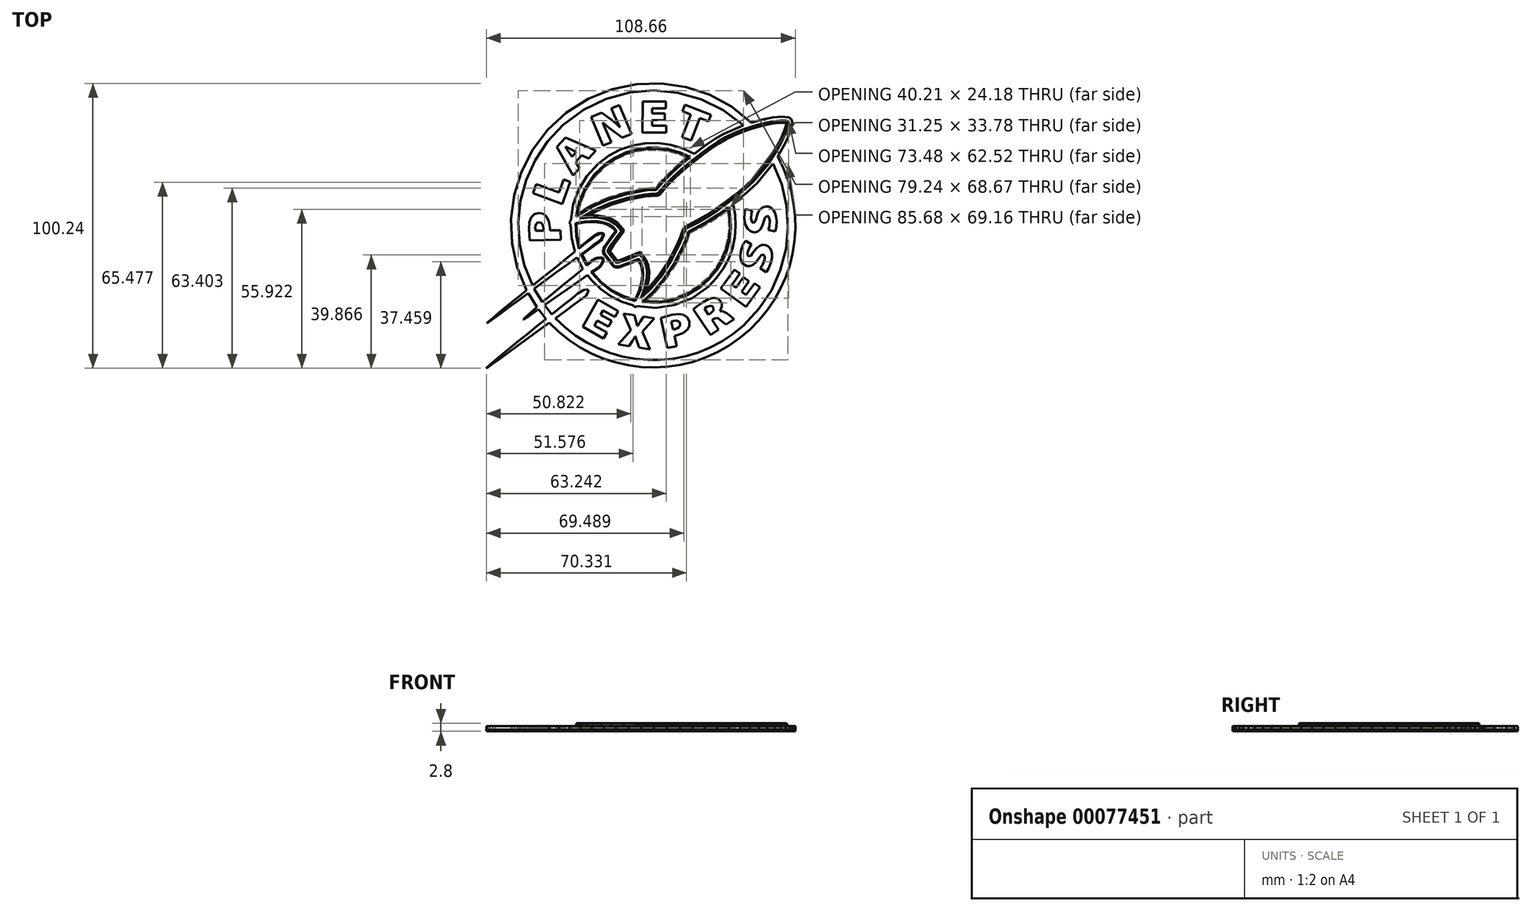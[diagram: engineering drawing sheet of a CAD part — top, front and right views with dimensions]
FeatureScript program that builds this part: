
annotation { "Feature Type Name" : "Feature", "Feature Type Description" : "" }
export const myFeature = defineFeature(function(context is Context, id is Id, definition is map)
    precondition{}
    {
        {
            var Q0;
            Q0=qCreatedBy(makeId("Top.planeOp"),FACE);
            var sketch = newSketch(context, id + "F0", { "sketchPlane" : qUnion([Q0])});
            skLineSegment(sketch, "E0", {"start": v(-40.2, -22.7) * mm, "end": v(-42.64, -24.66) * mm});
            skLineSegment(sketch, "E1", {"start": v(-42.64, -24.66) * mm, "end": v(-44.96, -26.54) * mm});
            skLineSegment(sketch, "E2", {"start": v(-44.96, -26.54) * mm, "end": v(-47.13, -28.3) * mm});
            skLineSegment(sketch, "E3", {"start": v(-47.13, -28.3) * mm, "end": v(-49.09, -29.9) * mm});
            skLineSegment(sketch, "E4", {"start": v(-49.09, -29.9) * mm, "end": v(-50.8, -31.32) * mm});
            skLineSegment(sketch, "E5", {"start": v(-50.8, -31.32) * mm, "end": v(-52.24, -32.52) * mm});
            skLineSegment(sketch, "E6", {"start": v(-52.24, -32.52) * mm, "end": v(-53.35, -33.48) * mm});
            skLineSegment(sketch, "E7", {"start": v(-53.35, -33.48) * mm, "end": v(-54.1, -34.16) * mm});
            skLineSegment(sketch, "E8", {"start": v(-54.1, -34.16) * mm, "end": v(-54.15, -34.28) * mm});
            skLineSegment(sketch, "E9", {"start": v(-54.15, -34.28) * mm, "end": v(-54.02, -34.26) * mm});
            skLineSegment(sketch, "E10", {"start": v(-54.02, -34.26) * mm, "end": v(-53.72, -34.04) * mm});
            skLineSegment(sketch, "E11", {"start": v(-53.72, -34.04) * mm, "end": v(-52.87, -33.41) * mm});
            skLineSegment(sketch, "E12", {"start": v(-52.87, -33.41) * mm, "end": v(-51.53, -32.43) * mm});
            skLineSegment(sketch, "E13", {"start": v(-51.53, -32.43) * mm, "end": v(-49.76, -31.13) * mm});
            skLineSegment(sketch, "E14", {"start": v(-49.76, -31.13) * mm, "end": v(-47.62, -29.56) * mm});
            skLineSegment(sketch, "E15", {"start": v(-47.62, -29.56) * mm, "end": v(-45.19, -27.77) * mm});
            skLineSegment(sketch, "E16", {"start": v(-45.19, -27.77) * mm, "end": v(-42.51, -25.8) * mm});
            skLineSegment(sketch, "E17", {"start": v(-42.51, -25.8) * mm, "end": v(-39.66, -23.72) * mm});
            skLineSegment(sketch, "E18", {"start": v(-39.66, -23.72) * mm, "end": v(-36.62, -28.6) * mm});
            skLineSegment(sketch, "E19", {"start": v(-36.62, -28.6) * mm, "end": v(-38.26, -30.03) * mm});
            skLineSegment(sketch, "E20", {"start": v(-38.26, -30.03) * mm, "end": v(-39.64, -31.25) * mm});
            skLineSegment(sketch, "E21", {"start": v(-39.64, -31.25) * mm, "end": v(-40.68, -32.23) * mm});
            skLineSegment(sketch, "E22", {"start": v(-40.68, -32.23) * mm, "end": v(-41.34, -32.9) * mm});
            skLineSegment(sketch, "E23", {"start": v(-41.34, -32.9) * mm, "end": v(-41.35, -33.02) * mm});
            skLineSegment(sketch, "E24", {"start": v(-41.35, -33.02) * mm, "end": v(-41.24, -33.04) * mm});
            skLineSegment(sketch, "E25", {"start": v(-41.24, -33.04) * mm, "end": v(-40.86, -32.77) * mm});
            skLineSegment(sketch, "E26", {"start": v(-40.86, -32.77) * mm, "end": v(-39.8, -32.02) * mm});
            skLineSegment(sketch, "E27", {"start": v(-39.8, -32.02) * mm, "end": v(-38.15, -30.88) * mm});
            skLineSegment(sketch, "E28", {"start": v(-38.15, -30.88) * mm, "end": v(-36.04, -29.4) * mm});
            skLineSegment(sketch, "E29", {"start": v(-36.04, -29.4) * mm, "end": v(-35.33, -30.36) * mm});
            skLineSegment(sketch, "E30", {"start": v(-35.33, -30.36) * mm, "end": v(-33.33, -32.8) * mm});
            skLineSegment(sketch, "E31", {"start": v(-33.33, -32.8) * mm, "end": v(-36.63, -35.43) * mm});
            skLineSegment(sketch, "E32", {"start": v(-36.63, -35.43) * mm, "end": v(-39.98, -38.12) * mm});
            skLineSegment(sketch, "E33", {"start": v(-39.98, -38.12) * mm, "end": v(-43.25, -40.77) * mm});
            skLineSegment(sketch, "E34", {"start": v(-43.25, -40.77) * mm, "end": v(-46.33, -43.27) * mm});
            skLineSegment(sketch, "E35", {"start": v(-46.33, -43.27) * mm, "end": v(-49.1, -45.54) * mm});
            skLineSegment(sketch, "E36", {"start": v(-49.1, -45.54) * mm, "end": v(-51.42, -47.48) * mm});
            skLineSegment(sketch, "E37", {"start": v(-51.42, -47.48) * mm, "end": v(-53.2, -49) * mm});
            skLineSegment(sketch, "E38", {"start": v(-53.2, -49) * mm, "end": v(-54.29, -50) * mm});
            skLineSegment(sketch, "E39", {"start": v(-54.29, -50) * mm, "end": v(-54.33, -50.12) * mm});
            skLineSegment(sketch, "E40", {"start": v(-54.33, -50.12) * mm, "end": v(-54.21, -50.1) * mm});
            skLineSegment(sketch, "E41", {"start": v(-54.21, -50.1) * mm, "end": v(-53.67, -49.7) * mm});
            skLineSegment(sketch, "E42", {"start": v(-53.67, -49.7) * mm, "end": v(-52.15, -48.6) * mm});
            skLineSegment(sketch, "E43", {"start": v(-52.15, -48.6) * mm, "end": v(-49.83, -46.91) * mm});
            skLineSegment(sketch, "E44", {"start": v(-49.83, -46.91) * mm, "end": v(-46.88, -44.77) * mm});
            skLineSegment(sketch, "E45", {"start": v(-46.88, -44.77) * mm, "end": v(-43.48, -42.29) * mm});
            skLineSegment(sketch, "E46", {"start": v(-43.48, -42.29) * mm, "end": v(-39.78, -39.6) * mm});
            skLineSegment(sketch, "E47", {"start": v(-39.78, -39.6) * mm, "end": v(-35.96, -36.81) * mm});
            skLineSegment(sketch, "E48", {"start": v(-35.96, -36.81) * mm, "end": v(-32.18, -34.06) * mm});
            skLineSegment(sketch, "E49", {"start": v(-32.18, -34.06) * mm, "end": v(-28.79, -37.36) * mm});
            skLineSegment(sketch, "E50", {"start": v(-28.79, -37.36) * mm, "end": v(-25.15, -40.28) * mm});
            skLineSegment(sketch, "E51", {"start": v(-25.15, -40.28) * mm, "end": v(-21.3, -42.83) * mm});
            skLineSegment(sketch, "E52", {"start": v(-21.3, -42.83) * mm, "end": v(-17.27, -44.98) * mm});
            skLineSegment(sketch, "E53", {"start": v(-17.27, -44.98) * mm, "end": v(-13.08, -46.75) * mm});
            skLineSegment(sketch, "E54", {"start": v(-13.08, -46.75) * mm, "end": v(-8.76, -48.13) * mm});
            skLineSegment(sketch, "E55", {"start": v(-8.76, -48.13) * mm, "end": v(-4.35, -49.1) * mm});
            skLineSegment(sketch, "E56", {"start": v(-4.35, -49.1) * mm, "end": v(0.13, -49.69) * mm});
            skLineSegment(sketch, "E57", {"start": v(0.13, -49.69) * mm, "end": v(4.64, -49.87) * mm});
            skLineSegment(sketch, "E58", {"start": v(4.64, -49.87) * mm, "end": v(9.17, -49.63) * mm});
            skLineSegment(sketch, "E59", {"start": v(9.17, -49.63) * mm, "end": v(13.67, -49) * mm});
            skLineSegment(sketch, "E60", {"start": v(13.67, -49) * mm, "end": v(18.12, -47.93) * mm});
            skLineSegment(sketch, "E61", {"start": v(18.12, -47.93) * mm, "end": v(22.5, -46.46) * mm});
            skLineSegment(sketch, "E62", {"start": v(22.5, -46.46) * mm, "end": v(26.76, -44.56) * mm});
            skLineSegment(sketch, "E63", {"start": v(26.76, -44.56) * mm, "end": v(30.88, -42.23) * mm});
            skLineSegment(sketch, "E64", {"start": v(30.88, -42.23) * mm, "end": v(34.84, -39.47) * mm});
            skLineSegment(sketch, "E65", {"start": v(34.84, -39.47) * mm, "end": v(38.39, -36.47) * mm});
            skLineSegment(sketch, "E66", {"start": v(38.39, -36.47) * mm, "end": v(41.6, -33.2) * mm});
            skLineSegment(sketch, "E67", {"start": v(41.6, -33.2) * mm, "end": v(44.45, -29.72) * mm});
            skLineSegment(sketch, "E68", {"start": v(44.45, -29.72) * mm, "end": v(46.95, -26.03) * mm});
            skLineSegment(sketch, "E69", {"start": v(46.95, -26.03) * mm, "end": v(49.1, -22.16) * mm});
            skLineSegment(sketch, "E70", {"start": v(49.1, -22.16) * mm, "end": v(50.88, -18.15) * mm});
            skLineSegment(sketch, "E71", {"start": v(50.88, -18.15) * mm, "end": v(52.3, -14.01) * mm});
            skLineSegment(sketch, "E72", {"start": v(52.3, -14.01) * mm, "end": v(53.34, -9.78) * mm});
            skLineSegment(sketch, "E73", {"start": v(53.34, -9.78) * mm, "end": v(54.02, -5.47) * mm});
            skLineSegment(sketch, "E74", {"start": v(54.02, -5.47) * mm, "end": v(54.33, -1.13) * mm});
            skLineSegment(sketch, "E75", {"start": v(54.33, -1.13) * mm, "end": v(54.25, 3.24) * mm});
            skLineSegment(sketch, "E76", {"start": v(54.25, 3.24) * mm, "end": v(53.8, 7.6) * mm});
            skLineSegment(sketch, "E77", {"start": v(53.8, 7.6) * mm, "end": v(52.96, 11.92) * mm});
            skLineSegment(sketch, "E78", {"start": v(52.96, 11.92) * mm, "end": v(51.73, 16.18) * mm});
            skLineSegment(sketch, "E79", {"start": v(51.73, 16.18) * mm, "end": v(50.1, 20.35) * mm});
            skLineSegment(sketch, "E80", {"start": v(50.1, 20.35) * mm, "end": v(48.09, 24.4) * mm});
            skLineSegment(sketch, "E81", {"start": v(48.09, 24.4) * mm, "end": v(49.13, 26.16) * mm});
            skLineSegment(sketch, "E82", {"start": v(49.13, 26.16) * mm, "end": v(50.31, 28.29) * mm});
            skLineSegment(sketch, "E83", {"start": v(50.31, 28.29) * mm, "end": v(51.4, 30.45) * mm});
            skLineSegment(sketch, "E84", {"start": v(51.4, 30.45) * mm, "end": v(51.98, 31.75) * mm});
            skLineSegment(sketch, "E85", {"start": v(51.98, 31.75) * mm, "end": v(52.63, 33.4) * mm});
            skLineSegment(sketch, "E86", {"start": v(52.63, 33.4) * mm, "end": v(53.1, 35.13) * mm});
            skLineSegment(sketch, "E87", {"start": v(53.1, 35.13) * mm, "end": v(53.22, 36.66) * mm});
            skLineSegment(sketch, "E88", {"start": v(53.22, 36.66) * mm, "end": v(52.86, 37.6) * mm});
            skLineSegment(sketch, "E89", {"start": v(52.86, 37.6) * mm, "end": v(51.96, 38.2) * mm});
            skLineSegment(sketch, "E90", {"start": v(51.96, 38.2) * mm, "end": v(49.54, 38.43) * mm});
            skLineSegment(sketch, "E91", {"start": v(49.54, 38.43) * mm, "end": v(46.46, 38.1) * mm});
            skLineSegment(sketch, "E92", {"start": v(46.46, 38.1) * mm, "end": v(43.37, 37.49) * mm});
            skLineSegment(sketch, "E93", {"start": v(43.37, 37.49) * mm, "end": v(40.9, 36.86) * mm});
            skLineSegment(sketch, "E94", {"start": v(40.9, 36.86) * mm, "end": v(38.93, 36.3) * mm});
            skLineSegment(sketch, "E95", {"start": v(38.93, 36.3) * mm, "end": v(31.9, 41.92) * mm});
            skLineSegment(sketch, "E96", {"start": v(31.9, 41.92) * mm, "end": v(24.13, 46.11) * mm});
            skLineSegment(sketch, "E97", {"start": v(24.13, 46.11) * mm, "end": v(15.84, 48.86) * mm});
            skLineSegment(sketch, "E98", {"start": v(15.84, 48.86) * mm, "end": v(7.22, 50.12) * mm});
            skLineSegment(sketch, "E99", {"start": v(7.22, 50.12) * mm, "end": v(-1.5, 49.87) * mm});
            skLineSegment(sketch, "E100", {"start": v(-1.5, 49.87) * mm, "end": v(-10.12, 48.09) * mm});
            skLineSegment(sketch, "E101", {"start": v(-10.12, 48.09) * mm, "end": v(-18.43, 44.74) * mm});
            skLineSegment(sketch, "E102", {"start": v(-18.43, 44.74) * mm, "end": v(-26.22, 39.8) * mm});
            skLineSegment(sketch, "E103", {"start": v(-26.22, 39.8) * mm, "end": v(-32.85, 33.69) * mm});
            skLineSegment(sketch, "E104", {"start": v(-32.85, 33.69) * mm, "end": v(-38.13, 26.69) * mm});
            skLineSegment(sketch, "E105", {"start": v(-38.13, 26.69) * mm, "end": v(-42.05, 19) * mm});
            skLineSegment(sketch, "E106", {"start": v(-42.05, 19) * mm, "end": v(-44.57, 10.84) * mm});
            skLineSegment(sketch, "E107", {"start": v(-44.57, 10.84) * mm, "end": v(-45.67, 2.39) * mm});
            skLineSegment(sketch, "E108", {"start": v(-45.67, 2.39) * mm, "end": v(-45.33, -6.15) * mm});
            skLineSegment(sketch, "E109", {"start": v(-45.33, -6.15) * mm, "end": v(-43.51, -14.58) * mm});
            skLineSegment(sketch, "E110", {"start": v(-43.51, -14.58) * mm, "end": v(-40.2, -22.7) * mm});
            skLineSegment(sketch, "E111", {"start": v(-31.31, -31.18) * mm, "end": v(-29.3, -29.56) * mm});
            skLineSegment(sketch, "E112", {"start": v(-29.3, -29.56) * mm, "end": v(-27.42, -28.07) * mm});
            skLineSegment(sketch, "E113", {"start": v(-27.42, -28.07) * mm, "end": v(-25.73, -26.72) * mm});
            skLineSegment(sketch, "E114", {"start": v(-25.73, -26.72) * mm, "end": v(-24.26, -25.56) * mm});
            skLineSegment(sketch, "E115", {"start": v(-24.26, -25.56) * mm, "end": v(-23.06, -24.6) * mm});
            skLineSegment(sketch, "E116", {"start": v(-23.06, -24.6) * mm, "end": v(-22.15, -23.88) * mm});
            skLineSegment(sketch, "E117", {"start": v(-22.15, -23.88) * mm, "end": v(-21.57, -23.42) * mm});
            skLineSegment(sketch, "E118", {"start": v(-21.57, -23.42) * mm, "end": v(-21.37, -23.26) * mm});
            skLineSegment(sketch, "E119", {"start": v(-21.37, -23.26) * mm, "end": v(-20.01, -22.57) * mm});
            skLineSegment(sketch, "E120", {"start": v(-20.01, -22.57) * mm, "end": v(-19.06, -22.42) * mm});
            skLineSegment(sketch, "E121", {"start": v(-19.06, -22.42) * mm, "end": v(-18.54, -22.56) * mm});
            skLineSegment(sketch, "E122", {"start": v(-18.54, -22.56) * mm, "end": v(-18.54, -23.1) * mm});
            skLineSegment(sketch, "E123", {"start": v(-18.54, -23.1) * mm, "end": v(-18.92, -23.99) * mm});
            skLineSegment(sketch, "E124", {"start": v(-18.92, -23.99) * mm, "end": v(-19.32, -24.55) * mm});
            skLineSegment(sketch, "E125", {"start": v(-19.32, -24.55) * mm, "end": v(-19.92, -25.1) * mm});
            skLineSegment(sketch, "E126", {"start": v(-19.92, -25.1) * mm, "end": v(-20.9, -25.83) * mm});
            skLineSegment(sketch, "E127", {"start": v(-20.9, -25.83) * mm, "end": v(-23.1, -27.43) * mm});
            skLineSegment(sketch, "E128", {"start": v(-23.1, -27.43) * mm, "end": v(-26.24, -29.73) * mm});
            skLineSegment(sketch, "E129", {"start": v(-26.24, -29.73) * mm, "end": v(-30.08, -32.53) * mm});
            skLineSegment(sketch, "E130", {"start": v(-30.08, -32.53) * mm, "end": v(-26.64, -35.8) * mm});
            skLineSegment(sketch, "E131", {"start": v(-26.64, -35.8) * mm, "end": v(-22.96, -38.67) * mm});
            skLineSegment(sketch, "E132", {"start": v(-22.96, -38.67) * mm, "end": v(-19.08, -41.13) * mm});
            skLineSegment(sketch, "E133", {"start": v(-19.08, -41.13) * mm, "end": v(-15, -43.18) * mm});
            skLineSegment(sketch, "E134", {"start": v(-15, -43.18) * mm, "end": v(-10.8, -44.82) * mm});
            skLineSegment(sketch, "E135", {"start": v(-10.8, -44.82) * mm, "end": v(-6.47, -46.05) * mm});
            skLineSegment(sketch, "E136", {"start": v(-6.47, -46.05) * mm, "end": v(-2.06, -46.85) * mm});
            skLineSegment(sketch, "E137", {"start": v(-2.06, -46.85) * mm, "end": v(2.4, -47.24) * mm});
            skLineSegment(sketch, "E138", {"start": v(2.4, -47.24) * mm, "end": v(6.87, -47.21) * mm});
            skLineSegment(sketch, "E139", {"start": v(6.87, -47.21) * mm, "end": v(11.33, -46.76) * mm});
            skLineSegment(sketch, "E140", {"start": v(11.33, -46.76) * mm, "end": v(15.75, -45.9) * mm});
            skLineSegment(sketch, "E141", {"start": v(15.75, -45.9) * mm, "end": v(20.08, -44.6) * mm});
            skLineSegment(sketch, "E142", {"start": v(20.08, -44.6) * mm, "end": v(24.31, -42.87) * mm});
            skLineSegment(sketch, "E143", {"start": v(24.31, -42.87) * mm, "end": v(28.4, -40.72) * mm});
            skLineSegment(sketch, "E144", {"start": v(28.4, -40.72) * mm, "end": v(32.31, -38.14) * mm});
            skLineSegment(sketch, "E145", {"start": v(32.31, -38.14) * mm, "end": v(36.02, -35.13) * mm});
            skLineSegment(sketch, "E146", {"start": v(36.02, -35.13) * mm, "end": v(41.58, -29.22) * mm});
            skLineSegment(sketch, "E147", {"start": v(41.58, -29.22) * mm, "end": v(45.94, -22.63) * mm});
            skLineSegment(sketch, "E148", {"start": v(45.94, -22.63) * mm, "end": v(49.1, -15.54) * mm});
            skLineSegment(sketch, "E149", {"start": v(49.1, -15.54) * mm, "end": v(51.03, -8.1) * mm});
            skLineSegment(sketch, "E150", {"start": v(51.03, -8.1) * mm, "end": v(51.75, -0.47) * mm});
            skLineSegment(sketch, "E151", {"start": v(51.75, -0.47) * mm, "end": v(51.24, 7.18) * mm});
            skLineSegment(sketch, "E152", {"start": v(51.24, 7.18) * mm, "end": v(49.49, 14.7) * mm});
            skLineSegment(sketch, "E153", {"start": v(49.49, 14.7) * mm, "end": v(46.5, 21.92) * mm});
            skLineSegment(sketch, "E154", {"start": v(46.5, 21.92) * mm, "end": v(40.88, 15.03) * mm});
            skLineSegment(sketch, "E155", {"start": v(40.88, 15.03) * mm, "end": v(36.77, 11.24) * mm});
            skLineSegment(sketch, "E156", {"start": v(36.77, 11.24) * mm, "end": v(32.34, 7.74) * mm});
            skLineSegment(sketch, "E157", {"start": v(32.34, 7.74) * mm, "end": v(33.1, 3.86) * mm});
            skLineSegment(sketch, "E158", {"start": v(33.1, 3.86) * mm, "end": v(33.34, -0.07) * mm});
            skLineSegment(sketch, "E159", {"start": v(33.34, -0.07) * mm, "end": v(33.04, -4) * mm});
            skLineSegment(sketch, "E160", {"start": v(33.04, -4) * mm, "end": v(32.22, -7.84) * mm});
            skLineSegment(sketch, "E161", {"start": v(32.22, -7.84) * mm, "end": v(30.87, -11.57) * mm});
            skLineSegment(sketch, "E162", {"start": v(30.87, -11.57) * mm, "end": v(29, -15.12) * mm});
            skLineSegment(sketch, "E163", {"start": v(29, -15.12) * mm, "end": v(26.61, -18.42) * mm});
            skLineSegment(sketch, "E164", {"start": v(26.61, -18.42) * mm, "end": v(23.71, -21.43) * mm});
            skLineSegment(sketch, "E165", {"start": v(23.71, -21.43) * mm, "end": v(18.02, -25.43) * mm});
            skLineSegment(sketch, "E166", {"start": v(18.02, -25.43) * mm, "end": v(11.75, -27.9) * mm});
            skLineSegment(sketch, "E167", {"start": v(11.75, -27.9) * mm, "end": v(5.2, -28.85) * mm});
            skLineSegment(sketch, "E168", {"start": v(5.2, -28.85) * mm, "end": v(-1.4, -28.3) * mm});
            skLineSegment(sketch, "E169", {"start": v(-1.4, -28.3) * mm, "end": v(-1.63, -28.48) * mm});
            skLineSegment(sketch, "E170", {"start": v(-1.63, -28.48) * mm, "end": v(-2.36, -28.53) * mm});
            skLineSegment(sketch, "E171", {"start": v(-2.36, -28.53) * mm, "end": v(-2.7, -28) * mm});
            skLineSegment(sketch, "E172", {"start": v(-2.7, -28) * mm, "end": v(-6.7, -26.7) * mm});
            skLineSegment(sketch, "E173", {"start": v(-6.7, -26.7) * mm, "end": v(-10.52, -24.8) * mm});
            skLineSegment(sketch, "E174", {"start": v(-10.52, -24.8) * mm, "end": v(-14.07, -22.3) * mm});
            skLineSegment(sketch, "E175", {"start": v(-14.07, -22.3) * mm, "end": v(-17.29, -19.23) * mm});
            skLineSegment(sketch, "E176", {"start": v(-17.29, -19.23) * mm, "end": v(-18.84, -17.36) * mm});
            skLineSegment(sketch, "E177", {"start": v(-18.84, -17.36) * mm, "end": v(-22.18, -19.7) * mm});
            skLineSegment(sketch, "E178", {"start": v(-22.18, -19.7) * mm, "end": v(-26.03, -22.4) * mm});
            skLineSegment(sketch, "E179", {"start": v(-26.03, -22.4) * mm, "end": v(-30.06, -25.23) * mm});
            skLineSegment(sketch, "E180", {"start": v(-30.06, -25.23) * mm, "end": v(-33.93, -27.93) * mm});
            skLineSegment(sketch, "E181", {"start": v(-33.93, -27.93) * mm, "end": v(-31.31, -31.18) * mm});
            skLineSegment(sketch, "E182", {"start": v(-38.14, -21.05) * mm, "end": v(-34.19, -17.89) * mm});
            skLineSegment(sketch, "E183", {"start": v(-34.19, -17.89) * mm, "end": v(-30.28, -14.77) * mm});
            skLineSegment(sketch, "E184", {"start": v(-30.28, -14.77) * mm, "end": v(-26.56, -11.81) * mm});
            skLineSegment(sketch, "E185", {"start": v(-26.56, -11.81) * mm, "end": v(-23.2, -9.14) * mm});
            skLineSegment(sketch, "E186", {"start": v(-23.2, -9.14) * mm, "end": v(-24.37, -4.32) * mm});
            skLineSegment(sketch, "E187", {"start": v(-24.37, -4.32) * mm, "end": v(-24.72, 0.59) * mm});
            skLineSegment(sketch, "E188", {"start": v(-24.72, 0.59) * mm, "end": v(-25.02, 0.8) * mm});
            skLineSegment(sketch, "E189", {"start": v(-25.02, 0.8) * mm, "end": v(-25.16, 1.3) * mm});
            skLineSegment(sketch, "E190", {"start": v(-25.16, 1.3) * mm, "end": v(-24.9, 1.74) * mm});
            skLineSegment(sketch, "E191", {"start": v(-24.9, 1.74) * mm, "end": v(-24.67, 1.93) * mm});
            skLineSegment(sketch, "E192", {"start": v(-24.67, 1.93) * mm, "end": v(-23.81, 7.38) * mm});
            skLineSegment(sketch, "E193", {"start": v(-23.81, 7.38) * mm, "end": v(-21.93, 12.61) * mm});
            skLineSegment(sketch, "E194", {"start": v(-21.93, 12.61) * mm, "end": v(-19.02, 17.46) * mm});
            skLineSegment(sketch, "E195", {"start": v(-19.02, 17.46) * mm, "end": v(-15.1, 21.76) * mm});
            skLineSegment(sketch, "E196", {"start": v(-15.1, 21.76) * mm, "end": v(-11.32, 24.64) * mm});
            skLineSegment(sketch, "E197", {"start": v(-11.32, 24.64) * mm, "end": v(-7.24, 26.8) * mm});
            skLineSegment(sketch, "E198", {"start": v(-7.24, 26.8) * mm, "end": v(-2.95, 28.28) * mm});
            skLineSegment(sketch, "E199", {"start": v(-2.95, 28.28) * mm, "end": v(1.47, 29.06) * mm});
            skLineSegment(sketch, "E200", {"start": v(1.47, 29.06) * mm, "end": v(5.94, 29.15) * mm});
            skLineSegment(sketch, "E201", {"start": v(5.94, 29.15) * mm, "end": v(10.38, 28.56) * mm});
            skLineSegment(sketch, "E202", {"start": v(10.38, 28.56) * mm, "end": v(14.69, 27.29) * mm});
            skLineSegment(sketch, "E203", {"start": v(14.69, 27.29) * mm, "end": v(18.79, 25.34) * mm});
            skLineSegment(sketch, "E204", {"start": v(18.79, 25.34) * mm, "end": v(21.08, 27.09) * mm});
            skLineSegment(sketch, "E205", {"start": v(21.08, 27.09) * mm, "end": v(23.47, 28.83) * mm});
            skLineSegment(sketch, "E206", {"start": v(23.47, 28.83) * mm, "end": v(26.23, 30.68) * mm});
            skLineSegment(sketch, "E207", {"start": v(26.23, 30.68) * mm, "end": v(29.12, 32.33) * mm});
            skLineSegment(sketch, "E208", {"start": v(29.12, 32.33) * mm, "end": v(36.11, 35.39) * mm});
            skLineSegment(sketch, "E209", {"start": v(36.11, 35.39) * mm, "end": v(29.02, 40.69) * mm});
            skLineSegment(sketch, "E210", {"start": v(29.02, 40.69) * mm, "end": v(21.25, 44.5) * mm});
            skLineSegment(sketch, "E211", {"start": v(21.25, 44.5) * mm, "end": v(13, 46.81) * mm});
            skLineSegment(sketch, "E212", {"start": v(13, 46.81) * mm, "end": v(4.53, 47.62) * mm});
            skLineSegment(sketch, "E213", {"start": v(4.53, 47.62) * mm, "end": v(-3.98, 46.9) * mm});
            skLineSegment(sketch, "E214", {"start": v(-3.98, 46.9) * mm, "end": v(-12.28, 44.64) * mm});
            skLineSegment(sketch, "E215", {"start": v(-12.28, 44.64) * mm, "end": v(-20.16, 40.83) * mm});
            skLineSegment(sketch, "E216", {"start": v(-20.16, 40.83) * mm, "end": v(-27.4, 35.46) * mm});
            skLineSegment(sketch, "E217", {"start": v(-27.4, 35.46) * mm, "end": v(-32.9, 29.61) * mm});
            skLineSegment(sketch, "E218", {"start": v(-32.9, 29.61) * mm, "end": v(-37.25, 23.1) * mm});
            skLineSegment(sketch, "E219", {"start": v(-37.25, 23.1) * mm, "end": v(-40.4, 16.08) * mm});
            skLineSegment(sketch, "E220", {"start": v(-40.4, 16.08) * mm, "end": v(-42.36, 8.72) * mm});
            skLineSegment(sketch, "E221", {"start": v(-42.36, 8.72) * mm, "end": v(-43.13, 1.17) * mm});
            skLineSegment(sketch, "E222", {"start": v(-43.13, 1.17) * mm, "end": v(-42.69, -6.4) * mm});
            skLineSegment(sketch, "E223", {"start": v(-42.69, -6.4) * mm, "end": v(-41.03, -13.87) * mm});
            skLineSegment(sketch, "E224", {"start": v(-41.03, -13.87) * mm, "end": v(-38.14, -21.05) * mm});
            skLineSegment(sketch, "E225", {"start": v(-22.46, -11.08) * mm, "end": v(-25.9, -13.6) * mm});
            skLineSegment(sketch, "E226", {"start": v(-25.9, -13.6) * mm, "end": v(-29.66, -16.37) * mm});
            skLineSegment(sketch, "E227", {"start": v(-29.66, -16.37) * mm, "end": v(-33.6, -19.26) * mm});
            skLineSegment(sketch, "E228", {"start": v(-33.6, -19.26) * mm, "end": v(-37.56, -22.18) * mm});
            skLineSegment(sketch, "E229", {"start": v(-37.56, -22.18) * mm, "end": v(-34.65, -26.93) * mm});
            skLineSegment(sketch, "E230", {"start": v(-34.65, -26.93) * mm, "end": v(-30.98, -23.85) * mm});
            skLineSegment(sketch, "E231", {"start": v(-30.98, -23.85) * mm, "end": v(-27.15, -20.68) * mm});
            skLineSegment(sketch, "E232", {"start": v(-27.15, -20.68) * mm, "end": v(-23.5, -17.69) * mm});
            skLineSegment(sketch, "E233", {"start": v(-23.5, -17.69) * mm, "end": v(-20.37, -15.13) * mm});
            skLineSegment(sketch, "E234", {"start": v(-20.37, -15.13) * mm, "end": v(-22.46, -11.08) * mm});
            skLineSegment(sketch, "E235", {"start": v(23.75, 36.76) * mm, "end": v(24.64, 39.06) * mm});
            skLineSegment(sketch, "E236", {"start": v(24.64, 39.06) * mm, "end": v(15.5, 42.6) * mm});
            skLineSegment(sketch, "E237", {"start": v(15.5, 42.6) * mm, "end": v(14.6, 40.3) * mm});
            skLineSegment(sketch, "E238", {"start": v(14.6, 40.3) * mm, "end": v(17.59, 39.14) * mm});
            skLineSegment(sketch, "E239", {"start": v(17.59, 39.14) * mm, "end": v(14.52, 31.2) * mm});
            skLineSegment(sketch, "E240", {"start": v(14.52, 31.2) * mm, "end": v(17.65, 30) * mm});
            skLineSegment(sketch, "E241", {"start": v(17.65, 30) * mm, "end": v(20.72, 37.93) * mm});
            skLineSegment(sketch, "E242", {"start": v(20.72, 37.93) * mm, "end": v(23.75, 36.76) * mm});
            skLineSegment(sketch, "E243", {"start": v(8.42, 37.2) * mm, "end": v(8.43, 39.58) * mm});
            skLineSegment(sketch, "E244", {"start": v(8.43, 39.58) * mm, "end": v(3.94, 39.6) * mm});
            skLineSegment(sketch, "E245", {"start": v(3.94, 39.6) * mm, "end": v(3.95, 41.37) * mm});
            skLineSegment(sketch, "E246", {"start": v(3.95, 41.37) * mm, "end": v(8.72, 41.34) * mm});
            skLineSegment(sketch, "E247", {"start": v(8.72, 41.34) * mm, "end": v(8.74, 43.75) * mm});
            skLineSegment(sketch, "E248", {"start": v(8.74, 43.75) * mm, "end": v(0.6, 43.8) * mm});
            skLineSegment(sketch, "E249", {"start": v(0.6, 43.8) * mm, "end": v(0.53, 32.82) * mm});
            skLineSegment(sketch, "E250", {"start": v(0.53, 32.82) * mm, "end": v(8.93, 32.76) * mm});
            skLineSegment(sketch, "E251", {"start": v(8.93, 32.76) * mm, "end": v(8.94, 35.17) * mm});
            skLineSegment(sketch, "E252", {"start": v(8.94, 35.17) * mm, "end": v(3.9, 35.2) * mm});
            skLineSegment(sketch, "E253", {"start": v(3.9, 35.2) * mm, "end": v(3.92, 37.23) * mm});
            skLineSegment(sketch, "E254", {"start": v(3.92, 37.23) * mm, "end": v(8.42, 37.2) * mm});
            skLineSegment(sketch, "E255", {"start": v(-10.44, 29.37) * mm, "end": v(-11.48, 31.87) * mm});
            skLineSegment(sketch, "E256", {"start": v(-11.48, 31.87) * mm, "end": v(-12.5, 34.22) * mm});
            skLineSegment(sketch, "E257", {"start": v(-12.5, 34.22) * mm, "end": v(-13.5, 36.34) * mm});
            skLineSegment(sketch, "E258", {"start": v(-13.5, 36.34) * mm, "end": v(-13.42, 36.37) * mm});
            skLineSegment(sketch, "E259", {"start": v(-13.42, 36.37) * mm, "end": v(-11.7, 34.88) * mm});
            skLineSegment(sketch, "E260", {"start": v(-11.7, 34.88) * mm, "end": v(-9.96, 33.53) * mm});
            skLineSegment(sketch, "E261", {"start": v(-9.96, 33.53) * mm, "end": v(-6.58, 30.99) * mm});
            skLineSegment(sketch, "E262", {"start": v(-6.58, 30.99) * mm, "end": v(-3.32, 32.35) * mm});
            skLineSegment(sketch, "E263", {"start": v(-3.32, 32.35) * mm, "end": v(-7.56, 42.48) * mm});
            skLineSegment(sketch, "E264", {"start": v(-7.56, 42.48) * mm, "end": v(-10.39, 41.3) * mm});
            skLineSegment(sketch, "E265", {"start": v(-10.39, 41.3) * mm, "end": v(-9.38, 38.9) * mm});
            skLineSegment(sketch, "E266", {"start": v(-9.38, 38.9) * mm, "end": v(-8.41, 36.73) * mm});
            skLineSegment(sketch, "E267", {"start": v(-8.41, 36.73) * mm, "end": v(-7.36, 34.74) * mm});
            skLineSegment(sketch, "E268", {"start": v(-7.36, 34.74) * mm, "end": v(-7.41, 34.72) * mm});
            skLineSegment(sketch, "E269", {"start": v(-7.41, 34.72) * mm, "end": v(-9.05, 36.2) * mm});
            skLineSegment(sketch, "E270", {"start": v(-9.05, 36.2) * mm, "end": v(-10.72, 37.5) * mm});
            skLineSegment(sketch, "E271", {"start": v(-10.72, 37.5) * mm, "end": v(-13.85, 39.85) * mm});
            skLineSegment(sketch, "E272", {"start": v(-13.85, 39.85) * mm, "end": v(-17.5, 38.32) * mm});
            skLineSegment(sketch, "E273", {"start": v(-17.5, 38.32) * mm, "end": v(-13.26, 28.2) * mm});
            skLineSegment(sketch, "E274", {"start": v(-13.26, 28.2) * mm, "end": v(-10.44, 29.37) * mm});
            skLineSegment(sketch, "E275", {"start": v(-20.78, 24.85) * mm, "end": v(-18.36, 23.73) * mm});
            skLineSegment(sketch, "E276", {"start": v(-18.36, 23.73) * mm, "end": v(-15.93, 26.4) * mm});
            skLineSegment(sketch, "E277", {"start": v(-15.93, 26.4) * mm, "end": v(-26.56, 31.04) * mm});
            skLineSegment(sketch, "E278", {"start": v(-26.56, 31.04) * mm, "end": v(-29.56, 27.74) * mm});
            skLineSegment(sketch, "E279", {"start": v(-29.56, 27.74) * mm, "end": v(-23.9, 17.66) * mm});
            skLineSegment(sketch, "E280", {"start": v(-23.9, 17.66) * mm, "end": v(-21.55, 20.23) * mm});
            skLineSegment(sketch, "E281", {"start": v(-21.55, 20.23) * mm, "end": v(-22.96, 22.46) * mm});
            skLineSegment(sketch, "E282", {"start": v(-22.96, 22.46) * mm, "end": v(-20.78, 24.85) * mm});
            skLineSegment(sketch, "E283", {"start": v(-24.26, 24.25) * mm, "end": v(-25.35, 25.97) * mm});
            skLineSegment(sketch, "E284", {"start": v(-25.35, 25.97) * mm, "end": v(-25.96, 26.9) * mm});
            skLineSegment(sketch, "E285", {"start": v(-25.96, 26.9) * mm, "end": v(-26.58, 27.85) * mm});
            skLineSegment(sketch, "E286", {"start": v(-26.58, 27.85) * mm, "end": v(-26.56, 27.87) * mm});
            skLineSegment(sketch, "E287", {"start": v(-26.56, 27.87) * mm, "end": v(-25.54, 27.36) * mm});
            skLineSegment(sketch, "E288", {"start": v(-25.54, 27.36) * mm, "end": v(-24.54, 26.87) * mm});
            skLineSegment(sketch, "E289", {"start": v(-24.54, 26.87) * mm, "end": v(-22.7, 25.96) * mm});
            skLineSegment(sketch, "E290", {"start": v(-22.7, 25.96) * mm, "end": v(-24.26, 24.25) * mm});
            skLineSegment(sketch, "E291", {"start": v(-37.98, 11.46) * mm, "end": v(-27.65, 7.73) * mm});
            skLineSegment(sketch, "E292", {"start": v(-27.65, 7.73) * mm, "end": v(-24.88, 15.42) * mm});
            skLineSegment(sketch, "E293", {"start": v(-24.88, 15.42) * mm, "end": v(-27.2, 16.25) * mm});
            skLineSegment(sketch, "E294", {"start": v(-27.2, 16.25) * mm, "end": v(-28.82, 11.73) * mm});
            skLineSegment(sketch, "E295", {"start": v(-28.82, 11.73) * mm, "end": v(-36.84, 14.62) * mm});
            skLineSegment(sketch, "E296", {"start": v(-36.84, 14.62) * mm, "end": v(-37.98, 11.46) * mm});
            skLineSegment(sketch, "E297", {"start": v(-28.23, -4.9) * mm, "end": v(-28.29, -1.58) * mm});
            skLineSegment(sketch, "E298", {"start": v(-28.29, -1.58) * mm, "end": v(-32.02, -1.65) * mm});
            skLineSegment(sketch, "E299", {"start": v(-32.02, -1.65) * mm, "end": v(-32.01, -1.29) * mm});
            skLineSegment(sketch, "E300", {"start": v(-32.01, -1.29) * mm, "end": v(-32, -0.83) * mm});
            skLineSegment(sketch, "E301", {"start": v(-32, -0.83) * mm, "end": v(-32.32, 1.5) * mm});
            skLineSegment(sketch, "E302", {"start": v(-32.32, 1.5) * mm, "end": v(-33.22, 3.31) * mm});
            skLineSegment(sketch, "E303", {"start": v(-33.22, 3.31) * mm, "end": v(-34.41, 4.2) * mm});
            skLineSegment(sketch, "E304", {"start": v(-34.41, 4.2) * mm, "end": v(-35.95, 4.48) * mm});
            skLineSegment(sketch, "E305", {"start": v(-35.95, 4.48) * mm, "end": v(-37.47, 4.06) * mm});
            skLineSegment(sketch, "E306", {"start": v(-37.47, 4.06) * mm, "end": v(-38.56, 3) * mm});
            skLineSegment(sketch, "E307", {"start": v(-38.56, 3) * mm, "end": v(-39.19, 1.36) * mm});
            skLineSegment(sketch, "E308", {"start": v(-39.19, 1.36) * mm, "end": v(-39.36, -0.99) * mm});
            skLineSegment(sketch, "E309", {"start": v(-39.36, -0.99) * mm, "end": v(-39.25, -3.41) * mm});
            skLineSegment(sketch, "E310", {"start": v(-39.25, -3.41) * mm, "end": v(-39.04, -5.1) * mm});
            skLineSegment(sketch, "E311", {"start": v(-39.04, -5.1) * mm, "end": v(-28.23, -4.9) * mm});
            skLineSegment(sketch, "E312", {"start": v(-37.07, -1.74) * mm, "end": v(-37.12, -1.37) * mm});
            skLineSegment(sketch, "E313", {"start": v(-37.12, -1.37) * mm, "end": v(-37.15, -0.76) * mm});
            skLineSegment(sketch, "E314", {"start": v(-37.15, -0.76) * mm, "end": v(-37.07, 0.08) * mm});
            skLineSegment(sketch, "E315", {"start": v(-37.07, 0.08) * mm, "end": v(-36.8, 0.68) * mm});
            skLineSegment(sketch, "E316", {"start": v(-36.8, 0.68) * mm, "end": v(-36.38, 1.04) * mm});
            skLineSegment(sketch, "E317", {"start": v(-36.38, 1.04) * mm, "end": v(-35.82, 1.16) * mm});
            skLineSegment(sketch, "E318", {"start": v(-35.82, 1.16) * mm, "end": v(-35.18, 1.03) * mm});
            skLineSegment(sketch, "E319", {"start": v(-35.18, 1.03) * mm, "end": v(-34.69, 0.61) * mm});
            skLineSegment(sketch, "E320", {"start": v(-34.69, 0.61) * mm, "end": v(-34.37, -0.05) * mm});
            skLineSegment(sketch, "E321", {"start": v(-34.37, -0.05) * mm, "end": v(-34.25, -0.93) * mm});
            skLineSegment(sketch, "E322", {"start": v(-34.25, -0.93) * mm, "end": v(-34.25, -1.37) * mm});
            skLineSegment(sketch, "E323", {"start": v(-34.25, -1.37) * mm, "end": v(-34.27, -1.69) * mm});
            skLineSegment(sketch, "E324", {"start": v(-34.27, -1.69) * mm, "end": v(-37.07, -1.74) * mm});
            skLineSegment(sketch, "E325", {"start": v(47.25, -2) * mm, "end": v(47.63, -0.45) * mm});
            skLineSegment(sketch, "E326", {"start": v(47.63, -0.45) * mm, "end": v(47.73, 1.7) * mm});
            skLineSegment(sketch, "E327", {"start": v(47.73, 1.7) * mm, "end": v(47.51, 3.35) * mm});
            skLineSegment(sketch, "E328", {"start": v(47.51, 3.35) * mm, "end": v(47.08, 4.68) * mm});
            skLineSegment(sketch, "E329", {"start": v(47.08, 4.68) * mm, "end": v(46.47, 5.68) * mm});
            skLineSegment(sketch, "E330", {"start": v(46.47, 5.68) * mm, "end": v(45.72, 6.36) * mm});
            skLineSegment(sketch, "E331", {"start": v(45.72, 6.36) * mm, "end": v(44.87, 6.75) * mm});
            skLineSegment(sketch, "E332", {"start": v(44.87, 6.75) * mm, "end": v(43.95, 6.84) * mm});
            skLineSegment(sketch, "E333", {"start": v(43.95, 6.84) * mm, "end": v(42.9, 6.6) * mm});
            skLineSegment(sketch, "E334", {"start": v(42.9, 6.6) * mm, "end": v(42.04, 5.95) * mm});
            skLineSegment(sketch, "E335", {"start": v(42.04, 5.95) * mm, "end": v(41.35, 4.9) * mm});
            skLineSegment(sketch, "E336", {"start": v(41.35, 4.9) * mm, "end": v(40.82, 3.42) * mm});
            skLineSegment(sketch, "E337", {"start": v(40.82, 3.42) * mm, "end": v(40.53, 2.38) * mm});
            skLineSegment(sketch, "E338", {"start": v(40.53, 2.38) * mm, "end": v(40.28, 1.67) * mm});
            skLineSegment(sketch, "E339", {"start": v(40.28, 1.67) * mm, "end": v(40, 1.25) * mm});
            skLineSegment(sketch, "E340", {"start": v(40, 1.25) * mm, "end": v(39.65, 1.1) * mm});
            skLineSegment(sketch, "E341", {"start": v(39.65, 1.1) * mm, "end": v(39.04, 1.48) * mm});
            skLineSegment(sketch, "E342", {"start": v(39.04, 1.48) * mm, "end": v(38.75, 2.64) * mm});
            skLineSegment(sketch, "E343", {"start": v(38.75, 2.64) * mm, "end": v(38.85, 4.27) * mm});
            skLineSegment(sketch, "E344", {"start": v(38.85, 4.27) * mm, "end": v(39.13, 5.37) * mm});
            skLineSegment(sketch, "E345", {"start": v(39.13, 5.37) * mm, "end": v(36.73, 5.95) * mm});
            skLineSegment(sketch, "E346", {"start": v(36.73, 5.95) * mm, "end": v(36.42, 4.5) * mm});
            skLineSegment(sketch, "E347", {"start": v(36.42, 4.5) * mm, "end": v(36.36, 2.55) * mm});
            skLineSegment(sketch, "E348", {"start": v(36.36, 2.55) * mm, "end": v(36.73, 0.45) * mm});
            skLineSegment(sketch, "E349", {"start": v(36.73, 0.45) * mm, "end": v(37.54, -1.1) * mm});
            skLineSegment(sketch, "E350", {"start": v(37.54, -1.1) * mm, "end": v(38.68, -2.03) * mm});
            skLineSegment(sketch, "E351", {"start": v(38.68, -2.03) * mm, "end": v(40.06, -2.3) * mm});
            skLineSegment(sketch, "E352", {"start": v(40.06, -2.3) * mm, "end": v(41.15, -1.98) * mm});
            skLineSegment(sketch, "E353", {"start": v(41.15, -1.98) * mm, "end": v(42.02, -1.22) * mm});
            skLineSegment(sketch, "E354", {"start": v(42.02, -1.22) * mm, "end": v(42.68, -0.07) * mm});
            skLineSegment(sketch, "E355", {"start": v(42.68, -0.07) * mm, "end": v(43.18, 1.4) * mm});
            skLineSegment(sketch, "E356", {"start": v(43.18, 1.4) * mm, "end": v(43.68, 2.94) * mm});
            skLineSegment(sketch, "E357", {"start": v(43.68, 2.94) * mm, "end": v(44.33, 3.44) * mm});
            skLineSegment(sketch, "E358", {"start": v(44.33, 3.44) * mm, "end": v(45, 3.05) * mm});
            skLineSegment(sketch, "E359", {"start": v(45, 3.05) * mm, "end": v(45.31, 1.77) * mm});
            skLineSegment(sketch, "E360", {"start": v(45.31, 1.77) * mm, "end": v(45.2, -0.05) * mm});
            skLineSegment(sketch, "E361", {"start": v(45.2, -0.05) * mm, "end": v(44.8, -1.5) * mm});
            skLineSegment(sketch, "E362", {"start": v(44.8, -1.5) * mm, "end": v(47.25, -2) * mm});
            skLineSegment(sketch, "E363", {"start": v(44.05, -16.27) * mm, "end": v(44.92, -14.93) * mm});
            skLineSegment(sketch, "E364", {"start": v(44.92, -14.93) * mm, "end": v(45.73, -12.94) * mm});
            skLineSegment(sketch, "E365", {"start": v(45.73, -12.94) * mm, "end": v(46.08, -11.3) * mm});
            skLineSegment(sketch, "E366", {"start": v(46.08, -11.3) * mm, "end": v(46.12, -9.91) * mm});
            skLineSegment(sketch, "E367", {"start": v(46.12, -9.91) * mm, "end": v(45.88, -8.77) * mm});
            skLineSegment(sketch, "E368", {"start": v(45.88, -8.77) * mm, "end": v(45.4, -7.87) * mm});
            skLineSegment(sketch, "E369", {"start": v(45.4, -7.87) * mm, "end": v(44.72, -7.23) * mm});
            skLineSegment(sketch, "E370", {"start": v(44.72, -7.23) * mm, "end": v(43.89, -6.83) * mm});
            skLineSegment(sketch, "E371", {"start": v(43.89, -6.83) * mm, "end": v(42.81, -6.71) * mm});
            skLineSegment(sketch, "E372", {"start": v(42.81, -6.71) * mm, "end": v(41.79, -7.03) * mm});
            skLineSegment(sketch, "E373", {"start": v(41.79, -7.03) * mm, "end": v(40.79, -7.79) * mm});
            skLineSegment(sketch, "E374", {"start": v(40.79, -7.79) * mm, "end": v(39.8, -9) * mm});
            skLineSegment(sketch, "E375", {"start": v(39.8, -9) * mm, "end": v(39.17, -9.89) * mm});
            skLineSegment(sketch, "E376", {"start": v(39.17, -9.89) * mm, "end": v(38.7, -10.48) * mm});
            skLineSegment(sketch, "E377", {"start": v(38.7, -10.48) * mm, "end": v(37.92, -10.8) * mm});
            skLineSegment(sketch, "E378", {"start": v(37.92, -10.8) * mm, "end": v(37.47, -10.24) * mm});
            skLineSegment(sketch, "E379", {"start": v(37.47, -10.24) * mm, "end": v(37.58, -9.05) * mm});
            skLineSegment(sketch, "E380", {"start": v(37.58, -9.05) * mm, "end": v(38.22, -7.55) * mm});
            skLineSegment(sketch, "E381", {"start": v(38.22, -7.55) * mm, "end": v(38.85, -6.6) * mm});
            skLineSegment(sketch, "E382", {"start": v(38.85, -6.6) * mm, "end": v(36.8, -5.25) * mm});
            skLineSegment(sketch, "E383", {"start": v(36.8, -5.25) * mm, "end": v(36, -6.52) * mm});
            skLineSegment(sketch, "E384", {"start": v(36, -6.52) * mm, "end": v(35.3, -8.34) * mm});
            skLineSegment(sketch, "E385", {"start": v(35.3, -8.34) * mm, "end": v(34.95, -10.45) * mm});
            skLineSegment(sketch, "E386", {"start": v(34.95, -10.45) * mm, "end": v(35.2, -12.17) * mm});
            skLineSegment(sketch, "E387", {"start": v(35.2, -12.17) * mm, "end": v(35.96, -13.43) * mm});
            skLineSegment(sketch, "E388", {"start": v(35.96, -13.43) * mm, "end": v(37.17, -14.14) * mm});
            skLineSegment(sketch, "E389", {"start": v(37.17, -14.14) * mm, "end": v(38.3, -14.21) * mm});
            skLineSegment(sketch, "E390", {"start": v(38.3, -14.21) * mm, "end": v(39.38, -13.78) * mm});
            skLineSegment(sketch, "E391", {"start": v(39.38, -13.78) * mm, "end": v(40.38, -12.92) * mm});
            skLineSegment(sketch, "E392", {"start": v(40.38, -12.92) * mm, "end": v(41.34, -11.7) * mm});
            skLineSegment(sketch, "E393", {"start": v(41.34, -11.7) * mm, "end": v(41.88, -10.91) * mm});
            skLineSegment(sketch, "E394", {"start": v(41.88, -10.91) * mm, "end": v(42.33, -10.4) * mm});
            skLineSegment(sketch, "E395", {"start": v(42.33, -10.4) * mm, "end": v(43.1, -10.16) * mm});
            skLineSegment(sketch, "E396", {"start": v(43.1, -10.16) * mm, "end": v(43.61, -10.75) * mm});
            skLineSegment(sketch, "E397", {"start": v(43.61, -10.75) * mm, "end": v(43.63, -11.32) * mm});
            skLineSegment(sketch, "E398", {"start": v(43.63, -11.32) * mm, "end": v(43.48, -12.06) * mm});
            skLineSegment(sketch, "E399", {"start": v(43.48, -12.06) * mm, "end": v(42.76, -13.74) * mm});
            skLineSegment(sketch, "E400", {"start": v(42.76, -13.74) * mm, "end": v(41.9, -14.98) * mm});
            skLineSegment(sketch, "E401", {"start": v(41.9, -14.98) * mm, "end": v(44.05, -16.27) * mm});
            skLineSegment(sketch, "E402", {"start": v(38.03, -19.51) * mm, "end": v(36.1, -18.12) * mm});
            skLineSegment(sketch, "E403", {"start": v(36.1, -18.12) * mm, "end": v(33.46, -21.75) * mm});
            skLineSegment(sketch, "E404", {"start": v(33.46, -21.75) * mm, "end": v(32.04, -20.72) * mm});
            skLineSegment(sketch, "E405", {"start": v(32.04, -20.72) * mm, "end": v(34.85, -16.86) * mm});
            skLineSegment(sketch, "E406", {"start": v(34.85, -16.86) * mm, "end": v(32.9, -15.44) * mm});
            skLineSegment(sketch, "E407", {"start": v(32.9, -15.44) * mm, "end": v(28.11, -22.02) * mm});
            skLineSegment(sketch, "E408", {"start": v(28.11, -22.02) * mm, "end": v(37, -28.47) * mm});
            skLineSegment(sketch, "E409", {"start": v(37, -28.47) * mm, "end": v(41.93, -21.68) * mm});
            skLineSegment(sketch, "E410", {"start": v(41.93, -21.68) * mm, "end": v(39.98, -20.27) * mm});
            skLineSegment(sketch, "E411", {"start": v(39.98, -20.27) * mm, "end": v(37.02, -24.34) * mm});
            skLineSegment(sketch, "E412", {"start": v(37.02, -24.34) * mm, "end": v(35.39, -23.15) * mm});
            skLineSegment(sketch, "E413", {"start": v(35.39, -23.15) * mm, "end": v(38.03, -19.51) * mm});
            skLineSegment(sketch, "E414", {"start": v(24.5, -38.39) * mm, "end": v(27.26, -36.54) * mm});
            skLineSegment(sketch, "E415", {"start": v(27.26, -36.54) * mm, "end": v(24.97, -33.11) * mm});
            skLineSegment(sketch, "E416", {"start": v(24.97, -33.11) * mm, "end": v(25.42, -32.81) * mm});
            skLineSegment(sketch, "E417", {"start": v(25.42, -32.81) * mm, "end": v(26.57, -32.4) * mm});
            skLineSegment(sketch, "E418", {"start": v(26.57, -32.4) * mm, "end": v(27.15, -32.6) * mm});
            skLineSegment(sketch, "E419", {"start": v(27.15, -32.6) * mm, "end": v(27.83, -33.1) * mm});
            skLineSegment(sketch, "E420", {"start": v(27.83, -33.1) * mm, "end": v(29.17, -34.21) * mm});
            skLineSegment(sketch, "E421", {"start": v(29.17, -34.21) * mm, "end": v(29.97, -34.73) * mm});
            skLineSegment(sketch, "E422", {"start": v(29.97, -34.73) * mm, "end": v(32.81, -32.84) * mm});
            skLineSegment(sketch, "E423", {"start": v(32.81, -32.84) * mm, "end": v(32.15, -32.37) * mm});
            skLineSegment(sketch, "E424", {"start": v(32.15, -32.37) * mm, "end": v(31.2, -31.6) * mm});
            skLineSegment(sketch, "E425", {"start": v(31.2, -31.6) * mm, "end": v(30.21, -30.79) * mm});
            skLineSegment(sketch, "E426", {"start": v(30.21, -30.79) * mm, "end": v(29.03, -30.11) * mm});
            skLineSegment(sketch, "E427", {"start": v(29.03, -30.11) * mm, "end": v(27.8, -30.04) * mm});
            skLineSegment(sketch, "E428", {"start": v(27.8, -30.04) * mm, "end": v(27.76, -30) * mm});
            skLineSegment(sketch, "E429", {"start": v(27.76, -30) * mm, "end": v(28.43, -28.42) * mm});
            skLineSegment(sketch, "E430", {"start": v(28.43, -28.42) * mm, "end": v(28.43, -27.5) * mm});
            skLineSegment(sketch, "E431", {"start": v(28.43, -27.5) * mm, "end": v(28.07, -26.6) * mm});
            skLineSegment(sketch, "E432", {"start": v(28.07, -26.6) * mm, "end": v(27.04, -25.62) * mm});
            skLineSegment(sketch, "E433", {"start": v(27.04, -25.62) * mm, "end": v(25.73, -25.3) * mm});
            skLineSegment(sketch, "E434", {"start": v(25.73, -25.3) * mm, "end": v(23.9, -25.72) * mm});
            skLineSegment(sketch, "E435", {"start": v(23.9, -25.72) * mm, "end": v(21.72, -26.94) * mm});
            skLineSegment(sketch, "E436", {"start": v(21.72, -26.94) * mm, "end": v(19.85, -28.27) * mm});
            skLineSegment(sketch, "E437", {"start": v(19.85, -28.27) * mm, "end": v(18.5, -29.39) * mm});
            skLineSegment(sketch, "E438", {"start": v(18.5, -29.39) * mm, "end": v(24.5, -38.39) * mm});
            skLineSegment(sketch, "E439", {"start": v(22.37, -29.2) * mm, "end": v(22.67, -28.95) * mm});
            skLineSegment(sketch, "E440", {"start": v(22.67, -28.95) * mm, "end": v(23.28, -28.52) * mm});
            skLineSegment(sketch, "E441", {"start": v(23.28, -28.52) * mm, "end": v(24.53, -28.1) * mm});
            skLineSegment(sketch, "E442", {"start": v(24.53, -28.1) * mm, "end": v(25.03, -28.24) * mm});
            skLineSegment(sketch, "E443", {"start": v(25.03, -28.24) * mm, "end": v(25.43, -28.63) * mm});
            skLineSegment(sketch, "E444", {"start": v(25.43, -28.63) * mm, "end": v(25.54, -29.74) * mm});
            skLineSegment(sketch, "E445", {"start": v(25.54, -29.74) * mm, "end": v(24.53, -30.86) * mm});
            skLineSegment(sketch, "E446", {"start": v(24.53, -30.86) * mm, "end": v(23.8, -31.35) * mm});
            skLineSegment(sketch, "E447", {"start": v(23.8, -31.35) * mm, "end": v(22.37, -29.2) * mm});
            skLineSegment(sketch, "E448", {"start": v(9.33, -43.05) * mm, "end": v(12.57, -42.33) * mm});
            skLineSegment(sketch, "E449", {"start": v(12.57, -42.33) * mm, "end": v(11.77, -38.69) * mm});
            skLineSegment(sketch, "E450", {"start": v(11.77, -38.69) * mm, "end": v(12.12, -38.63) * mm});
            skLineSegment(sketch, "E451", {"start": v(12.12, -38.63) * mm, "end": v(12.57, -38.54) * mm});
            skLineSegment(sketch, "E452", {"start": v(12.57, -38.54) * mm, "end": v(14.8, -37.77) * mm});
            skLineSegment(sketch, "E453", {"start": v(14.8, -37.77) * mm, "end": v(16.4, -36.53) * mm});
            skLineSegment(sketch, "E454", {"start": v(16.4, -36.53) * mm, "end": v(17.03, -35.19) * mm});
            skLineSegment(sketch, "E455", {"start": v(17.03, -35.19) * mm, "end": v(17, -33.63) * mm});
            skLineSegment(sketch, "E456", {"start": v(17, -33.63) * mm, "end": v(16.29, -32.21) * mm});
            skLineSegment(sketch, "E457", {"start": v(16.29, -32.21) * mm, "end": v(15.04, -31.36) * mm});
            skLineSegment(sketch, "E458", {"start": v(15.04, -31.36) * mm, "end": v(13.3, -31.07) * mm});
            skLineSegment(sketch, "E459", {"start": v(13.3, -31.07) * mm, "end": v(10.97, -31.36) * mm});
            skLineSegment(sketch, "E460", {"start": v(10.97, -31.36) * mm, "end": v(8.61, -31.95) * mm});
            skLineSegment(sketch, "E461", {"start": v(8.61, -31.95) * mm, "end": v(7, -32.48) * mm});
            skLineSegment(sketch, "E462", {"start": v(7, -32.48) * mm, "end": v(9.33, -43.05) * mm});
            skLineSegment(sketch, "E463", {"start": v(10.68, -33.75) * mm, "end": v(11.03, -33.63) * mm});
            skLineSegment(sketch, "E464", {"start": v(11.03, -33.63) * mm, "end": v(11.63, -33.48) * mm});
            skLineSegment(sketch, "E465", {"start": v(11.63, -33.48) * mm, "end": v(12.47, -33.4) * mm});
            skLineSegment(sketch, "E466", {"start": v(12.47, -33.4) * mm, "end": v(13.1, -33.54) * mm});
            skLineSegment(sketch, "E467", {"start": v(13.1, -33.54) * mm, "end": v(13.54, -33.89) * mm});
            skLineSegment(sketch, "E468", {"start": v(13.54, -33.89) * mm, "end": v(13.77, -34.4) * mm});
            skLineSegment(sketch, "E469", {"start": v(13.77, -34.4) * mm, "end": v(13.77, -35.06) * mm});
            skLineSegment(sketch, "E470", {"start": v(13.77, -35.06) * mm, "end": v(13.46, -35.63) * mm});
            skLineSegment(sketch, "E471", {"start": v(13.46, -35.63) * mm, "end": v(12.87, -36.07) * mm});
            skLineSegment(sketch, "E472", {"start": v(12.87, -36.07) * mm, "end": v(12.03, -36.36) * mm});
            skLineSegment(sketch, "E473", {"start": v(12.03, -36.36) * mm, "end": v(11.6, -36.45) * mm});
            skLineSegment(sketch, "E474", {"start": v(11.6, -36.45) * mm, "end": v(11.28, -36.5) * mm});
            skLineSegment(sketch, "E475", {"start": v(11.28, -36.5) * mm, "end": v(10.68, -33.75) * mm});
            skLineSegment(sketch, "E476", {"start": v(3.17, -43.46) * mm, "end": v(0.46, -37.34) * mm});
            skLineSegment(sketch, "E477", {"start": v(0.46, -37.34) * mm, "end": v(4.65, -32.57) * mm});
            skLineSegment(sketch, "E478", {"start": v(4.65, -32.57) * mm, "end": v(0.87, -31.98) * mm});
            skLineSegment(sketch, "E479", {"start": v(0.87, -31.98) * mm, "end": v(-0.15, -33.6) * mm});
            skLineSegment(sketch, "E480", {"start": v(-0.15, -33.6) * mm, "end": v(-0.65, -34.4) * mm});
            skLineSegment(sketch, "E481", {"start": v(-0.65, -34.4) * mm, "end": v(-1.17, -35.27) * mm});
            skLineSegment(sketch, "E482", {"start": v(-1.17, -35.27) * mm, "end": v(-1.2, -35.27) * mm});
            skLineSegment(sketch, "E483", {"start": v(-1.2, -35.27) * mm, "end": v(-1.46, -34.3) * mm});
            skLineSegment(sketch, "E484", {"start": v(-1.46, -34.3) * mm, "end": v(-1.75, -33.33) * mm});
            skLineSegment(sketch, "E485", {"start": v(-1.75, -33.33) * mm, "end": v(-2.32, -31.48) * mm});
            skLineSegment(sketch, "E486", {"start": v(-2.32, -31.48) * mm, "end": v(-6.12, -30.88) * mm});
            skLineSegment(sketch, "E487", {"start": v(-6.12, -30.88) * mm, "end": v(-3.6, -36.77) * mm});
            skLineSegment(sketch, "E488", {"start": v(-3.6, -36.77) * mm, "end": v(-7.95, -41.71) * mm});
            skLineSegment(sketch, "E489", {"start": v(-7.95, -41.71) * mm, "end": v(-4.19, -42.3) * mm});
            skLineSegment(sketch, "E490", {"start": v(-4.19, -42.3) * mm, "end": v(-3.08, -40.65) * mm});
            skLineSegment(sketch, "E491", {"start": v(-3.08, -40.65) * mm, "end": v(-2.5, -39.76) * mm});
            skLineSegment(sketch, "E492", {"start": v(-2.5, -39.76) * mm, "end": v(-1.98, -38.9) * mm});
            skLineSegment(sketch, "E493", {"start": v(-1.98, -38.9) * mm, "end": v(-1.94, -38.91) * mm});
            skLineSegment(sketch, "E494", {"start": v(-1.94, -38.91) * mm, "end": v(-1.63, -39.9) * mm});
            skLineSegment(sketch, "E495", {"start": v(-1.63, -39.9) * mm, "end": v(-1.29, -40.94) * mm});
            skLineSegment(sketch, "E496", {"start": v(-1.29, -40.94) * mm, "end": v(-0.66, -42.86) * mm});
            skLineSegment(sketch, "E497", {"start": v(-0.66, -42.86) * mm, "end": v(3.17, -43.46) * mm});
            skLineSegment(sketch, "E498", {"start": v(-11.44, -35.55) * mm, "end": v(-10.27, -33.48) * mm});
            skLineSegment(sketch, "E499", {"start": v(-10.27, -33.48) * mm, "end": v(-14.19, -31.27) * mm});
            skLineSegment(sketch, "E500", {"start": v(-14.19, -31.27) * mm, "end": v(-13.32, -29.74) * mm});
            skLineSegment(sketch, "E501", {"start": v(-13.32, -29.74) * mm, "end": v(-9.16, -32.09) * mm});
            skLineSegment(sketch, "E502", {"start": v(-9.16, -32.09) * mm, "end": v(-7.98, -29.99) * mm});
            skLineSegment(sketch, "E503", {"start": v(-7.98, -29.99) * mm, "end": v(-15.06, -25.98) * mm});
            skLineSegment(sketch, "E504", {"start": v(-15.06, -25.98) * mm, "end": v(-20.46, -35.54) * mm});
            skLineSegment(sketch, "E505", {"start": v(-20.46, -35.54) * mm, "end": v(-13.16, -39.68) * mm});
            skLineSegment(sketch, "E506", {"start": v(-13.16, -39.68) * mm, "end": v(-11.97, -37.58) * mm});
            skLineSegment(sketch, "E507", {"start": v(-11.97, -37.58) * mm, "end": v(-16.35, -35.1) * mm});
            skLineSegment(sketch, "E508", {"start": v(-16.35, -35.1) * mm, "end": v(-15.36, -33.34) * mm});
            skLineSegment(sketch, "E509", {"start": v(-15.36, -33.34) * mm, "end": v(-11.44, -35.55) * mm});
            skLineSegment(sketch, "E510", {"start": v(51.82, 36.77) * mm, "end": v(51.57, 36.92) * mm});
            skLineSegment(sketch, "E511", {"start": v(51.57, 36.92) * mm, "end": v(50.93, 37.06) * mm});
            skLineSegment(sketch, "E512", {"start": v(50.93, 37.06) * mm, "end": v(48.82, 37.06) * mm});
            skLineSegment(sketch, "E513", {"start": v(48.82, 37.06) * mm, "end": v(46.26, 36.72) * mm});
            skLineSegment(sketch, "E514", {"start": v(46.26, 36.72) * mm, "end": v(43.61, 36.18) * mm});
            skLineSegment(sketch, "E515", {"start": v(43.61, 36.18) * mm, "end": v(41.24, 35.58) * mm});
            skLineSegment(sketch, "E516", {"start": v(41.24, 35.58) * mm, "end": v(38.46, 34.76) * mm});
            skLineSegment(sketch, "E517", {"start": v(38.46, 34.76) * mm, "end": v(35.72, 33.83) * mm});
            skLineSegment(sketch, "E518", {"start": v(35.72, 33.83) * mm, "end": v(32.68, 32.6) * mm});
            skLineSegment(sketch, "E519", {"start": v(32.68, 32.6) * mm, "end": v(29.74, 31.16) * mm});
            skLineSegment(sketch, "E520", {"start": v(29.74, 31.16) * mm, "end": v(26.94, 29.54) * mm});
            skLineSegment(sketch, "E521", {"start": v(26.94, 29.54) * mm, "end": v(24.25, 27.75) * mm});
            skLineSegment(sketch, "E522", {"start": v(24.25, 27.75) * mm, "end": v(21.35, 25.62) * mm});
            skLineSegment(sketch, "E523", {"start": v(21.35, 25.62) * mm, "end": v(18.51, 23.43) * mm});
            skLineSegment(sketch, "E524", {"start": v(18.51, 23.43) * mm, "end": v(18.5, 23.42) * mm});
            skLineSegment(sketch, "E525", {"start": v(18.5, 23.42) * mm, "end": v(15.11, 20.66) * mm});
            skLineSegment(sketch, "E526", {"start": v(15.11, 20.66) * mm, "end": v(12, 17.84) * mm});
            skLineSegment(sketch, "E527", {"start": v(12, 17.84) * mm, "end": v(9.04, 14.86) * mm});
            skLineSegment(sketch, "E528", {"start": v(9.04, 14.86) * mm, "end": v(6.12, 11.6) * mm});
            skLineSegment(sketch, "E529", {"start": v(6.12, 11.6) * mm, "end": v(5.63, 11.37) * mm});
            skLineSegment(sketch, "E530", {"start": v(5.63, 11.37) * mm, "end": v(3.48, 11.26) * mm});
            skLineSegment(sketch, "E531", {"start": v(3.48, 11.26) * mm, "end": v(1.35, 11.03) * mm});
            skLineSegment(sketch, "E532", {"start": v(1.35, 11.03) * mm, "end": v(-4.68, 9.9) * mm});
            skLineSegment(sketch, "E533", {"start": v(-4.68, 9.9) * mm, "end": v(-10.6, 8.1) * mm});
            skLineSegment(sketch, "E534", {"start": v(-10.6, 8.1) * mm, "end": v(-16.3, 5.66) * mm});
            skLineSegment(sketch, "E535", {"start": v(-16.3, 5.66) * mm, "end": v(-21.58, 2.54) * mm});
            skLineSegment(sketch, "E536", {"start": v(-21.58, 2.54) * mm, "end": v(-20.1, 2.75) * mm});
            skLineSegment(sketch, "E537", {"start": v(-20.1, 2.75) * mm, "end": v(-17.64, 2.95) * mm});
            skLineSegment(sketch, "E538", {"start": v(-17.64, 2.95) * mm, "end": v(-15.18, 2.86) * mm});
            skLineSegment(sketch, "E539", {"start": v(-15.18, 2.86) * mm, "end": v(-12.95, 2.5) * mm});
            skLineSegment(sketch, "E540", {"start": v(-12.95, 2.5) * mm, "end": v(-10.83, 1.75) * mm});
            skLineSegment(sketch, "E541", {"start": v(-10.83, 1.75) * mm, "end": v(-8.7, 0.44) * mm});
            skLineSegment(sketch, "E542", {"start": v(-8.7, 0.44) * mm, "end": v(-7.08, -1.45) * mm});
            skLineSegment(sketch, "E543", {"start": v(-7.08, -1.45) * mm, "end": v(-6.82, -1.84) * mm});
            skLineSegment(sketch, "E544", {"start": v(-6.82, -1.84) * mm, "end": v(-8.95, -4.66) * mm});
            skLineSegment(sketch, "E545", {"start": v(-8.95, -4.66) * mm, "end": v(-10.24, -6.41) * mm});
            skLineSegment(sketch, "E546", {"start": v(-10.24, -6.41) * mm, "end": v(-11.47, -8.2) * mm});
            skLineSegment(sketch, "E547", {"start": v(-11.47, -8.2) * mm, "end": v(-11.67, -8.68) * mm});
            skLineSegment(sketch, "E548", {"start": v(-11.67, -8.68) * mm, "end": v(-11.61, -9.18) * mm});
            skLineSegment(sketch, "E549", {"start": v(-11.61, -9.18) * mm, "end": v(-8.8, -12.85) * mm});
            skLineSegment(sketch, "E550", {"start": v(-8.8, -12.85) * mm, "end": v(-8.34, -13.02) * mm});
            skLineSegment(sketch, "E551", {"start": v(-8.34, -13.02) * mm, "end": v(-7.82, -12.95) * mm});
            skLineSegment(sketch, "E552", {"start": v(-7.82, -12.95) * mm, "end": v(-5.98, -12.3) * mm});
            skLineSegment(sketch, "E553", {"start": v(-5.98, -12.3) * mm, "end": v(-4.16, -11.58) * mm});
            skLineSegment(sketch, "E554", {"start": v(-4.16, -11.58) * mm, "end": v(-0.47, -10.08) * mm});
            skLineSegment(sketch, "E555", {"start": v(-0.47, -10.08) * mm, "end": v(-0.16, -10.42) * mm});
            skLineSegment(sketch, "E556", {"start": v(-0.16, -10.42) * mm, "end": v(1.02, -12.07) * mm});
            skLineSegment(sketch, "E557", {"start": v(1.02, -12.07) * mm, "end": v(1.77, -13.95) * mm});
            skLineSegment(sketch, "E558", {"start": v(1.77, -13.95) * mm, "end": v(2.14, -16.14) * mm});
            skLineSegment(sketch, "E559", {"start": v(2.14, -16.14) * mm, "end": v(2.07, -18.37) * mm});
            skLineSegment(sketch, "E560", {"start": v(2.07, -18.37) * mm, "end": v(1.3, -22.01) * mm});
            skLineSegment(sketch, "E561", {"start": v(1.3, -22.01) * mm, "end": v(0, -25.46) * mm});
            skLineSegment(sketch, "E562", {"start": v(0, -25.46) * mm, "end": v(3.65, -21.96) * mm});
            skLineSegment(sketch, "E563", {"start": v(3.65, -21.96) * mm, "end": v(6.88, -18.07) * mm});
            skLineSegment(sketch, "E564", {"start": v(6.88, -18.07) * mm, "end": v(10.46, -12.7) * mm});
            skLineSegment(sketch, "E565", {"start": v(10.46, -12.7) * mm, "end": v(13.4, -6.99) * mm});
            skLineSegment(sketch, "E566", {"start": v(13.4, -6.99) * mm, "end": v(14.54, -4.24) * mm});
            skLineSegment(sketch, "E567", {"start": v(14.54, -4.24) * mm, "end": v(15.48, -1.42) * mm});
            skLineSegment(sketch, "E568", {"start": v(15.48, -1.42) * mm, "end": v(15.83, -1) * mm});
            skLineSegment(sketch, "E569", {"start": v(15.83, -1) * mm, "end": v(19.72, 0.99) * mm});
            skLineSegment(sketch, "E570", {"start": v(19.72, 0.99) * mm, "end": v(23.36, 3.09) * mm});
            skLineSegment(sketch, "E571", {"start": v(23.36, 3.09) * mm, "end": v(26.88, 5.38) * mm});
            skLineSegment(sketch, "E572", {"start": v(26.88, 5.38) * mm, "end": v(30.42, 7.95) * mm});
            skLineSegment(sketch, "E573", {"start": v(30.42, 7.95) * mm, "end": v(32.77, 9.76) * mm});
            skLineSegment(sketch, "E574", {"start": v(32.77, 9.76) * mm, "end": v(35.1, 11.6) * mm});
            skLineSegment(sketch, "E575", {"start": v(35.1, 11.6) * mm, "end": v(37.58, 13.71) * mm});
            skLineSegment(sketch, "E576", {"start": v(37.58, 13.71) * mm, "end": v(39.94, 15.97) * mm});
            skLineSegment(sketch, "E577", {"start": v(39.94, 15.97) * mm, "end": v(44.3, 21.13) * mm});
            skLineSegment(sketch, "E578", {"start": v(44.3, 21.13) * mm, "end": v(47.98, 26.83) * mm});
            skLineSegment(sketch, "E579", {"start": v(47.98, 26.83) * mm, "end": v(49.13, 28.9) * mm});
            skLineSegment(sketch, "E580", {"start": v(49.13, 28.9) * mm, "end": v(50.2, 31.03) * mm});
            skLineSegment(sketch, "E581", {"start": v(50.2, 31.03) * mm, "end": v(50.67, 32.07) * mm});
            skLineSegment(sketch, "E582", {"start": v(50.67, 32.07) * mm, "end": v(51.27, 33.57) * mm});
            skLineSegment(sketch, "E583", {"start": v(51.27, 33.57) * mm, "end": v(51.76, 35.17) * mm});
            skLineSegment(sketch, "E584", {"start": v(51.76, 35.17) * mm, "end": v(51.9, 36.52) * mm});
            skLineSegment(sketch, "E585", {"start": v(51.9, 36.52) * mm, "end": v(51.82, 36.77) * mm});
            skLineSegment(sketch, "E586", {"start": v(30.89, 6.64) * mm, "end": v(27.44, 4.15) * mm});
            skLineSegment(sketch, "E587", {"start": v(27.44, 4.15) * mm, "end": v(24.01, 1.93) * mm});
            skLineSegment(sketch, "E588", {"start": v(24.01, 1.93) * mm, "end": v(20.47, -0.12) * mm});
            skLineSegment(sketch, "E589", {"start": v(20.47, -0.12) * mm, "end": v(16.67, -2.08) * mm});
            skLineSegment(sketch, "E590", {"start": v(16.67, -2.08) * mm, "end": v(15.74, -4.84) * mm});
            skLineSegment(sketch, "E591", {"start": v(15.74, -4.84) * mm, "end": v(14.62, -7.53) * mm});
            skLineSegment(sketch, "E592", {"start": v(14.62, -7.53) * mm, "end": v(11.61, -13.37) * mm});
            skLineSegment(sketch, "E593", {"start": v(11.61, -13.37) * mm, "end": v(7.95, -18.86) * mm});
            skLineSegment(sketch, "E594", {"start": v(7.95, -18.86) * mm, "end": v(4.36, -23.16) * mm});
            skLineSegment(sketch, "E595", {"start": v(4.36, -23.16) * mm, "end": v(0.38, -26.9) * mm});
            skLineSegment(sketch, "E596", {"start": v(0.38, -26.9) * mm, "end": v(5.72, -27.14) * mm});
            skLineSegment(sketch, "E597", {"start": v(5.72, -27.14) * mm, "end": v(11.04, -26.34) * mm});
            skLineSegment(sketch, "E598", {"start": v(11.04, -26.34) * mm, "end": v(16.2, -24.47) * mm});
            skLineSegment(sketch, "E599", {"start": v(16.2, -24.47) * mm, "end": v(21, -21.5) * mm});
            skLineSegment(sketch, "E600", {"start": v(21, -21.5) * mm, "end": v(24.06, -18.75) * mm});
            skLineSegment(sketch, "E601", {"start": v(24.06, -18.75) * mm, "end": v(26.62, -15.66) * mm});
            skLineSegment(sketch, "E602", {"start": v(26.62, -15.66) * mm, "end": v(28.66, -12.3) * mm});
            skLineSegment(sketch, "E603", {"start": v(28.66, -12.3) * mm, "end": v(30.18, -8.7) * mm});
            skLineSegment(sketch, "E604", {"start": v(30.18, -8.7) * mm, "end": v(31.17, -4.95) * mm});
            skLineSegment(sketch, "E605", {"start": v(31.17, -4.95) * mm, "end": v(31.63, -1.1) * mm});
            skLineSegment(sketch, "E606", {"start": v(31.63, -1.1) * mm, "end": v(31.53, 2.78) * mm});
            skLineSegment(sketch, "E607", {"start": v(31.53, 2.78) * mm, "end": v(30.89, 6.64) * mm});
            skLineSegment(sketch, "E608", {"start": v(-1.97, -26.45) * mm, "end": v(-1.14, -24.75) * mm});
            skLineSegment(sketch, "E609", {"start": v(-1.14, -24.75) * mm, "end": v(-0.4, -22.9) * mm});
            skLineSegment(sketch, "E610", {"start": v(-0.4, -22.9) * mm, "end": v(0.22, -20.95) * mm});
            skLineSegment(sketch, "E611", {"start": v(0.22, -20.95) * mm, "end": v(0.64, -18.97) * mm});
            skLineSegment(sketch, "E612", {"start": v(0.64, -18.97) * mm, "end": v(0.8, -17) * mm});
            skLineSegment(sketch, "E613", {"start": v(0.8, -17) * mm, "end": v(0.66, -15.09) * mm});
            skLineSegment(sketch, "E614", {"start": v(0.66, -15.09) * mm, "end": v(0.12, -13.3) * mm});
            skLineSegment(sketch, "E615", {"start": v(0.12, -13.3) * mm, "end": v(-0.85, -11.67) * mm});
            skLineSegment(sketch, "E616", {"start": v(-0.85, -11.67) * mm, "end": v(-3.65, -12.81) * mm});
            skLineSegment(sketch, "E617", {"start": v(-3.65, -12.81) * mm, "end": v(-5.51, -13.55) * mm});
            skLineSegment(sketch, "E618", {"start": v(-5.51, -13.55) * mm, "end": v(-7.4, -14.22) * mm});
            skLineSegment(sketch, "E619", {"start": v(-7.4, -14.22) * mm, "end": v(-8.05, -14.35) * mm});
            skLineSegment(sketch, "E620", {"start": v(-8.05, -14.35) * mm, "end": v(-8.7, -14.32) * mm});
            skLineSegment(sketch, "E621", {"start": v(-8.7, -14.32) * mm, "end": v(-9.32, -14.1) * mm});
            skLineSegment(sketch, "E622", {"start": v(-9.32, -14.1) * mm, "end": v(-9.83, -13.69) * mm});
            skLineSegment(sketch, "E623", {"start": v(-9.83, -13.69) * mm, "end": v(-12.7, -9.95) * mm});
            skLineSegment(sketch, "E624", {"start": v(-12.7, -9.95) * mm, "end": v(-12.98, -9.35) * mm});
            skLineSegment(sketch, "E625", {"start": v(-12.98, -9.35) * mm, "end": v(-13.02, -8.7) * mm});
            skLineSegment(sketch, "E626", {"start": v(-13.02, -8.7) * mm, "end": v(-12.88, -8.06) * mm});
            skLineSegment(sketch, "E627", {"start": v(-12.88, -8.06) * mm, "end": v(-12.58, -7.48) * mm});
            skLineSegment(sketch, "E628", {"start": v(-12.58, -7.48) * mm, "end": v(-11.33, -5.64) * mm});
            skLineSegment(sketch, "E629", {"start": v(-11.33, -5.64) * mm, "end": v(-10, -3.86) * mm});
            skLineSegment(sketch, "E630", {"start": v(-10, -3.86) * mm, "end": v(-8.45, -1.8) * mm});
            skLineSegment(sketch, "E631", {"start": v(-8.45, -1.8) * mm, "end": v(-9.75, -0.44) * mm});
            skLineSegment(sketch, "E632", {"start": v(-9.75, -0.44) * mm, "end": v(-11.37, 0.54) * mm});
            skLineSegment(sketch, "E633", {"start": v(-11.37, 0.54) * mm, "end": v(-13.28, 1.2) * mm});
            skLineSegment(sketch, "E634", {"start": v(-13.28, 1.2) * mm, "end": v(-15.29, 1.53) * mm});
            skLineSegment(sketch, "E635", {"start": v(-15.29, 1.53) * mm, "end": v(-17.62, 1.61) * mm});
            skLineSegment(sketch, "E636", {"start": v(-17.62, 1.61) * mm, "end": v(-19.94, 1.43) * mm});
            skLineSegment(sketch, "E637", {"start": v(-19.94, 1.43) * mm, "end": v(-23.03, 0.9) * mm});
            skLineSegment(sketch, "E638", {"start": v(-23.03, 0.9) * mm, "end": v(-22.78, -3.6) * mm});
            skLineSegment(sketch, "E639", {"start": v(-22.78, -3.6) * mm, "end": v(-21.79, -8.03) * mm});
            skLineSegment(sketch, "E640", {"start": v(-21.79, -8.03) * mm, "end": v(-19.52, -6.23) * mm});
            skLineSegment(sketch, "E641", {"start": v(-19.52, -6.23) * mm, "end": v(-17.77, -4.85) * mm});
            skLineSegment(sketch, "E642", {"start": v(-17.77, -4.85) * mm, "end": v(-16.65, -3.97) * mm});
            skLineSegment(sketch, "E643", {"start": v(-16.65, -3.97) * mm, "end": v(-16.25, -3.65) * mm});
            skLineSegment(sketch, "E644", {"start": v(-16.25, -3.65) * mm, "end": v(-14.88, -2.94) * mm});
            skLineSegment(sketch, "E645", {"start": v(-14.88, -2.94) * mm, "end": v(-13.93, -2.78) * mm});
            skLineSegment(sketch, "E646", {"start": v(-13.93, -2.78) * mm, "end": v(-13.4, -2.91) * mm});
            skLineSegment(sketch, "E647", {"start": v(-13.4, -2.91) * mm, "end": v(-13.42, -3.45) * mm});
            skLineSegment(sketch, "E648", {"start": v(-13.42, -3.45) * mm, "end": v(-13.81, -4.33) * mm});
            skLineSegment(sketch, "E649", {"start": v(-13.81, -4.33) * mm, "end": v(-14.22, -4.9) * mm});
            skLineSegment(sketch, "E650", {"start": v(-14.22, -4.9) * mm, "end": v(-14.83, -5.46) * mm});
            skLineSegment(sketch, "E651", {"start": v(-14.83, -5.46) * mm, "end": v(-15.42, -5.9) * mm});
            skLineSegment(sketch, "E652", {"start": v(-15.42, -5.9) * mm, "end": v(-16.72, -6.86) * mm});
            skLineSegment(sketch, "E653", {"start": v(-16.72, -6.86) * mm, "end": v(-18.63, -8.27) * mm});
            skLineSegment(sketch, "E654", {"start": v(-18.63, -8.27) * mm, "end": v(-21.06, -10.05) * mm});
            skLineSegment(sketch, "E655", {"start": v(-21.06, -10.05) * mm, "end": v(-19.05, -14.05) * mm});
            skLineSegment(sketch, "E656", {"start": v(-19.05, -14.05) * mm, "end": v(-18.15, -13.32) * mm});
            skLineSegment(sketch, "E657", {"start": v(-18.15, -13.32) * mm, "end": v(-17.47, -12.77) * mm});
            skLineSegment(sketch, "E658", {"start": v(-17.47, -12.77) * mm, "end": v(-17.04, -12.42) * mm});
            skLineSegment(sketch, "E659", {"start": v(-17.04, -12.42) * mm, "end": v(-16.88, -12.3) * mm});
            skLineSegment(sketch, "E660", {"start": v(-16.88, -12.3) * mm, "end": v(-16.12, -11.81) * mm});
            skLineSegment(sketch, "E661", {"start": v(-16.12, -11.81) * mm, "end": v(-15.27, -11.5) * mm});
            skLineSegment(sketch, "E662", {"start": v(-15.27, -11.5) * mm, "end": v(-14.13, -11.38) * mm});
            skLineSegment(sketch, "E663", {"start": v(-14.13, -11.38) * mm, "end": v(-13.49, -11.57) * mm});
            skLineSegment(sketch, "E664", {"start": v(-13.49, -11.57) * mm, "end": v(-13.46, -12.25) * mm});
            skLineSegment(sketch, "E665", {"start": v(-13.46, -12.25) * mm, "end": v(-13.88, -13.32) * mm});
            skLineSegment(sketch, "E666", {"start": v(-13.88, -13.32) * mm, "end": v(-14.33, -14) * mm});
            skLineSegment(sketch, "E667", {"start": v(-14.33, -14) * mm, "end": v(-15.03, -14.65) * mm});
            skLineSegment(sketch, "E668", {"start": v(-15.03, -14.65) * mm, "end": v(-15.31, -14.86) * mm});
            skLineSegment(sketch, "E669", {"start": v(-15.31, -14.86) * mm, "end": v(-15.83, -15.23) * mm});
            skLineSegment(sketch, "E670", {"start": v(-15.83, -15.23) * mm, "end": v(-16.55, -15.74) * mm});
            skLineSegment(sketch, "E671", {"start": v(-16.55, -15.74) * mm, "end": v(-17.46, -16.39) * mm});
            skLineSegment(sketch, "E672", {"start": v(-17.46, -16.39) * mm, "end": v(-17.36, -16.52) * mm});
            skLineSegment(sketch, "E673", {"start": v(-17.36, -16.52) * mm, "end": v(-14.1, -20.06) * mm});
            skLineSegment(sketch, "E674", {"start": v(-14.1, -20.06) * mm, "end": v(-10.38, -22.9) * mm});
            skLineSegment(sketch, "E675", {"start": v(-10.38, -22.9) * mm, "end": v(-6.3, -25.04) * mm});
            skLineSegment(sketch, "E676", {"start": v(-6.3, -25.04) * mm, "end": v(-1.97, -26.45) * mm});
            skLineSegment(sketch, "E677", {"start": v(-22.86, 3.27) * mm, "end": v(-17.32, 6.62) * mm});
            skLineSegment(sketch, "E678", {"start": v(-17.32, 6.62) * mm, "end": v(-11.38, 9.24) * mm});
            skLineSegment(sketch, "E679", {"start": v(-11.38, 9.24) * mm, "end": v(-5.17, 11.15) * mm});
            skLineSegment(sketch, "E680", {"start": v(-5.17, 11.15) * mm, "end": v(1.17, 12.35) * mm});
            skLineSegment(sketch, "E681", {"start": v(1.17, 12.35) * mm, "end": v(3.23, 12.57) * mm});
            skLineSegment(sketch, "E682", {"start": v(3.23, 12.57) * mm, "end": v(5.3, 12.7) * mm});
            skLineSegment(sketch, "E683", {"start": v(5.3, 12.7) * mm, "end": v(8.16, 15.86) * mm});
            skLineSegment(sketch, "E684", {"start": v(8.16, 15.86) * mm, "end": v(11.04, 18.77) * mm});
            skLineSegment(sketch, "E685", {"start": v(11.04, 18.77) * mm, "end": v(14.07, 21.52) * mm});
            skLineSegment(sketch, "E686", {"start": v(14.07, 21.52) * mm, "end": v(17.35, 24.2) * mm});
            skLineSegment(sketch, "E687", {"start": v(17.35, 24.2) * mm, "end": v(13.8, 25.82) * mm});
            skLineSegment(sketch, "E688", {"start": v(13.8, 25.82) * mm, "end": v(10.06, 26.9) * mm});
            skLineSegment(sketch, "E689", {"start": v(10.06, 26.9) * mm, "end": v(6.23, 27.45) * mm});
            skLineSegment(sketch, "E690", {"start": v(6.23, 27.45) * mm, "end": v(2.35, 27.45) * mm});
            skLineSegment(sketch, "E691", {"start": v(2.35, 27.45) * mm, "end": v(-1.52, 26.9) * mm});
            skLineSegment(sketch, "E692", {"start": v(-1.52, 26.9) * mm, "end": v(-5.3, 25.78) * mm});
            skLineSegment(sketch, "E693", {"start": v(-5.3, 25.78) * mm, "end": v(-8.94, 24.1) * mm});
            skLineSegment(sketch, "E694", {"start": v(-8.94, 24.1) * mm, "end": v(-12.38, 21.83) * mm});
            skLineSegment(sketch, "E695", {"start": v(-12.38, 21.83) * mm, "end": v(-16.48, 17.95) * mm});
            skLineSegment(sketch, "E696", {"start": v(-16.48, 17.95) * mm, "end": v(-19.6, 13.45) * mm});
            skLineSegment(sketch, "E697", {"start": v(-19.6, 13.45) * mm, "end": v(-21.74, 8.5) * mm});
            skLineSegment(sketch, "E698", {"start": v(-21.74, 8.5) * mm, "end": v(-22.86, 3.27) * mm});
            skLineSegment(sketch, "E699", {"start": v(-35.7, -25.13) * mm, "end": v(-36.1, -24.48) * mm});
            skLineSegment(sketch, "E700", {"start": v(-36.1, -24.48) * mm, "end": v(-36.5, -23.85) * mm});
            skLineSegment(sketch, "E701", {"start": v(-36.5, -23.85) * mm, "end": v(-36.82, -23.3) * mm});
            skLineSegment(sketch, "E702", {"start": v(-36.82, -23.3) * mm, "end": v(-37.04, -22.9) * mm});
            skLineSegment(sketch, "E703", {"start": v(-37.04, -22.9) * mm, "end": v(-37.4, -22.2) * mm});
            skLineSegment(sketch, "E704", {"start": v(-37.4, -22.2) * mm, "end": v(-22.54, -11.28) * mm});
            skLineSegment(sketch, "E705", {"start": v(-22.54, -11.28) * mm, "end": v(-21.57, -13.18) * mm});
            skLineSegment(sketch, "E706", {"start": v(-21.57, -13.18) * mm, "end": v(-21.2, -13.92) * mm});
            skLineSegment(sketch, "E707", {"start": v(-21.2, -13.92) * mm, "end": v(-20.88, -14.53) * mm});
            skLineSegment(sketch, "E708", {"start": v(-20.88, -14.53) * mm, "end": v(-20.67, -14.95) * mm});
            skLineSegment(sketch, "E709", {"start": v(-20.67, -14.95) * mm, "end": v(-20.6, -15.12) * mm});
            skLineSegment(sketch, "E710", {"start": v(-20.6, -15.12) * mm, "end": v(-20.88, -15.38) * mm});
            skLineSegment(sketch, "E711", {"start": v(-20.88, -15.38) * mm, "end": v(-21.67, -16.03) * mm});
            skLineSegment(sketch, "E712", {"start": v(-21.67, -16.03) * mm, "end": v(-22.82, -16.99) * mm});
            skLineSegment(sketch, "E713", {"start": v(-22.82, -16.99) * mm, "end": v(-24.24, -18.15) * mm});
            skLineSegment(sketch, "E714", {"start": v(-24.24, -18.15) * mm, "end": v(-25.91, -19.52) * mm});
            skLineSegment(sketch, "E715", {"start": v(-25.91, -19.52) * mm, "end": v(-27.78, -21.06) * mm});
            skLineSegment(sketch, "E716", {"start": v(-27.78, -21.06) * mm, "end": v(-29.6, -22.58) * mm});
            skLineSegment(sketch, "E717", {"start": v(-29.6, -22.58) * mm, "end": v(-31.18, -23.88) * mm});
            skLineSegment(sketch, "E718", {"start": v(-31.18, -23.88) * mm, "end": v(-32.46, -24.95) * mm});
            skLineSegment(sketch, "E719", {"start": v(-32.46, -24.95) * mm, "end": v(-33.54, -25.83) * mm});
            skLineSegment(sketch, "E720", {"start": v(-33.54, -25.83) * mm, "end": v(-34.29, -26.42) * mm});
            skLineSegment(sketch, "E721", {"start": v(-34.29, -26.42) * mm, "end": v(-34.6, -26.64) * mm});
            skLineSegment(sketch, "E722", {"start": v(-34.6, -26.64) * mm, "end": v(-34.73, -26.52) * mm});
            skLineSegment(sketch, "E723", {"start": v(-34.73, -26.52) * mm, "end": v(-34.97, -26.2) * mm});
            skLineSegment(sketch, "E724", {"start": v(-34.97, -26.2) * mm, "end": v(-35.31, -25.71) * mm});
            skLineSegment(sketch, "E725", {"start": v(-35.31, -25.71) * mm, "end": v(-35.7, -25.13) * mm});
            skSolve(sketch);
        }
        {
            assignVariable(context, id + "F1", {"name" : "lh", "anyValue" : 0.6 * mm});
        }
        {
            var Q0;
            Q0=makeQuery(id+"F0.imprint","IMPRINT",FACE,{"disambiguationData":[TD([[makeQuery(id+"F0.imprint","IMPRINT",EDGE,{"derivedFrom":sQuery(id+"F0.wireOp",EDGE,"E312")}),-1.0]])]});
            var Q1;
            Q1=makeQuery(id+"F0.imprint","IMPRINT",FACE,{"disambiguationData":[TD([[makeQuery(id+"F0.imprint","IMPRINT",EDGE,{"derivedFrom":sQuery(id+"F0.wireOp",EDGE,"E283")}),-1.0]])]});
            var Q2;
            Q2=makeQuery(id+"F0.imprint","IMPRINT",FACE,{"disambiguationData":[TD([[makeQuery(id+"F0.imprint","IMPRINT",EDGE,{"derivedFrom":sQuery(id+"F0.wireOp",EDGE,"E463")}),-1.0]])]});
            var Q3;
            Q3=makeQuery(id+"F0.imprint","IMPRINT",FACE,{"disambiguationData":[TD([[makeQuery(id+"F0.imprint","IMPRINT",EDGE,{"derivedFrom":sQuery(id+"F0.wireOp",EDGE,"E439")}),-1.0]])]});
            var Q4;
            Q4=makeQuery(id+"F0.imprint","IMPRINT",FACE,{"disambiguationData":[TD([[makeQuery(id+"F0.imprint","IMPRINT",EDGE,{"derivedFrom":sQuery(id+"F0.wireOp",EDGE,"E182")}),1.0]])]});
            var Q5;
            Q5=makeQuery(id+"F0.imprint","IMPRINT",FACE,{"disambiguationData":[TD([[makeQuery(id+"F0.imprint","IMPRINT",EDGE,{"derivedFrom":sQuery(id+"F0.wireOp",EDGE,"E111")}),1.0]])]});
            var Q6;
            Q6=makeQuery(id+"F0.imprint","IMPRINT",FACE,{"disambiguationData":[TD([[makeQuery(id+"F0.imprint","IMPRINT",EDGE,{"derivedFrom":sQuery(id+"F0.wireOp",EDGE,"E699")}),-1.0]])]});
            var Q7;
            Q7=makeQuery(id+"F0.imprint","IMPRINT",FACE,{"disambiguationData":[TD([[makeQuery(id+"F0.imprint","IMPRINT",EDGE,{"derivedFrom":sQuery(id+"F0.wireOp",EDGE,"E297")}),1.0]])]});
            var Q8;
            Q8=makeQuery(id+"F0.imprint","IMPRINT",FACE,{"disambiguationData":[TD([[makeQuery(id+"F0.imprint","IMPRINT",EDGE,{"derivedFrom":sQuery(id+"F0.wireOp",EDGE,"E291")}),1.0]])]});
            var Q9;
            Q9=makeQuery(id+"F0.imprint","IMPRINT",FACE,{"disambiguationData":[TD([[makeQuery(id+"F0.imprint","IMPRINT",EDGE,{"derivedFrom":sQuery(id+"F0.wireOp",EDGE,"E275")}),1.0]])]});
            var Q10;
            Q10=makeQuery(id+"F0.imprint","IMPRINT",FACE,{"disambiguationData":[TD([[makeQuery(id+"F0.imprint","IMPRINT",EDGE,{"derivedFrom":sQuery(id+"F0.wireOp",EDGE,"E255")}),1.0]])]});
            var Q11;
            Q11=makeQuery(id+"F0.imprint","IMPRINT",FACE,{"disambiguationData":[TD([[makeQuery(id+"F0.imprint","IMPRINT",EDGE,{"derivedFrom":sQuery(id+"F0.wireOp",EDGE,"E243")}),1.0]])]});
            var Q12;
            Q12=makeQuery(id+"F0.imprint","IMPRINT",FACE,{"disambiguationData":[TD([[makeQuery(id+"F0.imprint","IMPRINT",EDGE,{"derivedFrom":sQuery(id+"F0.wireOp",EDGE,"E235")}),1.0]])]});
            var Q13;
            Q13=makeQuery(id+"F0.imprint","IMPRINT",FACE,{"disambiguationData":[TD([[makeQuery(id+"F0.imprint","IMPRINT",EDGE,{"derivedFrom":sQuery(id+"F0.wireOp",EDGE,"E325")}),1.0]])]});
            var Q14;
            Q14=makeQuery(id+"F0.imprint","IMPRINT",FACE,{"disambiguationData":[TD([[makeQuery(id+"F0.imprint","IMPRINT",EDGE,{"derivedFrom":sQuery(id+"F0.wireOp",EDGE,"E363")}),1.0]])]});
            var Q15;
            Q15=makeQuery(id+"F0.imprint","IMPRINT",FACE,{"disambiguationData":[TD([[makeQuery(id+"F0.imprint","IMPRINT",EDGE,{"derivedFrom":sQuery(id+"F0.wireOp",EDGE,"E402")}),1.0]])]});
            var Q16;
            Q16=makeQuery(id+"F0.imprint","IMPRINT",FACE,{"disambiguationData":[TD([[makeQuery(id+"F0.imprint","IMPRINT",EDGE,{"derivedFrom":sQuery(id+"F0.wireOp",EDGE,"E414")}),1.0]])]});
            var Q17;
            Q17=makeQuery(id+"F0.imprint","IMPRINT",FACE,{"disambiguationData":[TD([[makeQuery(id+"F0.imprint","IMPRINT",EDGE,{"derivedFrom":sQuery(id+"F0.wireOp",EDGE,"E448")}),1.0]])]});
            var Q18;
            Q18=makeQuery(id+"F0.imprint","IMPRINT",FACE,{"disambiguationData":[TD([[makeQuery(id+"F0.imprint","IMPRINT",EDGE,{"derivedFrom":sQuery(id+"F0.wireOp",EDGE,"E476")}),1.0]])]});
            var Q19;
            Q19=makeQuery(id+"F0.imprint","IMPRINT",FACE,{"disambiguationData":[TD([[makeQuery(id+"F0.imprint","IMPRINT",EDGE,{"derivedFrom":sQuery(id+"F0.wireOp",EDGE,"E498")}),1.0]])]});
            var Q20;
            Q20=makeQuery(id+"F0.imprint","IMPRINT",FACE,{"disambiguationData":[TD([[makeQuery(id+"F0.imprint","IMPRINT",EDGE,{"derivedFrom":sQuery(id+"F0.wireOp",EDGE,"E0")}),1.0]])]});
            var Q21;
            Q21=makeQuery(id+"F0.imprint","IMPRINT",FACE,{"disambiguationData":[TD([[makeQuery(id+"F0.imprint","IMPRINT",EDGE,{"derivedFrom":sQuery(id+"F0.wireOp",EDGE,"E608")}),1.0]])]});
            var Q22;
            Q22=makeQuery(id+"F0.imprint","IMPRINT",FACE,{"disambiguationData":[TD([[makeQuery(id+"F0.imprint","IMPRINT",EDGE,{"derivedFrom":sQuery(id+"F0.wireOp",EDGE,"E510")}),1.0]])]});
            var Q23;
            Q23=makeQuery(id+"F0.imprint","IMPRINT",FACE,{"disambiguationData":[TD([[makeQuery(id+"F0.imprint","IMPRINT",EDGE,{"derivedFrom":sQuery(id+"F0.wireOp",EDGE,"E586")}),1.0]])]});
            var Q24;
            Q24=makeQuery(id+"F0.imprint","IMPRINT",FACE,{"disambiguationData":[TD([[makeQuery(id+"F0.imprint","IMPRINT",EDGE,{"derivedFrom":sQuery(id+"F0.wireOp",EDGE,"E677")}),1.0]])]});
            var Q25;
            Q25=makeQuery(id+"F0.imprint","IMPRINT",FACE,{"disambiguationData":[TD([[makeQuery(id+"F0.imprint","IMPRINT",EDGE,{"derivedFrom":sQuery(id+"F0.wireOp",EDGE,"E225")}),1.0]])]});
            extrude(context, id + "F2", {"entities" : qUnion([Q0, Q1, Q2, Q3, Q4, Q5, Q6, Q7, Q8, Q9, Q10, Q11, Q12, Q13, Q14, Q15, Q16, Q17, Q18, Q19, Q20, Q21, Q22, Q23, Q24, Q25]), "oppositeDirection" : true, "depth" : getVariable(context, 'lh')});
        }
        {
            var Q0;
            Q0=makeQuery(id+"F0.imprint","IMPRINT",FACE,{"disambiguationData":[TD([[makeQuery(id+"F0.imprint","IMPRINT",EDGE,{"derivedFrom":sQuery(id+"F0.wireOp",EDGE,"E608")}),1.0]])]});
            var Q1;
            Q1=makeQuery(id+"F0.imprint","IMPRINT",FACE,{"disambiguationData":[TD([[makeQuery(id+"F0.imprint","IMPRINT",EDGE,{"derivedFrom":sQuery(id+"F0.wireOp",EDGE,"E677")}),1.0]])]});
            var Q2;
            Q2=makeQuery(id+"F0.imprint","IMPRINT",FACE,{"disambiguationData":[TD([[makeQuery(id+"F0.imprint","IMPRINT",EDGE,{"derivedFrom":sQuery(id+"F0.wireOp",EDGE,"E586")}),1.0]])]});
            extrude(context, id + "F3", {"entities" : qUnion([Q0, Q1, Q2]), "depth" : getVariable(context, 'lh')});
        }
        {
            var Q0;
            Q0=makeQuery(id+"F0.imprint","IMPRINT",FACE,{"disambiguationData":[TD([[makeQuery(id+"F0.imprint","IMPRINT",EDGE,{"derivedFrom":sQuery(id+"F0.wireOp",EDGE,"E510")}),1.0]])]});
            extrude(context, id + "F4", {"entities" : qUnion([Q0]), "depth" : 2 * getVariable(context, 'lh')});
        }
        {
            var Q0;
            Q0=makeQuery(id+"F0.imprint","IMPRINT",FACE,{"disambiguationData":[TD([[makeQuery(id+"F0.imprint","IMPRINT",EDGE,{"derivedFrom":sQuery(id+"F0.wireOp",EDGE,"E297")}),1.0]])]});
            var Q1;
            Q1=makeQuery(id+"F0.imprint","IMPRINT",FACE,{"disambiguationData":[TD([[makeQuery(id+"F0.imprint","IMPRINT",EDGE,{"derivedFrom":sQuery(id+"F0.wireOp",EDGE,"E291")}),1.0]])]});
            var Q2;
            Q2=makeQuery(id+"F0.imprint","IMPRINT",FACE,{"disambiguationData":[TD([[makeQuery(id+"F0.imprint","IMPRINT",EDGE,{"derivedFrom":sQuery(id+"F0.wireOp",EDGE,"E275")}),1.0]])]});
            var Q3;
            Q3=makeQuery(id+"F0.imprint","IMPRINT",FACE,{"disambiguationData":[TD([[makeQuery(id+"F0.imprint","IMPRINT",EDGE,{"derivedFrom":sQuery(id+"F0.wireOp",EDGE,"E255")}),1.0]])]});
            var Q4;
            Q4=makeQuery(id+"F0.imprint","IMPRINT",FACE,{"disambiguationData":[TD([[makeQuery(id+"F0.imprint","IMPRINT",EDGE,{"derivedFrom":sQuery(id+"F0.wireOp",EDGE,"E243")}),1.0]])]});
            var Q5;
            Q5=makeQuery(id+"F0.imprint","IMPRINT",FACE,{"disambiguationData":[TD([[makeQuery(id+"F0.imprint","IMPRINT",EDGE,{"derivedFrom":sQuery(id+"F0.wireOp",EDGE,"E235")}),1.0]])]});
            var Q6;
            Q6=makeQuery(id+"F0.imprint","IMPRINT",FACE,{"disambiguationData":[TD([[makeQuery(id+"F0.imprint","IMPRINT",EDGE,{"derivedFrom":sQuery(id+"F0.wireOp",EDGE,"E325")}),1.0]])]});
            var Q7;
            Q7=makeQuery(id+"F0.imprint","IMPRINT",FACE,{"disambiguationData":[TD([[makeQuery(id+"F0.imprint","IMPRINT",EDGE,{"derivedFrom":sQuery(id+"F0.wireOp",EDGE,"E363")}),1.0]])]});
            var Q8;
            Q8=makeQuery(id+"F0.imprint","IMPRINT",FACE,{"disambiguationData":[TD([[makeQuery(id+"F0.imprint","IMPRINT",EDGE,{"derivedFrom":sQuery(id+"F0.wireOp",EDGE,"E402")}),1.0]])]});
            var Q9;
            Q9=makeQuery(id+"F0.imprint","IMPRINT",FACE,{"disambiguationData":[TD([[makeQuery(id+"F0.imprint","IMPRINT",EDGE,{"derivedFrom":sQuery(id+"F0.wireOp",EDGE,"E414")}),1.0]])]});
            var Q10;
            Q10=makeQuery(id+"F0.imprint","IMPRINT",FACE,{"disambiguationData":[TD([[makeQuery(id+"F0.imprint","IMPRINT",EDGE,{"derivedFrom":sQuery(id+"F0.wireOp",EDGE,"E448")}),1.0]])]});
            var Q11;
            Q11=makeQuery(id+"F0.imprint","IMPRINT",FACE,{"disambiguationData":[TD([[makeQuery(id+"F0.imprint","IMPRINT",EDGE,{"derivedFrom":sQuery(id+"F0.wireOp",EDGE,"E476")}),1.0]])]});
            var Q12;
            Q12=makeQuery(id+"F0.imprint","IMPRINT",FACE,{"disambiguationData":[TD([[makeQuery(id+"F0.imprint","IMPRINT",EDGE,{"derivedFrom":sQuery(id+"F0.wireOp",EDGE,"E498")}),1.0]])]});
            var Q13;
            Q13=makeQuery(id+"F0.imprint","IMPRINT",FACE,{"disambiguationData":[TD([[makeQuery(id+"F0.imprint","IMPRINT",EDGE,{"derivedFrom":sQuery(id+"F0.wireOp",EDGE,"E0")}),1.0]])]});
            extrude(context, id + "F5", {"entities" : qUnion([Q0, Q1, Q2, Q3, Q4, Q5, Q6, Q7, Q8, Q9, Q10, Q11, Q12, Q13]), "depth" : 2 * getVariable(context, 'lh')});
        }
        {
            var Q0;
            Q0=makeQuery(id+"F5.opExtrude","CAP_FACE",FACE,{"disambiguationData":[OSD([sQuery(id+"F0.wireOp",EDGE,"E0"),sQuery(id+"F0.wireOp",EDGE,"E1"),sQuery(id+"F0.wireOp",EDGE,"E2"),sQuery(id+"F0.wireOp",EDGE,"E3"),sQuery(id+"F0.wireOp",EDGE,"E4"),sQuery(id+"F0.wireOp",EDGE,"E5"),sQuery(id+"F0.wireOp",EDGE,"E6"),sQuery(id+"F0.wireOp",EDGE,"E7"),sQuery(id+"F0.wireOp",EDGE,"E8"),sQuery(id+"F0.wireOp",EDGE,"E9"),sQuery(id+"F0.wireOp",EDGE,"E10"),sQuery(id+"F0.wireOp",EDGE,"E11"),sQuery(id+"F0.wireOp",EDGE,"E12"),sQuery(id+"F0.wireOp",EDGE,"E13"),sQuery(id+"F0.wireOp",EDGE,"E14"),sQuery(id+"F0.wireOp",EDGE,"E15"),sQuery(id+"F0.wireOp",EDGE,"E16"),sQuery(id+"F0.wireOp",EDGE,"E17"),sQuery(id+"F0.wireOp",EDGE,"E18"),sQuery(id+"F0.wireOp",EDGE,"E19"),sQuery(id+"F0.wireOp",EDGE,"E20"),sQuery(id+"F0.wireOp",EDGE,"E21"),sQuery(id+"F0.wireOp",EDGE,"E22"),sQuery(id+"F0.wireOp",EDGE,"E23"),sQuery(id+"F0.wireOp",EDGE,"E24"),sQuery(id+"F0.wireOp",EDGE,"E25"),sQuery(id+"F0.wireOp",EDGE,"E26"),sQuery(id+"F0.wireOp",EDGE,"E27"),sQuery(id+"F0.wireOp",EDGE,"E28"),sQuery(id+"F0.wireOp",EDGE,"E29"),sQuery(id+"F0.wireOp",EDGE,"E30"),sQuery(id+"F0.wireOp",EDGE,"E31"),sQuery(id+"F0.wireOp",EDGE,"E32"),sQuery(id+"F0.wireOp",EDGE,"E33"),sQuery(id+"F0.wireOp",EDGE,"E34"),sQuery(id+"F0.wireOp",EDGE,"E35"),sQuery(id+"F0.wireOp",EDGE,"E36"),sQuery(id+"F0.wireOp",EDGE,"E37"),sQuery(id+"F0.wireOp",EDGE,"E38"),sQuery(id+"F0.wireOp",EDGE,"E39"),sQuery(id+"F0.wireOp",EDGE,"E40"),sQuery(id+"F0.wireOp",EDGE,"E41"),sQuery(id+"F0.wireOp",EDGE,"E42"),sQuery(id+"F0.wireOp",EDGE,"E43"),sQuery(id+"F0.wireOp",EDGE,"E44"),sQuery(id+"F0.wireOp",EDGE,"E45"),sQuery(id+"F0.wireOp",EDGE,"E46"),sQuery(id+"F0.wireOp",EDGE,"E47"),sQuery(id+"F0.wireOp",EDGE,"E48"),sQuery(id+"F0.wireOp",EDGE,"E49"),sQuery(id+"F0.wireOp",EDGE,"E50"),sQuery(id+"F0.wireOp",EDGE,"E51"),sQuery(id+"F0.wireOp",EDGE,"E52"),sQuery(id+"F0.wireOp",EDGE,"E53"),sQuery(id+"F0.wireOp",EDGE,"E54"),sQuery(id+"F0.wireOp",EDGE,"E55"),sQuery(id+"F0.wireOp",EDGE,"E56"),sQuery(id+"F0.wireOp",EDGE,"E57"),sQuery(id+"F0.wireOp",EDGE,"E58"),sQuery(id+"F0.wireOp",EDGE,"E59"),sQuery(id+"F0.wireOp",EDGE,"E60"),sQuery(id+"F0.wireOp",EDGE,"E61"),sQuery(id+"F0.wireOp",EDGE,"E62"),sQuery(id+"F0.wireOp",EDGE,"E63"),sQuery(id+"F0.wireOp",EDGE,"E64"),sQuery(id+"F0.wireOp",EDGE,"E65"),sQuery(id+"F0.wireOp",EDGE,"E66"),sQuery(id+"F0.wireOp",EDGE,"E67"),sQuery(id+"F0.wireOp",EDGE,"E68"),sQuery(id+"F0.wireOp",EDGE,"E69"),sQuery(id+"F0.wireOp",EDGE,"E70"),sQuery(id+"F0.wireOp",EDGE,"E71"),sQuery(id+"F0.wireOp",EDGE,"E72"),sQuery(id+"F0.wireOp",EDGE,"E73"),sQuery(id+"F0.wireOp",EDGE,"E74"),sQuery(id+"F0.wireOp",EDGE,"E75"),sQuery(id+"F0.wireOp",EDGE,"E76"),sQuery(id+"F0.wireOp",EDGE,"E77"),sQuery(id+"F0.wireOp",EDGE,"E78"),sQuery(id+"F0.wireOp",EDGE,"E79"),sQuery(id+"F0.wireOp",EDGE,"E80"),sQuery(id+"F0.wireOp",EDGE,"E81"),sQuery(id+"F0.wireOp",EDGE,"E82"),sQuery(id+"F0.wireOp",EDGE,"E83"),sQuery(id+"F0.wireOp",EDGE,"E84"),sQuery(id+"F0.wireOp",EDGE,"E85"),sQuery(id+"F0.wireOp",EDGE,"E86"),sQuery(id+"F0.wireOp",EDGE,"E87"),sQuery(id+"F0.wireOp",EDGE,"E88"),sQuery(id+"F0.wireOp",EDGE,"E89"),sQuery(id+"F0.wireOp",EDGE,"E90"),sQuery(id+"F0.wireOp",EDGE,"E91"),sQuery(id+"F0.wireOp",EDGE,"E92"),sQuery(id+"F0.wireOp",EDGE,"E93"),sQuery(id+"F0.wireOp",EDGE,"E94"),sQuery(id+"F0.wireOp",EDGE,"E95"),sQuery(id+"F0.wireOp",EDGE,"E96"),sQuery(id+"F0.wireOp",EDGE,"E97"),sQuery(id+"F0.wireOp",EDGE,"E98"),sQuery(id+"F0.wireOp",EDGE,"E99"),sQuery(id+"F0.wireOp",EDGE,"E100"),sQuery(id+"F0.wireOp",EDGE,"E101"),sQuery(id+"F0.wireOp",EDGE,"E102"),sQuery(id+"F0.wireOp",EDGE,"E103"),sQuery(id+"F0.wireOp",EDGE,"E104"),sQuery(id+"F0.wireOp",EDGE,"E105"),sQuery(id+"F0.wireOp",EDGE,"E106"),sQuery(id+"F0.wireOp",EDGE,"E107"),sQuery(id+"F0.wireOp",EDGE,"E108"),sQuery(id+"F0.wireOp",EDGE,"E109"),sQuery(id+"F0.wireOp",EDGE,"E110"),sQuery(id+"F0.wireOp",EDGE,"E111"),sQuery(id+"F0.wireOp",EDGE,"E112"),sQuery(id+"F0.wireOp",EDGE,"E113"),sQuery(id+"F0.wireOp",EDGE,"E114"),sQuery(id+"F0.wireOp",EDGE,"E115"),sQuery(id+"F0.wireOp",EDGE,"E116"),sQuery(id+"F0.wireOp",EDGE,"E117"),sQuery(id+"F0.wireOp",EDGE,"E118"),sQuery(id+"F0.wireOp",EDGE,"E119"),sQuery(id+"F0.wireOp",EDGE,"E120"),sQuery(id+"F0.wireOp",EDGE,"E121"),sQuery(id+"F0.wireOp",EDGE,"E122"),sQuery(id+"F0.wireOp",EDGE,"E123"),sQuery(id+"F0.wireOp",EDGE,"E124"),sQuery(id+"F0.wireOp",EDGE,"E125"),sQuery(id+"F0.wireOp",EDGE,"E126"),sQuery(id+"F0.wireOp",EDGE,"E127"),sQuery(id+"F0.wireOp",EDGE,"E128"),sQuery(id+"F0.wireOp",EDGE,"E129"),sQuery(id+"F0.wireOp",EDGE,"E130"),sQuery(id+"F0.wireOp",EDGE,"E131"),sQuery(id+"F0.wireOp",EDGE,"E132"),sQuery(id+"F0.wireOp",EDGE,"E133"),sQuery(id+"F0.wireOp",EDGE,"E134"),sQuery(id+"F0.wireOp",EDGE,"E135"),sQuery(id+"F0.wireOp",EDGE,"E136"),sQuery(id+"F0.wireOp",EDGE,"E137"),sQuery(id+"F0.wireOp",EDGE,"E138"),sQuery(id+"F0.wireOp",EDGE,"E139"),sQuery(id+"F0.wireOp",EDGE,"E140"),sQuery(id+"F0.wireOp",EDGE,"E141"),sQuery(id+"F0.wireOp",EDGE,"E142"),sQuery(id+"F0.wireOp",EDGE,"E143"),sQuery(id+"F0.wireOp",EDGE,"E144"),sQuery(id+"F0.wireOp",EDGE,"E145"),sQuery(id+"F0.wireOp",EDGE,"E146"),sQuery(id+"F0.wireOp",EDGE,"E147"),sQuery(id+"F0.wireOp",EDGE,"E148"),sQuery(id+"F0.wireOp",EDGE,"E149"),sQuery(id+"F0.wireOp",EDGE,"E150"),sQuery(id+"F0.wireOp",EDGE,"E151"),sQuery(id+"F0.wireOp",EDGE,"E152"),sQuery(id+"F0.wireOp",EDGE,"E153"),sQuery(id+"F0.wireOp",EDGE,"E154"),sQuery(id+"F0.wireOp",EDGE,"E155"),sQuery(id+"F0.wireOp",EDGE,"E156"),sQuery(id+"F0.wireOp",EDGE,"E157"),sQuery(id+"F0.wireOp",EDGE,"E158"),sQuery(id+"F0.wireOp",EDGE,"E159"),sQuery(id+"F0.wireOp",EDGE,"E160"),sQuery(id+"F0.wireOp",EDGE,"E161"),sQuery(id+"F0.wireOp",EDGE,"E162"),sQuery(id+"F0.wireOp",EDGE,"E163"),sQuery(id+"F0.wireOp",EDGE,"E164"),sQuery(id+"F0.wireOp",EDGE,"E165"),sQuery(id+"F0.wireOp",EDGE,"E166"),sQuery(id+"F0.wireOp",EDGE,"E167"),sQuery(id+"F0.wireOp",EDGE,"E168"),sQuery(id+"F0.wireOp",EDGE,"E169"),sQuery(id+"F0.wireOp",EDGE,"E170"),sQuery(id+"F0.wireOp",EDGE,"E171"),sQuery(id+"F0.wireOp",EDGE,"E172"),sQuery(id+"F0.wireOp",EDGE,"E173"),sQuery(id+"F0.wireOp",EDGE,"E174"),sQuery(id+"F0.wireOp",EDGE,"E175"),sQuery(id+"F0.wireOp",EDGE,"E176"),sQuery(id+"F0.wireOp",EDGE,"E177"),sQuery(id+"F0.wireOp",EDGE,"E178"),sQuery(id+"F0.wireOp",EDGE,"E179"),sQuery(id+"F0.wireOp",EDGE,"E180"),sQuery(id+"F0.wireOp",EDGE,"E181"),sQuery(id+"F0.wireOp",EDGE,"E182"),sQuery(id+"F0.wireOp",EDGE,"E183"),sQuery(id+"F0.wireOp",EDGE,"E184"),sQuery(id+"F0.wireOp",EDGE,"E185"),sQuery(id+"F0.wireOp",EDGE,"E186"),sQuery(id+"F0.wireOp",EDGE,"E187"),sQuery(id+"F0.wireOp",EDGE,"E188"),sQuery(id+"F0.wireOp",EDGE,"E189"),sQuery(id+"F0.wireOp",EDGE,"E190"),sQuery(id+"F0.wireOp",EDGE,"E191"),sQuery(id+"F0.wireOp",EDGE,"E192"),sQuery(id+"F0.wireOp",EDGE,"E193"),sQuery(id+"F0.wireOp",EDGE,"E194"),sQuery(id+"F0.wireOp",EDGE,"E195"),sQuery(id+"F0.wireOp",EDGE,"E196"),sQuery(id+"F0.wireOp",EDGE,"E197"),sQuery(id+"F0.wireOp",EDGE,"E198"),sQuery(id+"F0.wireOp",EDGE,"E199"),sQuery(id+"F0.wireOp",EDGE,"E200"),sQuery(id+"F0.wireOp",EDGE,"E201"),sQuery(id+"F0.wireOp",EDGE,"E202"),sQuery(id+"F0.wireOp",EDGE,"E203"),sQuery(id+"F0.wireOp",EDGE,"E204"),sQuery(id+"F0.wireOp",EDGE,"E205"),sQuery(id+"F0.wireOp",EDGE,"E206"),sQuery(id+"F0.wireOp",EDGE,"E207"),sQuery(id+"F0.wireOp",EDGE,"E208"),sQuery(id+"F0.wireOp",EDGE,"E209"),sQuery(id+"F0.wireOp",EDGE,"E210"),sQuery(id+"F0.wireOp",EDGE,"E211"),sQuery(id+"F0.wireOp",EDGE,"E212"),sQuery(id+"F0.wireOp",EDGE,"E213"),sQuery(id+"F0.wireOp",EDGE,"E214"),sQuery(id+"F0.wireOp",EDGE,"E215"),sQuery(id+"F0.wireOp",EDGE,"E216"),sQuery(id+"F0.wireOp",EDGE,"E217"),sQuery(id+"F0.wireOp",EDGE,"E218"),sQuery(id+"F0.wireOp",EDGE,"E219"),sQuery(id+"F0.wireOp",EDGE,"E220"),sQuery(id+"F0.wireOp",EDGE,"E221"),sQuery(id+"F0.wireOp",EDGE,"E222"),sQuery(id+"F0.wireOp",EDGE,"E223"),sQuery(id+"F0.wireOp",EDGE,"E224"),sQuery(id+"F0.wireOp",EDGE,"E225"),sQuery(id+"F0.wireOp",EDGE,"E226"),sQuery(id+"F0.wireOp",EDGE,"E227"),sQuery(id+"F0.wireOp",EDGE,"E228"),sQuery(id+"F0.wireOp",EDGE,"E229"),sQuery(id+"F0.wireOp",EDGE,"E230"),sQuery(id+"F0.wireOp",EDGE,"E231"),sQuery(id+"F0.wireOp",EDGE,"E232"),sQuery(id+"F0.wireOp",EDGE,"E233"),sQuery(id+"F0.wireOp",EDGE,"E234"),sQuery(id+"F0.wireOp",EDGE,"E510"),sQuery(id+"F0.wireOp",EDGE,"E511"),sQuery(id+"F0.wireOp",EDGE,"E512"),sQuery(id+"F0.wireOp",EDGE,"E513"),sQuery(id+"F0.wireOp",EDGE,"E514"),sQuery(id+"F0.wireOp",EDGE,"E515"),sQuery(id+"F0.wireOp",EDGE,"E516"),sQuery(id+"F0.wireOp",EDGE,"E517"),sQuery(id+"F0.wireOp",EDGE,"E518"),sQuery(id+"F0.wireOp",EDGE,"E519"),sQuery(id+"F0.wireOp",EDGE,"E520"),sQuery(id+"F0.wireOp",EDGE,"E521"),sQuery(id+"F0.wireOp",EDGE,"E522"),sQuery(id+"F0.wireOp",EDGE,"E523"),sQuery(id+"F0.wireOp",EDGE,"E524"),sQuery(id+"F0.wireOp",EDGE,"E525"),sQuery(id+"F0.wireOp",EDGE,"E526"),sQuery(id+"F0.wireOp",EDGE,"E527"),sQuery(id+"F0.wireOp",EDGE,"E528"),sQuery(id+"F0.wireOp",EDGE,"E529"),sQuery(id+"F0.wireOp",EDGE,"E530"),sQuery(id+"F0.wireOp",EDGE,"E531"),sQuery(id+"F0.wireOp",EDGE,"E532"),sQuery(id+"F0.wireOp",EDGE,"E533"),sQuery(id+"F0.wireOp",EDGE,"E534"),sQuery(id+"F0.wireOp",EDGE,"E535"),sQuery(id+"F0.wireOp",EDGE,"E536"),sQuery(id+"F0.wireOp",EDGE,"E537"),sQuery(id+"F0.wireOp",EDGE,"E538"),sQuery(id+"F0.wireOp",EDGE,"E539"),sQuery(id+"F0.wireOp",EDGE,"E540"),sQuery(id+"F0.wireOp",EDGE,"E541"),sQuery(id+"F0.wireOp",EDGE,"E542"),sQuery(id+"F0.wireOp",EDGE,"E543"),sQuery(id+"F0.wireOp",EDGE,"E544"),sQuery(id+"F0.wireOp",EDGE,"E545"),sQuery(id+"F0.wireOp",EDGE,"E546"),sQuery(id+"F0.wireOp",EDGE,"E547"),sQuery(id+"F0.wireOp",EDGE,"E548"),sQuery(id+"F0.wireOp",EDGE,"E549"),sQuery(id+"F0.wireOp",EDGE,"E550"),sQuery(id+"F0.wireOp",EDGE,"E551"),sQuery(id+"F0.wireOp",EDGE,"E552"),sQuery(id+"F0.wireOp",EDGE,"E553"),sQuery(id+"F0.wireOp",EDGE,"E554"),sQuery(id+"F0.wireOp",EDGE,"E555"),sQuery(id+"F0.wireOp",EDGE,"E556"),sQuery(id+"F0.wireOp",EDGE,"E557"),sQuery(id+"F0.wireOp",EDGE,"E558"),sQuery(id+"F0.wireOp",EDGE,"E559"),sQuery(id+"F0.wireOp",EDGE,"E560"),sQuery(id+"F0.wireOp",EDGE,"E561"),sQuery(id+"F0.wireOp",EDGE,"E562"),sQuery(id+"F0.wireOp",EDGE,"E563"),sQuery(id+"F0.wireOp",EDGE,"E564"),sQuery(id+"F0.wireOp",EDGE,"E565"),sQuery(id+"F0.wireOp",EDGE,"E566"),sQuery(id+"F0.wireOp",EDGE,"E567"),sQuery(id+"F0.wireOp",EDGE,"E568"),sQuery(id+"F0.wireOp",EDGE,"E569"),sQuery(id+"F0.wireOp",EDGE,"E570"),sQuery(id+"F0.wireOp",EDGE,"E571"),sQuery(id+"F0.wireOp",EDGE,"E572"),sQuery(id+"F0.wireOp",EDGE,"E573"),sQuery(id+"F0.wireOp",EDGE,"E574"),sQuery(id+"F0.wireOp",EDGE,"E575"),sQuery(id+"F0.wireOp",EDGE,"E576"),sQuery(id+"F0.wireOp",EDGE,"E577"),sQuery(id+"F0.wireOp",EDGE,"E578"),sQuery(id+"F0.wireOp",EDGE,"E579"),sQuery(id+"F0.wireOp",EDGE,"E580"),sQuery(id+"F0.wireOp",EDGE,"E581"),sQuery(id+"F0.wireOp",EDGE,"E582"),sQuery(id+"F0.wireOp",EDGE,"E583"),sQuery(id+"F0.wireOp",EDGE,"E584"),sQuery(id+"F0.wireOp",EDGE,"E585"),sQuery(id+"F0.wireOp",EDGE,"E586"),sQuery(id+"F0.wireOp",EDGE,"E587"),sQuery(id+"F0.wireOp",EDGE,"E588"),sQuery(id+"F0.wireOp",EDGE,"E589"),sQuery(id+"F0.wireOp",EDGE,"E590"),sQuery(id+"F0.wireOp",EDGE,"E591"),sQuery(id+"F0.wireOp",EDGE,"E592"),sQuery(id+"F0.wireOp",EDGE,"E593"),sQuery(id+"F0.wireOp",EDGE,"E594"),sQuery(id+"F0.wireOp",EDGE,"E595"),sQuery(id+"F0.wireOp",EDGE,"E596"),sQuery(id+"F0.wireOp",EDGE,"E597"),sQuery(id+"F0.wireOp",EDGE,"E598"),sQuery(id+"F0.wireOp",EDGE,"E599"),sQuery(id+"F0.wireOp",EDGE,"E600"),sQuery(id+"F0.wireOp",EDGE,"E601"),sQuery(id+"F0.wireOp",EDGE,"E602"),sQuery(id+"F0.wireOp",EDGE,"E603"),sQuery(id+"F0.wireOp",EDGE,"E604"),sQuery(id+"F0.wireOp",EDGE,"E605"),sQuery(id+"F0.wireOp",EDGE,"E606"),sQuery(id+"F0.wireOp",EDGE,"E607"),sQuery(id+"F0.wireOp",EDGE,"E608"),sQuery(id+"F0.wireOp",EDGE,"E609"),sQuery(id+"F0.wireOp",EDGE,"E610"),sQuery(id+"F0.wireOp",EDGE,"E611"),sQuery(id+"F0.wireOp",EDGE,"E612"),sQuery(id+"F0.wireOp",EDGE,"E613"),sQuery(id+"F0.wireOp",EDGE,"E614"),sQuery(id+"F0.wireOp",EDGE,"E615"),sQuery(id+"F0.wireOp",EDGE,"E616"),sQuery(id+"F0.wireOp",EDGE,"E617"),sQuery(id+"F0.wireOp",EDGE,"E618"),sQuery(id+"F0.wireOp",EDGE,"E619"),sQuery(id+"F0.wireOp",EDGE,"E620"),sQuery(id+"F0.wireOp",EDGE,"E621"),sQuery(id+"F0.wireOp",EDGE,"E622"),sQuery(id+"F0.wireOp",EDGE,"E623"),sQuery(id+"F0.wireOp",EDGE,"E624"),sQuery(id+"F0.wireOp",EDGE,"E625"),sQuery(id+"F0.wireOp",EDGE,"E626"),sQuery(id+"F0.wireOp",EDGE,"E627"),sQuery(id+"F0.wireOp",EDGE,"E628"),sQuery(id+"F0.wireOp",EDGE,"E629"),sQuery(id+"F0.wireOp",EDGE,"E630"),sQuery(id+"F0.wireOp",EDGE,"E631"),sQuery(id+"F0.wireOp",EDGE,"E632"),sQuery(id+"F0.wireOp",EDGE,"E633"),sQuery(id+"F0.wireOp",EDGE,"E634"),sQuery(id+"F0.wireOp",EDGE,"E635"),sQuery(id+"F0.wireOp",EDGE,"E636"),sQuery(id+"F0.wireOp",EDGE,"E637"),sQuery(id+"F0.wireOp",EDGE,"E638"),sQuery(id+"F0.wireOp",EDGE,"E639"),sQuery(id+"F0.wireOp",EDGE,"E640"),sQuery(id+"F0.wireOp",EDGE,"E641"),sQuery(id+"F0.wireOp",EDGE,"E642"),sQuery(id+"F0.wireOp",EDGE,"E643"),sQuery(id+"F0.wireOp",EDGE,"E644"),sQuery(id+"F0.wireOp",EDGE,"E645"),sQuery(id+"F0.wireOp",EDGE,"E646"),sQuery(id+"F0.wireOp",EDGE,"E647"),sQuery(id+"F0.wireOp",EDGE,"E648"),sQuery(id+"F0.wireOp",EDGE,"E649"),sQuery(id+"F0.wireOp",EDGE,"E650"),sQuery(id+"F0.wireOp",EDGE,"E651"),sQuery(id+"F0.wireOp",EDGE,"E652"),sQuery(id+"F0.wireOp",EDGE,"E653"),sQuery(id+"F0.wireOp",EDGE,"E654"),sQuery(id+"F0.wireOp",EDGE,"E655"),sQuery(id+"F0.wireOp",EDGE,"E656"),sQuery(id+"F0.wireOp",EDGE,"E657"),sQuery(id+"F0.wireOp",EDGE,"E658"),sQuery(id+"F0.wireOp",EDGE,"E659"),sQuery(id+"F0.wireOp",EDGE,"E660"),sQuery(id+"F0.wireOp",EDGE,"E661"),sQuery(id+"F0.wireOp",EDGE,"E662"),sQuery(id+"F0.wireOp",EDGE,"E663"),sQuery(id+"F0.wireOp",EDGE,"E664"),sQuery(id+"F0.wireOp",EDGE,"E665"),sQuery(id+"F0.wireOp",EDGE,"E666"),sQuery(id+"F0.wireOp",EDGE,"E667"),sQuery(id+"F0.wireOp",EDGE,"E668"),sQuery(id+"F0.wireOp",EDGE,"E669"),sQuery(id+"F0.wireOp",EDGE,"E670"),sQuery(id+"F0.wireOp",EDGE,"E671"),sQuery(id+"F0.wireOp",EDGE,"E672"),sQuery(id+"F0.wireOp",EDGE,"E673"),sQuery(id+"F0.wireOp",EDGE,"E674"),sQuery(id+"F0.wireOp",EDGE,"E675"),sQuery(id+"F0.wireOp",EDGE,"E676"),sQuery(id+"F0.wireOp",EDGE,"E677"),sQuery(id+"F0.wireOp",EDGE,"E678"),sQuery(id+"F0.wireOp",EDGE,"E679"),sQuery(id+"F0.wireOp",EDGE,"E680"),sQuery(id+"F0.wireOp",EDGE,"E681"),sQuery(id+"F0.wireOp",EDGE,"E682"),sQuery(id+"F0.wireOp",EDGE,"E683"),sQuery(id+"F0.wireOp",EDGE,"E684"),sQuery(id+"F0.wireOp",EDGE,"E685"),sQuery(id+"F0.wireOp",EDGE,"E686"),sQuery(id+"F0.wireOp",EDGE,"E687"),sQuery(id+"F0.wireOp",EDGE,"E688"),sQuery(id+"F0.wireOp",EDGE,"E689"),sQuery(id+"F0.wireOp",EDGE,"E690"),sQuery(id+"F0.wireOp",EDGE,"E691"),sQuery(id+"F0.wireOp",EDGE,"E692"),sQuery(id+"F0.wireOp",EDGE,"E693"),sQuery(id+"F0.wireOp",EDGE,"E694"),sQuery(id+"F0.wireOp",EDGE,"E695"),sQuery(id+"F0.wireOp",EDGE,"E696"),sQuery(id+"F0.wireOp",EDGE,"E697"),sQuery(id+"F0.wireOp",EDGE,"E698")])],"isStart":false});
            var sketch = newSketch(context, id + "F6", { "sketchPlane" : qUnion([Q0])});
            skLineSegment(sketch, "E726.0", {"start": v(-21.58, 2.54) * mm, "end": v(-20.1, 2.75) * mm});
            skLineSegment(sketch, "E727.0", {"start": v(-16.3, 5.66) * mm, "end": v(-21.58, 2.54) * mm});
            skLineSegment(sketch, "E728.0", {"start": v(-10.6, 8.1) * mm, "end": v(-16.3, 5.66) * mm});
            skLineSegment(sketch, "E729.0", {"start": v(-4.68, 9.9) * mm, "end": v(-10.6, 8.1) * mm});
            skLineSegment(sketch, "E730.0", {"start": v(1.35, 11.03) * mm, "end": v(-4.68, 9.9) * mm});
            skLineSegment(sketch, "E731.0", {"start": v(3.48, 11.26) * mm, "end": v(1.35, 11.03) * mm});
            skLineSegment(sketch, "E732.0", {"start": v(5.63, 11.37) * mm, "end": v(3.48, 11.26) * mm});
            skLineSegment(sketch, "E733.0", {"start": v(6.12, 11.6) * mm, "end": v(5.63, 11.37) * mm});
            skLineSegment(sketch, "E734.0", {"start": v(9.04, 14.86) * mm, "end": v(6.12, 11.6) * mm});
            skLineSegment(sketch, "E735.0", {"start": v(12, 17.84) * mm, "end": v(9.04, 14.86) * mm});
            skLineSegment(sketch, "E736.0", {"start": v(15.11, 20.66) * mm, "end": v(12, 17.84) * mm});
            skLineSegment(sketch, "E737.0", {"start": v(18.5, 23.42) * mm, "end": v(15.11, 20.66) * mm});
            skLineSegment(sketch, "E738.0", {"start": v(21.35, 25.62) * mm, "end": v(18.51, 23.43) * mm});
            skLineSegment(sketch, "E739.0", {"start": v(24.25, 27.75) * mm, "end": v(21.35, 25.62) * mm});
            skLineSegment(sketch, "E740.0", {"start": v(26.94, 29.54) * mm, "end": v(24.25, 27.75) * mm});
            skLineSegment(sketch, "E741.0", {"start": v(29.74, 31.16) * mm, "end": v(26.94, 29.54) * mm});
            skLineSegment(sketch, "E742.0", {"start": v(32.68, 32.6) * mm, "end": v(29.74, 31.16) * mm});
            skLineSegment(sketch, "E743.0", {"start": v(35.72, 33.83) * mm, "end": v(32.68, 32.6) * mm});
            skLineSegment(sketch, "E744.0", {"start": v(38.46, 34.76) * mm, "end": v(35.72, 33.83) * mm});
            skLineSegment(sketch, "E745.0", {"start": v(41.24, 35.58) * mm, "end": v(38.46, 34.76) * mm});
            skLineSegment(sketch, "E746.0", {"start": v(43.61, 36.18) * mm, "end": v(41.24, 35.58) * mm});
            skLineSegment(sketch, "E747.0", {"start": v(46.26, 36.72) * mm, "end": v(43.61, 36.18) * mm});
            skLineSegment(sketch, "E748.0", {"start": v(48.82, 37.06) * mm, "end": v(46.26, 36.72) * mm});
            skLineSegment(sketch, "E749.0", {"start": v(50.93, 37.06) * mm, "end": v(48.82, 37.06) * mm});
            skLineSegment(sketch, "E750.0", {"start": v(51.57, 36.92) * mm, "end": v(50.93, 37.06) * mm});
            skLineSegment(sketch, "E751.0", {"start": v(51.82, 36.77) * mm, "end": v(51.57, 36.92) * mm});
            skLineSegment(sketch, "E752.0", {"start": v(51.9, 36.52) * mm, "end": v(51.82, 36.77) * mm});
            skLineSegment(sketch, "E753.0", {"start": v(51.76, 35.17) * mm, "end": v(51.9, 36.52) * mm});
            skLineSegment(sketch, "E754.0", {"start": v(51.27, 33.57) * mm, "end": v(51.76, 35.17) * mm});
            skLineSegment(sketch, "E755.0", {"start": v(50.67, 32.07) * mm, "end": v(51.27, 33.57) * mm});
            skLineSegment(sketch, "E756.0", {"start": v(50.2, 31.03) * mm, "end": v(50.67, 32.07) * mm});
            skLineSegment(sketch, "E757.0", {"start": v(49.13, 28.9) * mm, "end": v(50.2, 31.03) * mm});
            skLineSegment(sketch, "E758.0", {"start": v(47.98, 26.83) * mm, "end": v(49.13, 28.9) * mm});
            skLineSegment(sketch, "E759.0", {"start": v(44.3, 21.13) * mm, "end": v(47.98, 26.83) * mm});
            skLineSegment(sketch, "E760.0", {"start": v(39.94, 15.97) * mm, "end": v(44.3, 21.13) * mm});
            skLineSegment(sketch, "E761.0", {"start": v(37.58, 13.71) * mm, "end": v(39.94, 15.97) * mm});
            skLineSegment(sketch, "E762.0", {"start": v(35.1, 11.6) * mm, "end": v(37.58, 13.71) * mm});
            skLineSegment(sketch, "E763.0", {"start": v(32.77, 9.76) * mm, "end": v(35.1, 11.6) * mm});
            skLineSegment(sketch, "E764.0", {"start": v(30.42, 7.95) * mm, "end": v(32.77, 9.76) * mm});
            skLineSegment(sketch, "E765.0", {"start": v(26.88, 5.38) * mm, "end": v(30.42, 7.95) * mm});
            skLineSegment(sketch, "E766.0", {"start": v(23.36, 3.09) * mm, "end": v(26.88, 5.38) * mm});
            skLineSegment(sketch, "E767.0", {"start": v(19.72, 0.99) * mm, "end": v(23.36, 3.09) * mm});
            skLineSegment(sketch, "E768.0", {"start": v(15.83, -1) * mm, "end": v(19.72, 0.99) * mm});
            skLineSegment(sketch, "E769.0", {"start": v(15.48, -1.42) * mm, "end": v(15.83, -1) * mm});
            skLineSegment(sketch, "E770.0", {"start": v(14.54, -4.24) * mm, "end": v(15.48, -1.42) * mm});
            skLineSegment(sketch, "E771.0", {"start": v(13.4, -6.99) * mm, "end": v(14.54, -4.24) * mm});
            skLineSegment(sketch, "E772.0", {"start": v(10.46, -12.7) * mm, "end": v(13.4, -6.99) * mm});
            skLineSegment(sketch, "E773.0", {"start": v(6.88, -18.07) * mm, "end": v(10.46, -12.7) * mm});
            skLineSegment(sketch, "E774.0", {"start": v(3.65, -21.96) * mm, "end": v(6.88, -18.07) * mm});
            skLineSegment(sketch, "E775.0", {"start": v(0, -25.46) * mm, "end": v(3.65, -21.96) * mm});
            skLineSegment(sketch, "E776.0", {"start": v(1.3, -22.01) * mm, "end": v(0, -25.46) * mm});
            skLineSegment(sketch, "E777.0", {"start": v(2.07, -18.37) * mm, "end": v(1.3, -22.01) * mm});
            skLineSegment(sketch, "E778.0", {"start": v(2.14, -16.14) * mm, "end": v(2.07, -18.37) * mm});
            skLineSegment(sketch, "E779.0", {"start": v(1.77, -13.95) * mm, "end": v(2.14, -16.14) * mm});
            skLineSegment(sketch, "E780.0", {"start": v(1.02, -12.07) * mm, "end": v(1.77, -13.95) * mm});
            skLineSegment(sketch, "E781.0", {"start": v(-0.16, -10.42) * mm, "end": v(1.02, -12.07) * mm});
            skLineSegment(sketch, "E782.0", {"start": v(-0.47, -10.08) * mm, "end": v(-0.16, -10.42) * mm});
            skLineSegment(sketch, "E783.0", {"start": v(-4.16, -11.58) * mm, "end": v(-0.47, -10.08) * mm});
            skLineSegment(sketch, "E784.0", {"start": v(-5.98, -12.3) * mm, "end": v(-4.16, -11.58) * mm});
            skLineSegment(sketch, "E785.0", {"start": v(-7.82, -12.95) * mm, "end": v(-5.98, -12.3) * mm});
            skLineSegment(sketch, "E786.0", {"start": v(-8.34, -13.02) * mm, "end": v(-7.82, -12.95) * mm});
            skLineSegment(sketch, "E787.0", {"start": v(-8.8, -12.85) * mm, "end": v(-8.34, -13.02) * mm});
            skLineSegment(sketch, "E788.0", {"start": v(-11.61, -9.18) * mm, "end": v(-8.8, -12.85) * mm});
            skLineSegment(sketch, "E789.0", {"start": v(-11.67, -8.68) * mm, "end": v(-11.61, -9.18) * mm});
            skLineSegment(sketch, "E790.0", {"start": v(-11.47, -8.2) * mm, "end": v(-11.67, -8.68) * mm});
            skLineSegment(sketch, "E791.0", {"start": v(-10.24, -6.41) * mm, "end": v(-11.47, -8.2) * mm});
            skLineSegment(sketch, "E792.0", {"start": v(-8.95, -4.66) * mm, "end": v(-10.24, -6.41) * mm});
            skLineSegment(sketch, "E793.0", {"start": v(-6.82, -1.84) * mm, "end": v(-8.95, -4.66) * mm});
            skLineSegment(sketch, "E794.0", {"start": v(-8.7, 0.44) * mm, "end": v(-7.08, -1.45) * mm});
            skLineSegment(sketch, "E795.0", {"start": v(-7.08, -1.45) * mm, "end": v(-6.82, -1.84) * mm});
            skLineSegment(sketch, "E796.0", {"start": v(-10.83, 1.75) * mm, "end": v(-8.7, 0.44) * mm});
            skLineSegment(sketch, "E797.0", {"start": v(-12.95, 2.5) * mm, "end": v(-10.83, 1.75) * mm});
            skLineSegment(sketch, "E798.0", {"start": v(-15.18, 2.86) * mm, "end": v(-12.95, 2.5) * mm});
            skLineSegment(sketch, "E799.0", {"start": v(-17.64, 2.95) * mm, "end": v(-15.18, 2.86) * mm});
            skLineSegment(sketch, "E800.0", {"start": v(-20.1, 2.75) * mm, "end": v(-17.64, 2.95) * mm});
            skLineSegment(sketch, "E801.0", {"start": v(-10.04, -6.56) * mm, "end": v(-11.26, -8.35) * mm});
            skLineSegment(sketch, "E801.1", {"start": v(-8.75, -4.81) * mm, "end": v(-10.04, -6.56) * mm});
            skLineSegment(sketch, "E801.2", {"start": v(-6.51, -1.85) * mm, "end": v(-8.75, -4.81) * mm});
            skLineSegment(sketch, "E801.3", {"start": v(-6.88, -1.3) * mm, "end": v(-6.51, -1.85) * mm});
            skLineSegment(sketch, "E801.4", {"start": v(-8.55, 0.63) * mm, "end": v(-6.88, -1.3) * mm});
            skLineSegment(sketch, "E801.5", {"start": v(-10.52, 7.87) * mm, "end": v(-16.18, 5.43) * mm});
            skLineSegment(sketch, "E801.6", {"start": v(-4.62, 9.65) * mm, "end": v(-10.52, 7.87) * mm});
            skLineSegment(sketch, "E801.7", {"start": v(1.38, 10.78) * mm, "end": v(-4.62, 9.65) * mm});
            skLineSegment(sketch, "E801.8", {"start": v(3.5, 11.01) * mm, "end": v(1.38, 10.78) * mm});
            skLineSegment(sketch, "E801.9", {"start": v(-16.18, 5.43) * mm, "end": v(-20.33, 2.99) * mm});
            skLineSegment(sketch, "E801.10", {"start": v(-20.33, 2.99) * mm, "end": v(-17.65, 3.2) * mm});
            skLineSegment(sketch, "E801.11", {"start": v(-17.65, 3.2) * mm, "end": v(-15.15, 3.1) * mm});
            skLineSegment(sketch, "E801.12", {"start": v(-15.15, 3.1) * mm, "end": v(-12.9, 2.74) * mm});
            skLineSegment(sketch, "E801.13", {"start": v(-12.9, 2.74) * mm, "end": v(-10.72, 1.98) * mm});
            skLineSegment(sketch, "E801.14", {"start": v(-10.72, 1.98) * mm, "end": v(-8.55, 0.63) * mm});
            skLineSegment(sketch, "E802.0", {"start": v(5.62, 11.12) * mm, "end": v(3.48, 11) * mm});
            skLineSegment(sketch, "E803.0", {"start": v(6.27, 11.4) * mm, "end": v(5.69, 11.12) * mm});
            skLineSegment(sketch, "E803.1", {"start": v(18.66, 23.23) * mm, "end": v(15.28, 20.47) * mm});
            skLineSegment(sketch, "E803.2", {"start": v(15.28, 20.47) * mm, "end": v(12.17, 17.66) * mm});
            skLineSegment(sketch, "E803.3", {"start": v(12.17, 17.66) * mm, "end": v(9.22, 14.69) * mm});
            skLineSegment(sketch, "E803.4", {"start": v(9.22, 14.69) * mm, "end": v(6.27, 11.4) * mm});
            skLineSegment(sketch, "E804.0", {"start": v(21.5, 25.42) * mm, "end": v(18.63, 23.2) * mm});
            skLineSegment(sketch, "E804.1", {"start": v(24.39, 27.54) * mm, "end": v(21.5, 25.42) * mm});
            skLineSegment(sketch, "E804.2", {"start": v(27.07, 29.33) * mm, "end": v(24.39, 27.54) * mm});
            skLineSegment(sketch, "E804.3", {"start": v(29.86, 30.94) * mm, "end": v(27.07, 29.33) * mm});
            skLineSegment(sketch, "E804.4", {"start": v(15.67, -0.8) * mm, "end": v(19.6, 1.2) * mm});
            skLineSegment(sketch, "E804.5", {"start": v(15.26, -1.3) * mm, "end": v(15.67, -0.8) * mm});
            skLineSegment(sketch, "E804.6", {"start": v(14.3, -4.15) * mm, "end": v(15.26, -1.3) * mm});
            skLineSegment(sketch, "E804.7", {"start": v(13.18, -6.88) * mm, "end": v(14.3, -4.15) * mm});
            skLineSegment(sketch, "E804.8", {"start": v(10.25, -12.57) * mm, "end": v(13.18, -6.88) * mm});
            skLineSegment(sketch, "E804.9", {"start": v(6.68, -17.92) * mm, "end": v(10.25, -12.57) * mm});
            skLineSegment(sketch, "E804.10", {"start": v(3.46, -21.78) * mm, "end": v(6.68, -17.92) * mm});
            skLineSegment(sketch, "E804.11", {"start": v(0.62, -24.5) * mm, "end": v(3.46, -21.78) * mm});
            skLineSegment(sketch, "E804.12", {"start": v(1.54, -22.08) * mm, "end": v(0.62, -24.5) * mm});
            skLineSegment(sketch, "E804.13", {"start": v(2.32, -18.4) * mm, "end": v(1.54, -22.08) * mm});
            skLineSegment(sketch, "E804.14", {"start": v(2.4, -16.13) * mm, "end": v(2.32, -18.4) * mm});
            skLineSegment(sketch, "E804.15", {"start": v(2.01, -13.88) * mm, "end": v(2.4, -16.13) * mm});
            skLineSegment(sketch, "E804.16", {"start": v(-8.31, -12.76) * mm, "end": v(-7.88, -12.7) * mm});
            skLineSegment(sketch, "E804.17", {"start": v(-8.64, -12.64) * mm, "end": v(-8.31, -12.76) * mm});
            skLineSegment(sketch, "E804.18", {"start": v(-11.37, -9.08) * mm, "end": v(-8.64, -12.64) * mm});
            skLineSegment(sketch, "E804.19", {"start": v(-11.42, -8.65) * mm, "end": v(-11.37, -9.08) * mm});
            skLineSegment(sketch, "E804.20", {"start": v(-7.88, -12.7) * mm, "end": v(-6.06, -12.06) * mm});
            skLineSegment(sketch, "E804.21", {"start": v(-6.06, -12.06) * mm, "end": v(-4.25, -11.35) * mm});
            skLineSegment(sketch, "E804.22", {"start": v(-4.25, -11.35) * mm, "end": v(-0.4, -9.78) * mm});
            skLineSegment(sketch, "E804.23", {"start": v(-0.4, -9.78) * mm, "end": v(0.03, -10.27) * mm});
            skLineSegment(sketch, "E804.24", {"start": v(0.03, -10.27) * mm, "end": v(1.24, -11.94) * mm});
            skLineSegment(sketch, "E804.25", {"start": v(1.24, -11.94) * mm, "end": v(2.01, -13.88) * mm});
            skLineSegment(sketch, "E804.26", {"start": v(19.6, 1.2) * mm, "end": v(23.23, 3.3) * mm});
            skLineSegment(sketch, "E804.27", {"start": v(23.23, 3.3) * mm, "end": v(26.74, 5.59) * mm});
            skLineSegment(sketch, "E804.28", {"start": v(26.74, 5.59) * mm, "end": v(30.27, 8.15) * mm});
            skLineSegment(sketch, "E804.29", {"start": v(30.27, 8.15) * mm, "end": v(32.62, 9.96) * mm});
            skLineSegment(sketch, "E804.30", {"start": v(32.62, 9.96) * mm, "end": v(34.94, 11.8) * mm});
            skLineSegment(sketch, "E804.31", {"start": v(34.94, 11.8) * mm, "end": v(37.41, 13.9) * mm});
            skLineSegment(sketch, "E804.32", {"start": v(37.41, 13.9) * mm, "end": v(39.75, 16.14) * mm});
            skLineSegment(sketch, "E804.33", {"start": v(39.75, 16.14) * mm, "end": v(44.1, 21.28) * mm});
            skLineSegment(sketch, "E804.34", {"start": v(44.1, 21.28) * mm, "end": v(47.77, 26.95) * mm});
            skLineSegment(sketch, "E804.35", {"start": v(47.77, 26.95) * mm, "end": v(48.9, 29.02) * mm});
            skLineSegment(sketch, "E804.36", {"start": v(48.9, 29.02) * mm, "end": v(49.97, 31.14) * mm});
            skLineSegment(sketch, "E804.37", {"start": v(49.97, 31.14) * mm, "end": v(50.44, 32.17) * mm});
            skLineSegment(sketch, "E804.38", {"start": v(50.44, 32.17) * mm, "end": v(51.03, 33.65) * mm});
            skLineSegment(sketch, "E804.39", {"start": v(51.03, 33.65) * mm, "end": v(51.51, 35.22) * mm});
            skLineSegment(sketch, "E804.40", {"start": v(51.51, 35.22) * mm, "end": v(51.66, 36.64) * mm});
            skLineSegment(sketch, "E804.41", {"start": v(51.66, 36.64) * mm, "end": v(50.9, 36.8) * mm});
            skLineSegment(sketch, "E804.42", {"start": v(50.9, 36.8) * mm, "end": v(48.83, 36.8) * mm});
            skLineSegment(sketch, "E804.43", {"start": v(48.83, 36.8) * mm, "end": v(46.3, 36.47) * mm});
            skLineSegment(sketch, "E804.44", {"start": v(46.3, 36.47) * mm, "end": v(43.67, 35.93) * mm});
            skLineSegment(sketch, "E804.45", {"start": v(43.67, 35.93) * mm, "end": v(41.31, 35.34) * mm});
            skLineSegment(sketch, "E804.46", {"start": v(41.31, 35.34) * mm, "end": v(38.54, 34.52) * mm});
            skLineSegment(sketch, "E804.47", {"start": v(38.54, 34.52) * mm, "end": v(35.8, 33.6) * mm});
            skLineSegment(sketch, "E804.48", {"start": v(35.8, 33.6) * mm, "end": v(32.78, 32.37) * mm});
            skLineSegment(sketch, "E804.49", {"start": v(32.78, 32.37) * mm, "end": v(29.86, 30.94) * mm});
            skLineSegment(sketch, "E805", {"start": v(5.62, 11.12) * mm, "end": v(5.69, 11.12) * mm});
            skLineSegment(sketch, "E806", {"start": v(-11.42, -8.65) * mm, "end": v(-11.26, -8.35) * mm});
            skSolve(sketch);
        }
        {
            var Q0;
            Q0=makeQuery(id+"F6.imprint","IMPRINT",FACE,{"disambiguationData":[TD([[makeQuery(id+"F6.imprint","IMPRINT",EDGE,{"derivedFrom":sQuery(id+"F6.wireOp",EDGE,"E801.0")}),1.0]])]});
            extrude(context, id + "F7", {"entities" : qUnion([Q0]), "depth" : 1 * mm});
        }
        {
            var Q0;
            Q0=makeQuery(id+"F7.opExtrude","CAP_FACE",FACE,{"disambiguationData":[OSD([sQuery(id+"F6.wireOp",EDGE,"E801.0"),sQuery(id+"F6.wireOp",EDGE,"E801.1"),sQuery(id+"F6.wireOp",EDGE,"E801.2"),sQuery(id+"F6.wireOp",EDGE,"E801.3"),sQuery(id+"F6.wireOp",EDGE,"E801.4"),sQuery(id+"F6.wireOp",EDGE,"E801.5"),sQuery(id+"F6.wireOp",EDGE,"E801.6"),sQuery(id+"F6.wireOp",EDGE,"E801.7"),sQuery(id+"F6.wireOp",EDGE,"E801.8"),sQuery(id+"F6.wireOp",EDGE,"E801.9"),sQuery(id+"F6.wireOp",EDGE,"E801.10"),sQuery(id+"F6.wireOp",EDGE,"E801.11"),sQuery(id+"F6.wireOp",EDGE,"E801.12"),sQuery(id+"F6.wireOp",EDGE,"E801.13"),sQuery(id+"F6.wireOp",EDGE,"E801.14"),sQuery(id+"F6.wireOp",EDGE,"E802.0"),sQuery(id+"F6.wireOp",EDGE,"E803.0"),sQuery(id+"F6.wireOp",EDGE,"E803.1"),sQuery(id+"F6.wireOp",EDGE,"E803.2"),sQuery(id+"F6.wireOp",EDGE,"E803.3"),sQuery(id+"F6.wireOp",EDGE,"E803.4"),sQuery(id+"F6.wireOp",EDGE,"E804.0"),sQuery(id+"F6.wireOp",EDGE,"E804.1"),sQuery(id+"F6.wireOp",EDGE,"E804.2"),sQuery(id+"F6.wireOp",EDGE,"E804.3"),sQuery(id+"F6.wireOp",EDGE,"E804.4"),sQuery(id+"F6.wireOp",EDGE,"E804.5"),sQuery(id+"F6.wireOp",EDGE,"E804.6"),sQuery(id+"F6.wireOp",EDGE,"E804.7"),sQuery(id+"F6.wireOp",EDGE,"E804.8"),sQuery(id+"F6.wireOp",EDGE,"E804.9"),sQuery(id+"F6.wireOp",EDGE,"E804.10"),sQuery(id+"F6.wireOp",EDGE,"E804.11"),sQuery(id+"F6.wireOp",EDGE,"E804.12"),sQuery(id+"F6.wireOp",EDGE,"E804.13"),sQuery(id+"F6.wireOp",EDGE,"E804.14"),sQuery(id+"F6.wireOp",EDGE,"E804.15"),sQuery(id+"F6.wireOp",EDGE,"E804.16"),sQuery(id+"F6.wireOp",EDGE,"E804.17"),sQuery(id+"F6.wireOp",EDGE,"E804.18"),sQuery(id+"F6.wireOp",EDGE,"E804.19"),sQuery(id+"F6.wireOp",EDGE,"E804.20"),sQuery(id+"F6.wireOp",EDGE,"E804.21"),sQuery(id+"F6.wireOp",EDGE,"E804.22"),sQuery(id+"F6.wireOp",EDGE,"E804.23"),sQuery(id+"F6.wireOp",EDGE,"E804.24"),sQuery(id+"F6.wireOp",EDGE,"E804.25"),sQuery(id+"F6.wireOp",EDGE,"E804.26"),sQuery(id+"F6.wireOp",EDGE,"E804.27"),sQuery(id+"F6.wireOp",EDGE,"E804.28"),sQuery(id+"F6.wireOp",EDGE,"E804.29"),sQuery(id+"F6.wireOp",EDGE,"E804.30"),sQuery(id+"F6.wireOp",EDGE,"E804.31"),sQuery(id+"F6.wireOp",EDGE,"E804.32"),sQuery(id+"F6.wireOp",EDGE,"E804.33"),sQuery(id+"F6.wireOp",EDGE,"E804.34"),sQuery(id+"F6.wireOp",EDGE,"E804.35"),sQuery(id+"F6.wireOp",EDGE,"E804.36"),sQuery(id+"F6.wireOp",EDGE,"E804.37"),sQuery(id+"F6.wireOp",EDGE,"E804.38"),sQuery(id+"F6.wireOp",EDGE,"E804.39"),sQuery(id+"F6.wireOp",EDGE,"E804.40"),sQuery(id+"F6.wireOp",EDGE,"E804.41"),sQuery(id+"F6.wireOp",EDGE,"E804.42"),sQuery(id+"F6.wireOp",EDGE,"E804.43"),sQuery(id+"F6.wireOp",EDGE,"E804.44"),sQuery(id+"F6.wireOp",EDGE,"E804.45"),sQuery(id+"F6.wireOp",EDGE,"E804.46"),sQuery(id+"F6.wireOp",EDGE,"E804.47"),sQuery(id+"F6.wireOp",EDGE,"E804.48"),sQuery(id+"F6.wireOp",EDGE,"E804.49"),sQuery(id+"F6.wireOp",EDGE,"E805"),sQuery(id+"F6.wireOp",EDGE,"E806")])],"isStart":false});
            chamfer(context, id + "F8", {"entities" : qUnion([Q0]), "width" : 0.5 * mm, "tangentPropagation" : true});
        }
        {
            var Q0;
            Q0=makeQuery(id+"F5.opExtrude","CAP_FACE",FACE,{"disambiguationData":[OSD([sQuery(id+"F0.wireOp",EDGE,"E0"),sQuery(id+"F0.wireOp",EDGE,"E1"),sQuery(id+"F0.wireOp",EDGE,"E2"),sQuery(id+"F0.wireOp",EDGE,"E3"),sQuery(id+"F0.wireOp",EDGE,"E4"),sQuery(id+"F0.wireOp",EDGE,"E5"),sQuery(id+"F0.wireOp",EDGE,"E6"),sQuery(id+"F0.wireOp",EDGE,"E7"),sQuery(id+"F0.wireOp",EDGE,"E8"),sQuery(id+"F0.wireOp",EDGE,"E9"),sQuery(id+"F0.wireOp",EDGE,"E10"),sQuery(id+"F0.wireOp",EDGE,"E11"),sQuery(id+"F0.wireOp",EDGE,"E12"),sQuery(id+"F0.wireOp",EDGE,"E13"),sQuery(id+"F0.wireOp",EDGE,"E14"),sQuery(id+"F0.wireOp",EDGE,"E15"),sQuery(id+"F0.wireOp",EDGE,"E16"),sQuery(id+"F0.wireOp",EDGE,"E17"),sQuery(id+"F0.wireOp",EDGE,"E18"),sQuery(id+"F0.wireOp",EDGE,"E19"),sQuery(id+"F0.wireOp",EDGE,"E20"),sQuery(id+"F0.wireOp",EDGE,"E21"),sQuery(id+"F0.wireOp",EDGE,"E22"),sQuery(id+"F0.wireOp",EDGE,"E23"),sQuery(id+"F0.wireOp",EDGE,"E24"),sQuery(id+"F0.wireOp",EDGE,"E25"),sQuery(id+"F0.wireOp",EDGE,"E26"),sQuery(id+"F0.wireOp",EDGE,"E27"),sQuery(id+"F0.wireOp",EDGE,"E28"),sQuery(id+"F0.wireOp",EDGE,"E29"),sQuery(id+"F0.wireOp",EDGE,"E30"),sQuery(id+"F0.wireOp",EDGE,"E31"),sQuery(id+"F0.wireOp",EDGE,"E32"),sQuery(id+"F0.wireOp",EDGE,"E33"),sQuery(id+"F0.wireOp",EDGE,"E34"),sQuery(id+"F0.wireOp",EDGE,"E35"),sQuery(id+"F0.wireOp",EDGE,"E36"),sQuery(id+"F0.wireOp",EDGE,"E37"),sQuery(id+"F0.wireOp",EDGE,"E38"),sQuery(id+"F0.wireOp",EDGE,"E39"),sQuery(id+"F0.wireOp",EDGE,"E40"),sQuery(id+"F0.wireOp",EDGE,"E41"),sQuery(id+"F0.wireOp",EDGE,"E42"),sQuery(id+"F0.wireOp",EDGE,"E43"),sQuery(id+"F0.wireOp",EDGE,"E44"),sQuery(id+"F0.wireOp",EDGE,"E45"),sQuery(id+"F0.wireOp",EDGE,"E46"),sQuery(id+"F0.wireOp",EDGE,"E47"),sQuery(id+"F0.wireOp",EDGE,"E48"),sQuery(id+"F0.wireOp",EDGE,"E49"),sQuery(id+"F0.wireOp",EDGE,"E50"),sQuery(id+"F0.wireOp",EDGE,"E51"),sQuery(id+"F0.wireOp",EDGE,"E52"),sQuery(id+"F0.wireOp",EDGE,"E53"),sQuery(id+"F0.wireOp",EDGE,"E54"),sQuery(id+"F0.wireOp",EDGE,"E55"),sQuery(id+"F0.wireOp",EDGE,"E56"),sQuery(id+"F0.wireOp",EDGE,"E57"),sQuery(id+"F0.wireOp",EDGE,"E58"),sQuery(id+"F0.wireOp",EDGE,"E59"),sQuery(id+"F0.wireOp",EDGE,"E60"),sQuery(id+"F0.wireOp",EDGE,"E61"),sQuery(id+"F0.wireOp",EDGE,"E62"),sQuery(id+"F0.wireOp",EDGE,"E63"),sQuery(id+"F0.wireOp",EDGE,"E64"),sQuery(id+"F0.wireOp",EDGE,"E65"),sQuery(id+"F0.wireOp",EDGE,"E66"),sQuery(id+"F0.wireOp",EDGE,"E67"),sQuery(id+"F0.wireOp",EDGE,"E68"),sQuery(id+"F0.wireOp",EDGE,"E69"),sQuery(id+"F0.wireOp",EDGE,"E70"),sQuery(id+"F0.wireOp",EDGE,"E71"),sQuery(id+"F0.wireOp",EDGE,"E72"),sQuery(id+"F0.wireOp",EDGE,"E73"),sQuery(id+"F0.wireOp",EDGE,"E74"),sQuery(id+"F0.wireOp",EDGE,"E75"),sQuery(id+"F0.wireOp",EDGE,"E76"),sQuery(id+"F0.wireOp",EDGE,"E77"),sQuery(id+"F0.wireOp",EDGE,"E78"),sQuery(id+"F0.wireOp",EDGE,"E79"),sQuery(id+"F0.wireOp",EDGE,"E80"),sQuery(id+"F0.wireOp",EDGE,"E81"),sQuery(id+"F0.wireOp",EDGE,"E82"),sQuery(id+"F0.wireOp",EDGE,"E83"),sQuery(id+"F0.wireOp",EDGE,"E84"),sQuery(id+"F0.wireOp",EDGE,"E85"),sQuery(id+"F0.wireOp",EDGE,"E86"),sQuery(id+"F0.wireOp",EDGE,"E87"),sQuery(id+"F0.wireOp",EDGE,"E88"),sQuery(id+"F0.wireOp",EDGE,"E89"),sQuery(id+"F0.wireOp",EDGE,"E90"),sQuery(id+"F0.wireOp",EDGE,"E91"),sQuery(id+"F0.wireOp",EDGE,"E92"),sQuery(id+"F0.wireOp",EDGE,"E93"),sQuery(id+"F0.wireOp",EDGE,"E94"),sQuery(id+"F0.wireOp",EDGE,"E95"),sQuery(id+"F0.wireOp",EDGE,"E96"),sQuery(id+"F0.wireOp",EDGE,"E97"),sQuery(id+"F0.wireOp",EDGE,"E98"),sQuery(id+"F0.wireOp",EDGE,"E99"),sQuery(id+"F0.wireOp",EDGE,"E100"),sQuery(id+"F0.wireOp",EDGE,"E101"),sQuery(id+"F0.wireOp",EDGE,"E102"),sQuery(id+"F0.wireOp",EDGE,"E103"),sQuery(id+"F0.wireOp",EDGE,"E104"),sQuery(id+"F0.wireOp",EDGE,"E105"),sQuery(id+"F0.wireOp",EDGE,"E106"),sQuery(id+"F0.wireOp",EDGE,"E107"),sQuery(id+"F0.wireOp",EDGE,"E108"),sQuery(id+"F0.wireOp",EDGE,"E109"),sQuery(id+"F0.wireOp",EDGE,"E110"),sQuery(id+"F0.wireOp",EDGE,"E111"),sQuery(id+"F0.wireOp",EDGE,"E112"),sQuery(id+"F0.wireOp",EDGE,"E113"),sQuery(id+"F0.wireOp",EDGE,"E114"),sQuery(id+"F0.wireOp",EDGE,"E115"),sQuery(id+"F0.wireOp",EDGE,"E116"),sQuery(id+"F0.wireOp",EDGE,"E117"),sQuery(id+"F0.wireOp",EDGE,"E118"),sQuery(id+"F0.wireOp",EDGE,"E119"),sQuery(id+"F0.wireOp",EDGE,"E120"),sQuery(id+"F0.wireOp",EDGE,"E121"),sQuery(id+"F0.wireOp",EDGE,"E122"),sQuery(id+"F0.wireOp",EDGE,"E123"),sQuery(id+"F0.wireOp",EDGE,"E124"),sQuery(id+"F0.wireOp",EDGE,"E125"),sQuery(id+"F0.wireOp",EDGE,"E126"),sQuery(id+"F0.wireOp",EDGE,"E127"),sQuery(id+"F0.wireOp",EDGE,"E128"),sQuery(id+"F0.wireOp",EDGE,"E129"),sQuery(id+"F0.wireOp",EDGE,"E130"),sQuery(id+"F0.wireOp",EDGE,"E131"),sQuery(id+"F0.wireOp",EDGE,"E132"),sQuery(id+"F0.wireOp",EDGE,"E133"),sQuery(id+"F0.wireOp",EDGE,"E134"),sQuery(id+"F0.wireOp",EDGE,"E135"),sQuery(id+"F0.wireOp",EDGE,"E136"),sQuery(id+"F0.wireOp",EDGE,"E137"),sQuery(id+"F0.wireOp",EDGE,"E138"),sQuery(id+"F0.wireOp",EDGE,"E139"),sQuery(id+"F0.wireOp",EDGE,"E140"),sQuery(id+"F0.wireOp",EDGE,"E141"),sQuery(id+"F0.wireOp",EDGE,"E142"),sQuery(id+"F0.wireOp",EDGE,"E143"),sQuery(id+"F0.wireOp",EDGE,"E144"),sQuery(id+"F0.wireOp",EDGE,"E145"),sQuery(id+"F0.wireOp",EDGE,"E146"),sQuery(id+"F0.wireOp",EDGE,"E147"),sQuery(id+"F0.wireOp",EDGE,"E148"),sQuery(id+"F0.wireOp",EDGE,"E149"),sQuery(id+"F0.wireOp",EDGE,"E150"),sQuery(id+"F0.wireOp",EDGE,"E151"),sQuery(id+"F0.wireOp",EDGE,"E152"),sQuery(id+"F0.wireOp",EDGE,"E153"),sQuery(id+"F0.wireOp",EDGE,"E154"),sQuery(id+"F0.wireOp",EDGE,"E155"),sQuery(id+"F0.wireOp",EDGE,"E156"),sQuery(id+"F0.wireOp",EDGE,"E157"),sQuery(id+"F0.wireOp",EDGE,"E158"),sQuery(id+"F0.wireOp",EDGE,"E159"),sQuery(id+"F0.wireOp",EDGE,"E160"),sQuery(id+"F0.wireOp",EDGE,"E161"),sQuery(id+"F0.wireOp",EDGE,"E162"),sQuery(id+"F0.wireOp",EDGE,"E163"),sQuery(id+"F0.wireOp",EDGE,"E164"),sQuery(id+"F0.wireOp",EDGE,"E165"),sQuery(id+"F0.wireOp",EDGE,"E166"),sQuery(id+"F0.wireOp",EDGE,"E167"),sQuery(id+"F0.wireOp",EDGE,"E168"),sQuery(id+"F0.wireOp",EDGE,"E169"),sQuery(id+"F0.wireOp",EDGE,"E170"),sQuery(id+"F0.wireOp",EDGE,"E171"),sQuery(id+"F0.wireOp",EDGE,"E172"),sQuery(id+"F0.wireOp",EDGE,"E173"),sQuery(id+"F0.wireOp",EDGE,"E174"),sQuery(id+"F0.wireOp",EDGE,"E175"),sQuery(id+"F0.wireOp",EDGE,"E176"),sQuery(id+"F0.wireOp",EDGE,"E177"),sQuery(id+"F0.wireOp",EDGE,"E178"),sQuery(id+"F0.wireOp",EDGE,"E179"),sQuery(id+"F0.wireOp",EDGE,"E180"),sQuery(id+"F0.wireOp",EDGE,"E181"),sQuery(id+"F0.wireOp",EDGE,"E182"),sQuery(id+"F0.wireOp",EDGE,"E183"),sQuery(id+"F0.wireOp",EDGE,"E184"),sQuery(id+"F0.wireOp",EDGE,"E185"),sQuery(id+"F0.wireOp",EDGE,"E186"),sQuery(id+"F0.wireOp",EDGE,"E187"),sQuery(id+"F0.wireOp",EDGE,"E188"),sQuery(id+"F0.wireOp",EDGE,"E189"),sQuery(id+"F0.wireOp",EDGE,"E190"),sQuery(id+"F0.wireOp",EDGE,"E191"),sQuery(id+"F0.wireOp",EDGE,"E192"),sQuery(id+"F0.wireOp",EDGE,"E193"),sQuery(id+"F0.wireOp",EDGE,"E194"),sQuery(id+"F0.wireOp",EDGE,"E195"),sQuery(id+"F0.wireOp",EDGE,"E196"),sQuery(id+"F0.wireOp",EDGE,"E197"),sQuery(id+"F0.wireOp",EDGE,"E198"),sQuery(id+"F0.wireOp",EDGE,"E199"),sQuery(id+"F0.wireOp",EDGE,"E200"),sQuery(id+"F0.wireOp",EDGE,"E201"),sQuery(id+"F0.wireOp",EDGE,"E202"),sQuery(id+"F0.wireOp",EDGE,"E203"),sQuery(id+"F0.wireOp",EDGE,"E204"),sQuery(id+"F0.wireOp",EDGE,"E205"),sQuery(id+"F0.wireOp",EDGE,"E206"),sQuery(id+"F0.wireOp",EDGE,"E207"),sQuery(id+"F0.wireOp",EDGE,"E208"),sQuery(id+"F0.wireOp",EDGE,"E209"),sQuery(id+"F0.wireOp",EDGE,"E210"),sQuery(id+"F0.wireOp",EDGE,"E211"),sQuery(id+"F0.wireOp",EDGE,"E212"),sQuery(id+"F0.wireOp",EDGE,"E213"),sQuery(id+"F0.wireOp",EDGE,"E214"),sQuery(id+"F0.wireOp",EDGE,"E215"),sQuery(id+"F0.wireOp",EDGE,"E216"),sQuery(id+"F0.wireOp",EDGE,"E217"),sQuery(id+"F0.wireOp",EDGE,"E218"),sQuery(id+"F0.wireOp",EDGE,"E219"),sQuery(id+"F0.wireOp",EDGE,"E220"),sQuery(id+"F0.wireOp",EDGE,"E221"),sQuery(id+"F0.wireOp",EDGE,"E222"),sQuery(id+"F0.wireOp",EDGE,"E223"),sQuery(id+"F0.wireOp",EDGE,"E224"),sQuery(id+"F0.wireOp",EDGE,"E225"),sQuery(id+"F0.wireOp",EDGE,"E226"),sQuery(id+"F0.wireOp",EDGE,"E227"),sQuery(id+"F0.wireOp",EDGE,"E228"),sQuery(id+"F0.wireOp",EDGE,"E229"),sQuery(id+"F0.wireOp",EDGE,"E230"),sQuery(id+"F0.wireOp",EDGE,"E231"),sQuery(id+"F0.wireOp",EDGE,"E232"),sQuery(id+"F0.wireOp",EDGE,"E233"),sQuery(id+"F0.wireOp",EDGE,"E234"),sQuery(id+"F0.wireOp",EDGE,"E510"),sQuery(id+"F0.wireOp",EDGE,"E511"),sQuery(id+"F0.wireOp",EDGE,"E512"),sQuery(id+"F0.wireOp",EDGE,"E513"),sQuery(id+"F0.wireOp",EDGE,"E514"),sQuery(id+"F0.wireOp",EDGE,"E515"),sQuery(id+"F0.wireOp",EDGE,"E516"),sQuery(id+"F0.wireOp",EDGE,"E517"),sQuery(id+"F0.wireOp",EDGE,"E518"),sQuery(id+"F0.wireOp",EDGE,"E519"),sQuery(id+"F0.wireOp",EDGE,"E520"),sQuery(id+"F0.wireOp",EDGE,"E521"),sQuery(id+"F0.wireOp",EDGE,"E522"),sQuery(id+"F0.wireOp",EDGE,"E523"),sQuery(id+"F0.wireOp",EDGE,"E524"),sQuery(id+"F0.wireOp",EDGE,"E525"),sQuery(id+"F0.wireOp",EDGE,"E526"),sQuery(id+"F0.wireOp",EDGE,"E527"),sQuery(id+"F0.wireOp",EDGE,"E528"),sQuery(id+"F0.wireOp",EDGE,"E529"),sQuery(id+"F0.wireOp",EDGE,"E530"),sQuery(id+"F0.wireOp",EDGE,"E531"),sQuery(id+"F0.wireOp",EDGE,"E532"),sQuery(id+"F0.wireOp",EDGE,"E533"),sQuery(id+"F0.wireOp",EDGE,"E534"),sQuery(id+"F0.wireOp",EDGE,"E535"),sQuery(id+"F0.wireOp",EDGE,"E536"),sQuery(id+"F0.wireOp",EDGE,"E537"),sQuery(id+"F0.wireOp",EDGE,"E538"),sQuery(id+"F0.wireOp",EDGE,"E539"),sQuery(id+"F0.wireOp",EDGE,"E540"),sQuery(id+"F0.wireOp",EDGE,"E541"),sQuery(id+"F0.wireOp",EDGE,"E542"),sQuery(id+"F0.wireOp",EDGE,"E543"),sQuery(id+"F0.wireOp",EDGE,"E544"),sQuery(id+"F0.wireOp",EDGE,"E545"),sQuery(id+"F0.wireOp",EDGE,"E546"),sQuery(id+"F0.wireOp",EDGE,"E547"),sQuery(id+"F0.wireOp",EDGE,"E548"),sQuery(id+"F0.wireOp",EDGE,"E549"),sQuery(id+"F0.wireOp",EDGE,"E550"),sQuery(id+"F0.wireOp",EDGE,"E551"),sQuery(id+"F0.wireOp",EDGE,"E552"),sQuery(id+"F0.wireOp",EDGE,"E553"),sQuery(id+"F0.wireOp",EDGE,"E554"),sQuery(id+"F0.wireOp",EDGE,"E555"),sQuery(id+"F0.wireOp",EDGE,"E556"),sQuery(id+"F0.wireOp",EDGE,"E557"),sQuery(id+"F0.wireOp",EDGE,"E558"),sQuery(id+"F0.wireOp",EDGE,"E559"),sQuery(id+"F0.wireOp",EDGE,"E560"),sQuery(id+"F0.wireOp",EDGE,"E561"),sQuery(id+"F0.wireOp",EDGE,"E562"),sQuery(id+"F0.wireOp",EDGE,"E563"),sQuery(id+"F0.wireOp",EDGE,"E564"),sQuery(id+"F0.wireOp",EDGE,"E565"),sQuery(id+"F0.wireOp",EDGE,"E566"),sQuery(id+"F0.wireOp",EDGE,"E567"),sQuery(id+"F0.wireOp",EDGE,"E568"),sQuery(id+"F0.wireOp",EDGE,"E569"),sQuery(id+"F0.wireOp",EDGE,"E570"),sQuery(id+"F0.wireOp",EDGE,"E571"),sQuery(id+"F0.wireOp",EDGE,"E572"),sQuery(id+"F0.wireOp",EDGE,"E573"),sQuery(id+"F0.wireOp",EDGE,"E574"),sQuery(id+"F0.wireOp",EDGE,"E575"),sQuery(id+"F0.wireOp",EDGE,"E576"),sQuery(id+"F0.wireOp",EDGE,"E577"),sQuery(id+"F0.wireOp",EDGE,"E578"),sQuery(id+"F0.wireOp",EDGE,"E579"),sQuery(id+"F0.wireOp",EDGE,"E580"),sQuery(id+"F0.wireOp",EDGE,"E581"),sQuery(id+"F0.wireOp",EDGE,"E582"),sQuery(id+"F0.wireOp",EDGE,"E583"),sQuery(id+"F0.wireOp",EDGE,"E584"),sQuery(id+"F0.wireOp",EDGE,"E585"),sQuery(id+"F0.wireOp",EDGE,"E586"),sQuery(id+"F0.wireOp",EDGE,"E587"),sQuery(id+"F0.wireOp",EDGE,"E588"),sQuery(id+"F0.wireOp",EDGE,"E589"),sQuery(id+"F0.wireOp",EDGE,"E590"),sQuery(id+"F0.wireOp",EDGE,"E591"),sQuery(id+"F0.wireOp",EDGE,"E592"),sQuery(id+"F0.wireOp",EDGE,"E593"),sQuery(id+"F0.wireOp",EDGE,"E594"),sQuery(id+"F0.wireOp",EDGE,"E595"),sQuery(id+"F0.wireOp",EDGE,"E596"),sQuery(id+"F0.wireOp",EDGE,"E597"),sQuery(id+"F0.wireOp",EDGE,"E598"),sQuery(id+"F0.wireOp",EDGE,"E599"),sQuery(id+"F0.wireOp",EDGE,"E600"),sQuery(id+"F0.wireOp",EDGE,"E601"),sQuery(id+"F0.wireOp",EDGE,"E602"),sQuery(id+"F0.wireOp",EDGE,"E603"),sQuery(id+"F0.wireOp",EDGE,"E604"),sQuery(id+"F0.wireOp",EDGE,"E605"),sQuery(id+"F0.wireOp",EDGE,"E606"),sQuery(id+"F0.wireOp",EDGE,"E607"),sQuery(id+"F0.wireOp",EDGE,"E608"),sQuery(id+"F0.wireOp",EDGE,"E609"),sQuery(id+"F0.wireOp",EDGE,"E610"),sQuery(id+"F0.wireOp",EDGE,"E611"),sQuery(id+"F0.wireOp",EDGE,"E612"),sQuery(id+"F0.wireOp",EDGE,"E613"),sQuery(id+"F0.wireOp",EDGE,"E614"),sQuery(id+"F0.wireOp",EDGE,"E615"),sQuery(id+"F0.wireOp",EDGE,"E616"),sQuery(id+"F0.wireOp",EDGE,"E617"),sQuery(id+"F0.wireOp",EDGE,"E618"),sQuery(id+"F0.wireOp",EDGE,"E619"),sQuery(id+"F0.wireOp",EDGE,"E620"),sQuery(id+"F0.wireOp",EDGE,"E621"),sQuery(id+"F0.wireOp",EDGE,"E622"),sQuery(id+"F0.wireOp",EDGE,"E623"),sQuery(id+"F0.wireOp",EDGE,"E624"),sQuery(id+"F0.wireOp",EDGE,"E625"),sQuery(id+"F0.wireOp",EDGE,"E626"),sQuery(id+"F0.wireOp",EDGE,"E627"),sQuery(id+"F0.wireOp",EDGE,"E628"),sQuery(id+"F0.wireOp",EDGE,"E629"),sQuery(id+"F0.wireOp",EDGE,"E630"),sQuery(id+"F0.wireOp",EDGE,"E631"),sQuery(id+"F0.wireOp",EDGE,"E632"),sQuery(id+"F0.wireOp",EDGE,"E633"),sQuery(id+"F0.wireOp",EDGE,"E634"),sQuery(id+"F0.wireOp",EDGE,"E635"),sQuery(id+"F0.wireOp",EDGE,"E636"),sQuery(id+"F0.wireOp",EDGE,"E637"),sQuery(id+"F0.wireOp",EDGE,"E638"),sQuery(id+"F0.wireOp",EDGE,"E639"),sQuery(id+"F0.wireOp",EDGE,"E640"),sQuery(id+"F0.wireOp",EDGE,"E641"),sQuery(id+"F0.wireOp",EDGE,"E642"),sQuery(id+"F0.wireOp",EDGE,"E643"),sQuery(id+"F0.wireOp",EDGE,"E644"),sQuery(id+"F0.wireOp",EDGE,"E645"),sQuery(id+"F0.wireOp",EDGE,"E646"),sQuery(id+"F0.wireOp",EDGE,"E647"),sQuery(id+"F0.wireOp",EDGE,"E648"),sQuery(id+"F0.wireOp",EDGE,"E649"),sQuery(id+"F0.wireOp",EDGE,"E650"),sQuery(id+"F0.wireOp",EDGE,"E651"),sQuery(id+"F0.wireOp",EDGE,"E652"),sQuery(id+"F0.wireOp",EDGE,"E653"),sQuery(id+"F0.wireOp",EDGE,"E654"),sQuery(id+"F0.wireOp",EDGE,"E655"),sQuery(id+"F0.wireOp",EDGE,"E656"),sQuery(id+"F0.wireOp",EDGE,"E657"),sQuery(id+"F0.wireOp",EDGE,"E658"),sQuery(id+"F0.wireOp",EDGE,"E659"),sQuery(id+"F0.wireOp",EDGE,"E660"),sQuery(id+"F0.wireOp",EDGE,"E661"),sQuery(id+"F0.wireOp",EDGE,"E662"),sQuery(id+"F0.wireOp",EDGE,"E663"),sQuery(id+"F0.wireOp",EDGE,"E664"),sQuery(id+"F0.wireOp",EDGE,"E665"),sQuery(id+"F0.wireOp",EDGE,"E666"),sQuery(id+"F0.wireOp",EDGE,"E667"),sQuery(id+"F0.wireOp",EDGE,"E668"),sQuery(id+"F0.wireOp",EDGE,"E669"),sQuery(id+"F0.wireOp",EDGE,"E670"),sQuery(id+"F0.wireOp",EDGE,"E671"),sQuery(id+"F0.wireOp",EDGE,"E672"),sQuery(id+"F0.wireOp",EDGE,"E673"),sQuery(id+"F0.wireOp",EDGE,"E674"),sQuery(id+"F0.wireOp",EDGE,"E675"),sQuery(id+"F0.wireOp",EDGE,"E676"),sQuery(id+"F0.wireOp",EDGE,"E677"),sQuery(id+"F0.wireOp",EDGE,"E678"),sQuery(id+"F0.wireOp",EDGE,"E679"),sQuery(id+"F0.wireOp",EDGE,"E680"),sQuery(id+"F0.wireOp",EDGE,"E681"),sQuery(id+"F0.wireOp",EDGE,"E682"),sQuery(id+"F0.wireOp",EDGE,"E683"),sQuery(id+"F0.wireOp",EDGE,"E684"),sQuery(id+"F0.wireOp",EDGE,"E685"),sQuery(id+"F0.wireOp",EDGE,"E686"),sQuery(id+"F0.wireOp",EDGE,"E687"),sQuery(id+"F0.wireOp",EDGE,"E688"),sQuery(id+"F0.wireOp",EDGE,"E689"),sQuery(id+"F0.wireOp",EDGE,"E690"),sQuery(id+"F0.wireOp",EDGE,"E691"),sQuery(id+"F0.wireOp",EDGE,"E692"),sQuery(id+"F0.wireOp",EDGE,"E693"),sQuery(id+"F0.wireOp",EDGE,"E694"),sQuery(id+"F0.wireOp",EDGE,"E695"),sQuery(id+"F0.wireOp",EDGE,"E696"),sQuery(id+"F0.wireOp",EDGE,"E697"),sQuery(id+"F0.wireOp",EDGE,"E698")])],"isStart":false});
            var sketch = newSketch(context, id + "F9", { "sketchPlane" : qUnion([Q0])});
            skLineSegment(sketch, "E807.0", {"start": v(17.35, 24.2) * mm, "end": v(13.8, 25.82) * mm});
            skLineSegment(sketch, "E808.0", {"start": v(14.07, 21.52) * mm, "end": v(17.35, 24.2) * mm});
            skLineSegment(sketch, "E809.0", {"start": v(11.04, 18.77) * mm, "end": v(14.07, 21.52) * mm});
            skLineSegment(sketch, "E810.0", {"start": v(8.16, 15.86) * mm, "end": v(11.04, 18.77) * mm});
            skLineSegment(sketch, "E811.0", {"start": v(5.3, 12.7) * mm, "end": v(8.16, 15.86) * mm});
            skLineSegment(sketch, "E812.0", {"start": v(3.23, 12.57) * mm, "end": v(5.3, 12.7) * mm});
            skLineSegment(sketch, "E813.0", {"start": v(1.17, 12.35) * mm, "end": v(3.23, 12.57) * mm});
            skLineSegment(sketch, "E814.0", {"start": v(-5.17, 11.15) * mm, "end": v(1.17, 12.35) * mm});
            skLineSegment(sketch, "E815.0", {"start": v(-11.38, 9.24) * mm, "end": v(-5.17, 11.15) * mm});
            skLineSegment(sketch, "E816.0", {"start": v(-17.32, 6.62) * mm, "end": v(-11.38, 9.24) * mm});
            skLineSegment(sketch, "E817.0", {"start": v(-22.86, 3.27) * mm, "end": v(-17.32, 6.62) * mm});
            skLineSegment(sketch, "E818.0", {"start": v(-21.74, 8.5) * mm, "end": v(-22.86, 3.27) * mm});
            skLineSegment(sketch, "E819.0", {"start": v(-19.6, 13.45) * mm, "end": v(-21.74, 8.5) * mm});
            skLineSegment(sketch, "E820.0", {"start": v(-16.48, 17.95) * mm, "end": v(-19.6, 13.45) * mm});
            skLineSegment(sketch, "E821.0", {"start": v(-12.38, 21.83) * mm, "end": v(-16.48, 17.95) * mm});
            skLineSegment(sketch, "E822.0", {"start": v(-8.94, 24.1) * mm, "end": v(-12.38, 21.83) * mm});
            skLineSegment(sketch, "E823.0", {"start": v(-5.3, 25.78) * mm, "end": v(-8.94, 24.1) * mm});
            skLineSegment(sketch, "E824.0", {"start": v(-1.52, 26.9) * mm, "end": v(-5.3, 25.78) * mm});
            skLineSegment(sketch, "E825.0", {"start": v(2.35, 27.45) * mm, "end": v(-1.52, 26.9) * mm});
            skLineSegment(sketch, "E826.0", {"start": v(6.23, 27.45) * mm, "end": v(2.35, 27.45) * mm});
            skLineSegment(sketch, "E827.0", {"start": v(10.06, 26.9) * mm, "end": v(6.23, 27.45) * mm});
            skLineSegment(sketch, "E828.0", {"start": v(13.8, 25.82) * mm, "end": v(10.06, 26.9) * mm});
            skLineSegment(sketch, "E829.0", {"start": v(2.37, 27.15) * mm, "end": v(-1.45, 26.6) * mm});
            skLineSegment(sketch, "E829.1", {"start": v(6.2, 27.15) * mm, "end": v(2.37, 27.15) * mm});
            skLineSegment(sketch, "E829.2", {"start": v(10, 26.6) * mm, "end": v(6.2, 27.15) * mm});
            skLineSegment(sketch, "E829.3", {"start": v(13.69, 25.54) * mm, "end": v(10, 26.6) * mm});
            skLineSegment(sketch, "E829.4", {"start": v(16.79, 24.14) * mm, "end": v(13.69, 25.54) * mm});
            skLineSegment(sketch, "E829.5", {"start": v(-1.45, 26.6) * mm, "end": v(-5.2, 25.5) * mm});
            skLineSegment(sketch, "E829.6", {"start": v(13.88, 21.74) * mm, "end": v(16.79, 24.14) * mm});
            skLineSegment(sketch, "E829.7", {"start": v(10.84, 18.98) * mm, "end": v(13.88, 21.74) * mm});
            skLineSegment(sketch, "E829.8", {"start": v(7.94, 16.07) * mm, "end": v(10.84, 18.98) * mm});
            skLineSegment(sketch, "E829.9", {"start": v(5.16, 12.98) * mm, "end": v(7.94, 16.07) * mm});
            skLineSegment(sketch, "E829.10", {"start": v(3.2, 12.87) * mm, "end": v(5.16, 12.98) * mm});
            skLineSegment(sketch, "E829.11", {"start": v(1.13, 12.64) * mm, "end": v(3.2, 12.87) * mm});
            skLineSegment(sketch, "E829.12", {"start": v(-16.25, 17.75) * mm, "end": v(-19.34, 13.3) * mm});
            skLineSegment(sketch, "E829.13", {"start": v(-12.19, 21.6) * mm, "end": v(-16.25, 17.75) * mm});
            skLineSegment(sketch, "E829.14", {"start": v(-8.8, 23.83) * mm, "end": v(-12.19, 21.6) * mm});
            skLineSegment(sketch, "E829.15", {"start": v(-5.2, 25.5) * mm, "end": v(-8.8, 23.83) * mm});
            skLineSegment(sketch, "E829.16", {"start": v(-19.34, 13.3) * mm, "end": v(-21.45, 8.4) * mm});
            skLineSegment(sketch, "E829.17", {"start": v(-21.45, 8.4) * mm, "end": v(-22.42, 3.88) * mm});
            skLineSegment(sketch, "E829.18", {"start": v(-22.42, 3.88) * mm, "end": v(-17.46, 6.89) * mm});
            skLineSegment(sketch, "E829.19", {"start": v(-17.46, 6.89) * mm, "end": v(-11.48, 9.53) * mm});
            skLineSegment(sketch, "E829.20", {"start": v(-11.48, 9.53) * mm, "end": v(-5.24, 11.44) * mm});
            skLineSegment(sketch, "E829.21", {"start": v(-5.24, 11.44) * mm, "end": v(1.13, 12.64) * mm});
            skLineSegment(sketch, "E830.0", {"start": v(-22.78, -3.6) * mm, "end": v(-21.79, -8.03) * mm});
            skLineSegment(sketch, "E831.0", {"start": v(-21.79, -8.03) * mm, "end": v(-19.52, -6.23) * mm});
            skLineSegment(sketch, "E832.0", {"start": v(-19.52, -6.23) * mm, "end": v(-17.77, -4.85) * mm});
            skLineSegment(sketch, "E833.0", {"start": v(-17.77, -4.85) * mm, "end": v(-16.65, -3.97) * mm});
            skLineSegment(sketch, "E834.0", {"start": v(-16.65, -3.97) * mm, "end": v(-16.25, -3.65) * mm});
            skLineSegment(sketch, "E835.0", {"start": v(-16.25, -3.65) * mm, "end": v(-14.88, -2.94) * mm});
            skLineSegment(sketch, "E836.0", {"start": v(-14.88, -2.94) * mm, "end": v(-13.93, -2.78) * mm});
            skLineSegment(sketch, "E837.0", {"start": v(-13.93, -2.78) * mm, "end": v(-13.4, -2.91) * mm});
            skLineSegment(sketch, "E838.0", {"start": v(-13.4, -2.91) * mm, "end": v(-13.42, -3.45) * mm});
            skLineSegment(sketch, "E839.0", {"start": v(-13.42, -3.45) * mm, "end": v(-13.81, -4.33) * mm});
            skLineSegment(sketch, "E840.0", {"start": v(-13.81, -4.33) * mm, "end": v(-14.22, -4.9) * mm});
            skLineSegment(sketch, "E841.0", {"start": v(-14.22, -4.9) * mm, "end": v(-14.83, -5.46) * mm});
            skLineSegment(sketch, "E842.0", {"start": v(-14.83, -5.46) * mm, "end": v(-15.42, -5.9) * mm});
            skLineSegment(sketch, "E843.0", {"start": v(-15.42, -5.9) * mm, "end": v(-16.72, -6.86) * mm});
            skLineSegment(sketch, "E844.0", {"start": v(-16.72, -6.86) * mm, "end": v(-18.63, -8.27) * mm});
            skLineSegment(sketch, "E845.0", {"start": v(-18.63, -8.27) * mm, "end": v(-21.06, -10.05) * mm});
            skLineSegment(sketch, "E846.0", {"start": v(-23.03, 0.9) * mm, "end": v(-22.78, -3.6) * mm});
            skLineSegment(sketch, "E847.0", {"start": v(-19.94, 1.43) * mm, "end": v(-23.03, 0.9) * mm});
            skLineSegment(sketch, "E848.0", {"start": v(-17.62, 1.61) * mm, "end": v(-19.94, 1.43) * mm});
            skLineSegment(sketch, "E849.0", {"start": v(-15.29, 1.53) * mm, "end": v(-17.62, 1.61) * mm});
            skLineSegment(sketch, "E850.0", {"start": v(-13.28, 1.2) * mm, "end": v(-15.29, 1.53) * mm});
            skLineSegment(sketch, "E851.0", {"start": v(-11.37, 0.54) * mm, "end": v(-13.28, 1.2) * mm});
            skLineSegment(sketch, "E852.0", {"start": v(-9.75, -0.44) * mm, "end": v(-11.37, 0.54) * mm});
            skLineSegment(sketch, "E853.0", {"start": v(-8.45, -1.8) * mm, "end": v(-9.75, -0.44) * mm});
            skLineSegment(sketch, "E854.0", {"start": v(-10, -3.86) * mm, "end": v(-8.45, -1.8) * mm});
            skLineSegment(sketch, "E855.0", {"start": v(-11.33, -5.64) * mm, "end": v(-10, -3.86) * mm});
            skLineSegment(sketch, "E856.0", {"start": v(-12.58, -7.48) * mm, "end": v(-11.33, -5.64) * mm});
            skLineSegment(sketch, "E857.0", {"start": v(-21.06, -10.05) * mm, "end": v(-19.05, -14.05) * mm});
            skLineSegment(sketch, "E858.0", {"start": v(-19.05, -14.05) * mm, "end": v(-18.15, -13.32) * mm});
            skLineSegment(sketch, "E859.0", {"start": v(-18.15, -13.32) * mm, "end": v(-17.47, -12.77) * mm});
            skLineSegment(sketch, "E860.0", {"start": v(-17.47, -12.77) * mm, "end": v(-17.04, -12.42) * mm});
            skLineSegment(sketch, "E861.0", {"start": v(-16.88, -12.3) * mm, "end": v(-16.12, -11.81) * mm});
            skLineSegment(sketch, "E862.0", {"start": v(-16.12, -11.81) * mm, "end": v(-15.27, -11.5) * mm});
            skLineSegment(sketch, "E863.0", {"start": v(-15.27, -11.5) * mm, "end": v(-14.13, -11.38) * mm});
            skLineSegment(sketch, "E864.0", {"start": v(-14.13, -11.38) * mm, "end": v(-13.49, -11.57) * mm});
            skLineSegment(sketch, "E865.0", {"start": v(-13.49, -11.57) * mm, "end": v(-13.46, -12.25) * mm});
            skLineSegment(sketch, "E866.0", {"start": v(-13.46, -12.25) * mm, "end": v(-13.88, -13.32) * mm});
            skLineSegment(sketch, "E867.0", {"start": v(-13.88, -13.32) * mm, "end": v(-14.33, -14) * mm});
            skLineSegment(sketch, "E868.0", {"start": v(-14.33, -14) * mm, "end": v(-15.03, -14.65) * mm});
            skLineSegment(sketch, "E869.0", {"start": v(-15.03, -14.65) * mm, "end": v(-15.31, -14.86) * mm});
            skLineSegment(sketch, "E870.0", {"start": v(-15.31, -14.86) * mm, "end": v(-15.83, -15.23) * mm});
            skLineSegment(sketch, "E871.0", {"start": v(-15.83, -15.23) * mm, "end": v(-16.55, -15.74) * mm});
            skLineSegment(sketch, "E872.0", {"start": v(-16.55, -15.74) * mm, "end": v(-17.46, -16.39) * mm});
            skLineSegment(sketch, "E873.0", {"start": v(-17.46, -16.39) * mm, "end": v(-17.36, -16.52) * mm});
            skLineSegment(sketch, "E874.0", {"start": v(-17.36, -16.52) * mm, "end": v(-14.1, -20.06) * mm});
            skLineSegment(sketch, "E875.0", {"start": v(-14.1, -20.06) * mm, "end": v(-10.38, -22.9) * mm});
            skLineSegment(sketch, "E876.0", {"start": v(-6.3, -25.04) * mm, "end": v(-1.97, -26.45) * mm});
            skLineSegment(sketch, "E877.0", {"start": v(-1.97, -26.45) * mm, "end": v(-1.14, -24.75) * mm});
            skLineSegment(sketch, "E878.0", {"start": v(-1.14, -24.75) * mm, "end": v(-0.4, -22.9) * mm});
            skLineSegment(sketch, "E879.0", {"start": v(-0.4, -22.9) * mm, "end": v(0.22, -20.95) * mm});
            skLineSegment(sketch, "E880.0", {"start": v(0.64, -18.97) * mm, "end": v(0.8, -17) * mm});
            skLineSegment(sketch, "E881.0", {"start": v(-10.38, -22.9) * mm, "end": v(-6.3, -25.04) * mm});
            skLineSegment(sketch, "E882.0", {"start": v(0.8, -17) * mm, "end": v(0.66, -15.09) * mm});
            skLineSegment(sketch, "E883.0", {"start": v(0.66, -15.09) * mm, "end": v(0.12, -13.3) * mm});
            skLineSegment(sketch, "E884.0", {"start": v(0.12, -13.3) * mm, "end": v(-0.85, -11.67) * mm});
            skLineSegment(sketch, "E885.0", {"start": v(-0.85, -11.67) * mm, "end": v(-3.65, -12.81) * mm});
            skLineSegment(sketch, "E886.0", {"start": v(-3.65, -12.81) * mm, "end": v(-5.51, -13.55) * mm});
            skLineSegment(sketch, "E887.0", {"start": v(-5.51, -13.55) * mm, "end": v(-7.4, -14.22) * mm});
            skLineSegment(sketch, "E888.0", {"start": v(-7.4, -14.22) * mm, "end": v(-8.05, -14.35) * mm});
            skLineSegment(sketch, "E889.0", {"start": v(-8.05, -14.35) * mm, "end": v(-8.7, -14.32) * mm});
            skLineSegment(sketch, "E890.0", {"start": v(-8.7, -14.32) * mm, "end": v(-9.32, -14.1) * mm});
            skLineSegment(sketch, "E891.0", {"start": v(-9.32, -14.1) * mm, "end": v(-9.83, -13.69) * mm});
            skLineSegment(sketch, "E892.0", {"start": v(-9.83, -13.69) * mm, "end": v(-12.7, -9.95) * mm});
            skLineSegment(sketch, "E893.0", {"start": v(-12.7, -9.95) * mm, "end": v(-12.98, -9.35) * mm});
            skLineSegment(sketch, "E894.0", {"start": v(-12.98, -9.35) * mm, "end": v(-13.02, -8.7) * mm});
            skLineSegment(sketch, "E895.0", {"start": v(-13.02, -8.7) * mm, "end": v(-12.88, -8.06) * mm});
            skLineSegment(sketch, "E896.0", {"start": v(-12.88, -8.06) * mm, "end": v(-12.58, -7.48) * mm});
            skLineSegment(sketch, "E897.0", {"start": v(-17.04, -12.42) * mm, "end": v(-16.88, -12.3) * mm});
            skLineSegment(sketch, "E898.0", {"start": v(0.22, -20.95) * mm, "end": v(0.64, -18.97) * mm});
            skLineSegment(sketch, "E899.0", {"start": v(-18.95, -13.59) * mm, "end": v(-18.34, -13.09) * mm});
            skLineSegment(sketch, "E899.1", {"start": v(-20.68, -10.15) * mm, "end": v(-18.95, -13.59) * mm});
            skLineSegment(sketch, "E899.2", {"start": v(-18.46, -8.5) * mm, "end": v(-20.68, -10.15) * mm});
            skLineSegment(sketch, "E899.3", {"start": v(-16.54, -7.1) * mm, "end": v(-18.46, -8.5) * mm});
            skLineSegment(sketch, "E899.4", {"start": v(-15.24, -6.14) * mm, "end": v(-16.54, -7.1) * mm});
            skLineSegment(sketch, "E899.5", {"start": v(-14.63, -5.69) * mm, "end": v(-15.24, -6.14) * mm});
            skLineSegment(sketch, "E899.6", {"start": v(-14, -5.1) * mm, "end": v(-14.63, -5.69) * mm});
            skLineSegment(sketch, "E899.7", {"start": v(-13.55, -4.48) * mm, "end": v(-14, -5.1) * mm});
            skLineSegment(sketch, "E899.8", {"start": v(-13.12, -3.52) * mm, "end": v(-13.55, -4.48) * mm});
            skLineSegment(sketch, "E899.9", {"start": v(-13.1, -2.68) * mm, "end": v(-13.12, -3.52) * mm});
            skLineSegment(sketch, "E899.10", {"start": v(-13.92, -2.48) * mm, "end": v(-13.1, -2.68) * mm});
            skLineSegment(sketch, "E899.11", {"start": v(-14.98, -2.66) * mm, "end": v(-13.92, -2.48) * mm});
            skLineSegment(sketch, "E899.12", {"start": v(-16.41, -3.4) * mm, "end": v(-14.98, -2.66) * mm});
            skLineSegment(sketch, "E899.13", {"start": v(-16.84, -3.73) * mm, "end": v(-16.41, -3.4) * mm});
            skLineSegment(sketch, "E899.14", {"start": v(-17.96, -4.62) * mm, "end": v(-16.84, -3.73) * mm});
            skLineSegment(sketch, "E899.15", {"start": v(-19.7, -6) * mm, "end": v(-17.96, -4.62) * mm});
            skLineSegment(sketch, "E899.16", {"start": v(-21.6, -7.5) * mm, "end": v(-19.7, -6) * mm});
            skLineSegment(sketch, "E899.17", {"start": v(-22.48, -3.55) * mm, "end": v(-21.6, -7.5) * mm});
            skLineSegment(sketch, "E899.18", {"start": v(-22.71, 0.65) * mm, "end": v(-22.48, -3.55) * mm});
            skLineSegment(sketch, "E899.19", {"start": v(-19.9, 1.13) * mm, "end": v(-22.71, 0.65) * mm});
            skLineSegment(sketch, "E899.20", {"start": v(-17.61, 1.3) * mm, "end": v(-19.9, 1.13) * mm});
            skLineSegment(sketch, "E899.21", {"start": v(-0.07, -20.88) * mm, "end": v(0.35, -18.92) * mm});
            skLineSegment(sketch, "E899.22", {"start": v(-0.68, -22.8) * mm, "end": v(-0.07, -20.88) * mm});
            skLineSegment(sketch, "E899.23", {"start": v(-1.42, -24.63) * mm, "end": v(-0.68, -22.8) * mm});
            skLineSegment(sketch, "E899.24", {"start": v(-2.12, -26.08) * mm, "end": v(-1.42, -24.63) * mm});
            skLineSegment(sketch, "E899.25", {"start": v(-6.19, -24.76) * mm, "end": v(-2.12, -26.08) * mm});
            skLineSegment(sketch, "E899.26", {"start": v(-10.22, -22.65) * mm, "end": v(-6.19, -24.76) * mm});
            skLineSegment(sketch, "E899.27", {"start": v(-13.9, -19.84) * mm, "end": v(-10.22, -22.65) * mm});
            skLineSegment(sketch, "E899.28", {"start": v(-17.02, -16.44) * mm, "end": v(-13.9, -19.84) * mm});
            skLineSegment(sketch, "E899.29", {"start": v(-16.38, -15.99) * mm, "end": v(-17.02, -16.44) * mm});
            skLineSegment(sketch, "E899.30", {"start": v(-15.65, -15.47) * mm, "end": v(-16.38, -15.99) * mm});
            skLineSegment(sketch, "E899.31", {"start": v(-15.14, -15.1) * mm, "end": v(-15.65, -15.47) * mm});
            skLineSegment(sketch, "E899.32", {"start": v(-14.84, -14.88) * mm, "end": v(-15.14, -15.1) * mm});
            skLineSegment(sketch, "E899.33", {"start": v(-16.26, -11.54) * mm, "end": v(-15.34, -11.22) * mm});
            skLineSegment(sketch, "E899.34", {"start": v(-17.06, -12.05) * mm, "end": v(-16.26, -11.54) * mm});
            skLineSegment(sketch, "E899.35", {"start": v(-17.23, -12.19) * mm, "end": v(-17.06, -12.05) * mm});
            skLineSegment(sketch, "E899.36", {"start": v(-17.66, -12.54) * mm, "end": v(-17.23, -12.19) * mm});
            skLineSegment(sketch, "E899.37", {"start": v(-15.34, -11.22) * mm, "end": v(-14.1, -11.07) * mm});
            skLineSegment(sketch, "E899.38", {"start": v(-14.1, -11.07) * mm, "end": v(-13.2, -11.35) * mm});
            skLineSegment(sketch, "E899.39", {"start": v(-13.2, -11.35) * mm, "end": v(-13.16, -12.3) * mm});
            skLineSegment(sketch, "E899.40", {"start": v(-13.16, -12.3) * mm, "end": v(-13.61, -13.46) * mm});
            skLineSegment(sketch, "E899.41", {"start": v(-13.61, -13.46) * mm, "end": v(-14.1, -14.19) * mm});
            skLineSegment(sketch, "E899.42", {"start": v(-14.1, -14.19) * mm, "end": v(-14.84, -14.88) * mm});
            skLineSegment(sketch, "E899.43", {"start": v(0.35, -18.92) * mm, "end": v(0.5, -17) * mm});
            skLineSegment(sketch, "E899.44", {"start": v(0.5, -17) * mm, "end": v(0.36, -15.14) * mm});
            skLineSegment(sketch, "E899.45", {"start": v(0.36, -15.14) * mm, "end": v(-0.15, -13.42) * mm});
            skLineSegment(sketch, "E899.46", {"start": v(-0.15, -13.42) * mm, "end": v(-0.97, -12.05) * mm});
            skLineSegment(sketch, "E899.47", {"start": v(-0.97, -12.05) * mm, "end": v(-3.54, -13.1) * mm});
            skLineSegment(sketch, "E899.48", {"start": v(-3.54, -13.1) * mm, "end": v(-5.4, -13.83) * mm});
            skLineSegment(sketch, "E899.49", {"start": v(-5.4, -13.83) * mm, "end": v(-7.33, -14.5) * mm});
            skLineSegment(sketch, "E899.50", {"start": v(-7.33, -14.5) * mm, "end": v(-8.02, -14.65) * mm});
            skLineSegment(sketch, "E899.51", {"start": v(-8.02, -14.65) * mm, "end": v(-8.76, -14.62) * mm});
            skLineSegment(sketch, "E899.52", {"start": v(-8.76, -14.62) * mm, "end": v(-9.47, -14.37) * mm});
            skLineSegment(sketch, "E899.53", {"start": v(-9.47, -14.37) * mm, "end": v(-10.04, -13.9) * mm});
            skLineSegment(sketch, "E899.54", {"start": v(-10.04, -13.9) * mm, "end": v(-12.96, -10.1) * mm});
            skLineSegment(sketch, "E899.55", {"start": v(-12.96, -10.1) * mm, "end": v(-13.27, -9.43) * mm});
            skLineSegment(sketch, "E899.56", {"start": v(-13.27, -9.43) * mm, "end": v(-13.32, -8.68) * mm});
            skLineSegment(sketch, "E899.57", {"start": v(-13.32, -8.68) * mm, "end": v(-13.16, -7.96) * mm});
            skLineSegment(sketch, "E899.58", {"start": v(-13.16, -7.96) * mm, "end": v(-12.84, -7.33) * mm});
            skLineSegment(sketch, "E899.59", {"start": v(-12.84, -7.33) * mm, "end": v(-11.57, -5.47) * mm});
            skLineSegment(sketch, "E899.60", {"start": v(-11.57, -5.47) * mm, "end": v(-10.25, -3.68) * mm});
            skLineSegment(sketch, "E899.61", {"start": v(-10.25, -3.68) * mm, "end": v(-8.85, -1.82) * mm});
            skLineSegment(sketch, "E899.62", {"start": v(-8.85, -1.82) * mm, "end": v(-9.94, -0.67) * mm});
            skLineSegment(sketch, "E899.63", {"start": v(-9.94, -0.67) * mm, "end": v(-11.5, 0.26) * mm});
            skLineSegment(sketch, "E899.64", {"start": v(-11.5, 0.26) * mm, "end": v(-13.36, 0.91) * mm});
            skLineSegment(sketch, "E899.65", {"start": v(-13.36, 0.91) * mm, "end": v(-15.32, 1.23) * mm});
            skLineSegment(sketch, "E899.66", {"start": v(-15.32, 1.23) * mm, "end": v(-17.61, 1.3) * mm});
            skLineSegment(sketch, "E900", {"start": v(-17.66, -12.54) * mm, "end": v(-18.34, -13.09) * mm});
            skLineSegment(sketch, "E901.0", {"start": v(20.47, -0.12) * mm, "end": v(16.67, -2.08) * mm});
            skLineSegment(sketch, "E902.0", {"start": v(16.67, -2.08) * mm, "end": v(15.74, -4.84) * mm});
            skLineSegment(sketch, "E903.0", {"start": v(15.74, -4.84) * mm, "end": v(14.62, -7.53) * mm});
            skLineSegment(sketch, "E904.0", {"start": v(14.62, -7.53) * mm, "end": v(11.61, -13.37) * mm});
            skLineSegment(sketch, "E905.0", {"start": v(11.61, -13.37) * mm, "end": v(7.95, -18.86) * mm});
            skLineSegment(sketch, "E906.0", {"start": v(7.95, -18.86) * mm, "end": v(4.36, -23.16) * mm});
            skLineSegment(sketch, "E907.0", {"start": v(4.36, -23.16) * mm, "end": v(0.38, -26.9) * mm});
            skLineSegment(sketch, "E908.0", {"start": v(0.38, -26.9) * mm, "end": v(5.72, -27.14) * mm});
            skLineSegment(sketch, "E909.0", {"start": v(24.01, 1.93) * mm, "end": v(20.47, -0.12) * mm});
            skLineSegment(sketch, "E910.0", {"start": v(27.44, 4.15) * mm, "end": v(24.01, 1.93) * mm});
            skLineSegment(sketch, "E911.0", {"start": v(30.89, 6.64) * mm, "end": v(27.44, 4.15) * mm});
            skLineSegment(sketch, "E912.0", {"start": v(31.53, 2.78) * mm, "end": v(30.89, 6.64) * mm});
            skLineSegment(sketch, "E913.0", {"start": v(31.63, -1.1) * mm, "end": v(31.53, 2.78) * mm});
            skLineSegment(sketch, "E914.0", {"start": v(31.17, -4.95) * mm, "end": v(31.63, -1.1) * mm});
            skLineSegment(sketch, "E915.0", {"start": v(30.18, -8.7) * mm, "end": v(31.17, -4.95) * mm});
            skLineSegment(sketch, "E916.0", {"start": v(28.66, -12.3) * mm, "end": v(30.18, -8.7) * mm});
            skLineSegment(sketch, "E917.0", {"start": v(26.62, -15.66) * mm, "end": v(28.66, -12.3) * mm});
            skLineSegment(sketch, "E918.0", {"start": v(24.06, -18.75) * mm, "end": v(26.62, -15.66) * mm});
            skLineSegment(sketch, "E919.0", {"start": v(21, -21.5) * mm, "end": v(24.06, -18.75) * mm});
            skLineSegment(sketch, "E920.0", {"start": v(16.2, -24.47) * mm, "end": v(21, -21.5) * mm});
            skLineSegment(sketch, "E921.0", {"start": v(11.04, -26.34) * mm, "end": v(16.2, -24.47) * mm});
            skLineSegment(sketch, "E922.0", {"start": v(5.72, -27.14) * mm, "end": v(11.04, -26.34) * mm});
            skLineSegment(sketch, "E923.0", {"start": v(16.02, -4.94) * mm, "end": v(14.9, -7.66) * mm});
            skLineSegment(sketch, "E923.1", {"start": v(16.92, -2.29) * mm, "end": v(16.02, -4.94) * mm});
            skLineSegment(sketch, "E923.2", {"start": v(20.6, -0.39) * mm, "end": v(16.92, -2.29) * mm});
            skLineSegment(sketch, "E923.3", {"start": v(24.17, 1.67) * mm, "end": v(20.6, -0.39) * mm});
            skLineSegment(sketch, "E923.4", {"start": v(27.61, 3.9) * mm, "end": v(24.17, 1.67) * mm});
            skLineSegment(sketch, "E923.5", {"start": v(14.9, -7.66) * mm, "end": v(11.87, -13.52) * mm});
            skLineSegment(sketch, "E923.6", {"start": v(30.67, 6.1) * mm, "end": v(27.61, 3.9) * mm});
            skLineSegment(sketch, "E923.7", {"start": v(31.23, 2.75) * mm, "end": v(30.67, 6.1) * mm});
            skLineSegment(sketch, "E923.8", {"start": v(31.33, -1.09) * mm, "end": v(31.23, 2.75) * mm});
            skLineSegment(sketch, "E923.9", {"start": v(30.88, -4.9) * mm, "end": v(31.33, -1.09) * mm});
            skLineSegment(sketch, "E923.10", {"start": v(29.9, -8.6) * mm, "end": v(30.88, -4.9) * mm});
            skLineSegment(sketch, "E923.11", {"start": v(28.4, -12.15) * mm, "end": v(29.9, -8.6) * mm});
            skLineSegment(sketch, "E923.12", {"start": v(1.1, -26.63) * mm, "end": v(5.7, -26.84) * mm});
            skLineSegment(sketch, "E923.13", {"start": v(4.58, -23.37) * mm, "end": v(1.1, -26.63) * mm});
            skLineSegment(sketch, "E923.14", {"start": v(8.19, -19.04) * mm, "end": v(4.58, -23.37) * mm});
            skLineSegment(sketch, "E923.15", {"start": v(11.87, -13.52) * mm, "end": v(8.19, -19.04) * mm});
            skLineSegment(sketch, "E923.16", {"start": v(5.7, -26.84) * mm, "end": v(10.97, -26.05) * mm});
            skLineSegment(sketch, "E923.17", {"start": v(10.97, -26.05) * mm, "end": v(16.06, -24.2) * mm});
            skLineSegment(sketch, "E923.18", {"start": v(16.06, -24.2) * mm, "end": v(20.81, -21.26) * mm});
            skLineSegment(sketch, "E923.19", {"start": v(20.81, -21.26) * mm, "end": v(23.84, -18.54) * mm});
            skLineSegment(sketch, "E923.20", {"start": v(23.84, -18.54) * mm, "end": v(26.37, -15.49) * mm});
            skLineSegment(sketch, "E923.21", {"start": v(26.37, -15.49) * mm, "end": v(28.4, -12.15) * mm});
            skSolve(sketch);
        }
        {
            var Q0;
            Q0=makeQuery(id+"F9.imprint","IMPRINT",FACE,{"disambiguationData":[TD([[makeQuery(id+"F9.imprint","IMPRINT",EDGE,{"derivedFrom":sQuery(id+"F9.wireOp",EDGE,"E899.0")}),1.0]])]});
            var Q1;
            Q1=makeQuery(id+"F9.imprint","IMPRINT",FACE,{"disambiguationData":[TD([[makeQuery(id+"F9.imprint","IMPRINT",EDGE,{"derivedFrom":sQuery(id+"F9.wireOp",EDGE,"E829.0")}),1.0]])]});
            var Q2;
            Q2=makeQuery(id+"F9.imprint","IMPRINT",FACE,{"disambiguationData":[TD([[makeQuery(id+"F9.imprint","IMPRINT",EDGE,{"derivedFrom":sQuery(id+"F9.wireOp",EDGE,"E923.0")}),1.0]])]});
            extrude(context, id + "F10", {"entities" : qUnion([Q0, Q1, Q2]), "depth" : 1 * mm});
        }
        {
            var Q0;
            Q0=makeQuery(id+"F10.opExtrude","CAP_FACE",FACE,{"disambiguationData":[OSD([sQuery(id+"F9.wireOp",EDGE,"E829.0"),sQuery(id+"F9.wireOp",EDGE,"E829.1"),sQuery(id+"F9.wireOp",EDGE,"E829.2"),sQuery(id+"F9.wireOp",EDGE,"E829.3"),sQuery(id+"F9.wireOp",EDGE,"E829.4"),sQuery(id+"F9.wireOp",EDGE,"E829.5"),sQuery(id+"F9.wireOp",EDGE,"E829.6"),sQuery(id+"F9.wireOp",EDGE,"E829.7"),sQuery(id+"F9.wireOp",EDGE,"E829.8"),sQuery(id+"F9.wireOp",EDGE,"E829.9"),sQuery(id+"F9.wireOp",EDGE,"E829.10"),sQuery(id+"F9.wireOp",EDGE,"E829.11"),sQuery(id+"F9.wireOp",EDGE,"E829.12"),sQuery(id+"F9.wireOp",EDGE,"E829.13"),sQuery(id+"F9.wireOp",EDGE,"E829.14"),sQuery(id+"F9.wireOp",EDGE,"E829.15"),sQuery(id+"F9.wireOp",EDGE,"E829.16"),sQuery(id+"F9.wireOp",EDGE,"E829.17"),sQuery(id+"F9.wireOp",EDGE,"E829.18"),sQuery(id+"F9.wireOp",EDGE,"E829.19"),sQuery(id+"F9.wireOp",EDGE,"E829.20"),sQuery(id+"F9.wireOp",EDGE,"E829.21")])],"isStart":true});
            var Q1;
            Q1=makeQuery(id+"F7.opExtrude","CAP_FACE",FACE,{"disambiguationData":[OSD([sQuery(id+"F6.wireOp",EDGE,"E801.0"),sQuery(id+"F6.wireOp",EDGE,"E801.1"),sQuery(id+"F6.wireOp",EDGE,"E801.2"),sQuery(id+"F6.wireOp",EDGE,"E801.3"),sQuery(id+"F6.wireOp",EDGE,"E801.4"),sQuery(id+"F6.wireOp",EDGE,"E801.5"),sQuery(id+"F6.wireOp",EDGE,"E801.6"),sQuery(id+"F6.wireOp",EDGE,"E801.7"),sQuery(id+"F6.wireOp",EDGE,"E801.8"),sQuery(id+"F6.wireOp",EDGE,"E801.9"),sQuery(id+"F6.wireOp",EDGE,"E801.10"),sQuery(id+"F6.wireOp",EDGE,"E801.11"),sQuery(id+"F6.wireOp",EDGE,"E801.12"),sQuery(id+"F6.wireOp",EDGE,"E801.13"),sQuery(id+"F6.wireOp",EDGE,"E801.14"),sQuery(id+"F6.wireOp",EDGE,"E802.0"),sQuery(id+"F6.wireOp",EDGE,"E803.0"),sQuery(id+"F6.wireOp",EDGE,"E803.1"),sQuery(id+"F6.wireOp",EDGE,"E803.2"),sQuery(id+"F6.wireOp",EDGE,"E803.3"),sQuery(id+"F6.wireOp",EDGE,"E803.4"),sQuery(id+"F6.wireOp",EDGE,"E804.0"),sQuery(id+"F6.wireOp",EDGE,"E804.1"),sQuery(id+"F6.wireOp",EDGE,"E804.2"),sQuery(id+"F6.wireOp",EDGE,"E804.3"),sQuery(id+"F6.wireOp",EDGE,"E804.4"),sQuery(id+"F6.wireOp",EDGE,"E804.5"),sQuery(id+"F6.wireOp",EDGE,"E804.6"),sQuery(id+"F6.wireOp",EDGE,"E804.7"),sQuery(id+"F6.wireOp",EDGE,"E804.8"),sQuery(id+"F6.wireOp",EDGE,"E804.9"),sQuery(id+"F6.wireOp",EDGE,"E804.10"),sQuery(id+"F6.wireOp",EDGE,"E804.11"),sQuery(id+"F6.wireOp",EDGE,"E804.12"),sQuery(id+"F6.wireOp",EDGE,"E804.13"),sQuery(id+"F6.wireOp",EDGE,"E804.14"),sQuery(id+"F6.wireOp",EDGE,"E804.15"),sQuery(id+"F6.wireOp",EDGE,"E804.16"),sQuery(id+"F6.wireOp",EDGE,"E804.17"),sQuery(id+"F6.wireOp",EDGE,"E804.18"),sQuery(id+"F6.wireOp",EDGE,"E804.19"),sQuery(id+"F6.wireOp",EDGE,"E804.20"),sQuery(id+"F6.wireOp",EDGE,"E804.21"),sQuery(id+"F6.wireOp",EDGE,"E804.22"),sQuery(id+"F6.wireOp",EDGE,"E804.23"),sQuery(id+"F6.wireOp",EDGE,"E804.24"),sQuery(id+"F6.wireOp",EDGE,"E804.25"),sQuery(id+"F6.wireOp",EDGE,"E804.26"),sQuery(id+"F6.wireOp",EDGE,"E804.27"),sQuery(id+"F6.wireOp",EDGE,"E804.28"),sQuery(id+"F6.wireOp",EDGE,"E804.29"),sQuery(id+"F6.wireOp",EDGE,"E804.30"),sQuery(id+"F6.wireOp",EDGE,"E804.31"),sQuery(id+"F6.wireOp",EDGE,"E804.32"),sQuery(id+"F6.wireOp",EDGE,"E804.33"),sQuery(id+"F6.wireOp",EDGE,"E804.34"),sQuery(id+"F6.wireOp",EDGE,"E804.35"),sQuery(id+"F6.wireOp",EDGE,"E804.36"),sQuery(id+"F6.wireOp",EDGE,"E804.37"),sQuery(id+"F6.wireOp",EDGE,"E804.38"),sQuery(id+"F6.wireOp",EDGE,"E804.39"),sQuery(id+"F6.wireOp",EDGE,"E804.40"),sQuery(id+"F6.wireOp",EDGE,"E804.41"),sQuery(id+"F6.wireOp",EDGE,"E804.42"),sQuery(id+"F6.wireOp",EDGE,"E804.43"),sQuery(id+"F6.wireOp",EDGE,"E804.44"),sQuery(id+"F6.wireOp",EDGE,"E804.45"),sQuery(id+"F6.wireOp",EDGE,"E804.46"),sQuery(id+"F6.wireOp",EDGE,"E804.47"),sQuery(id+"F6.wireOp",EDGE,"E804.48"),sQuery(id+"F6.wireOp",EDGE,"E804.49"),sQuery(id+"F6.wireOp",EDGE,"E805"),sQuery(id+"F6.wireOp",EDGE,"E806")])],"isStart":true});
            var Q2;
            Q2=makeQuery(id+"F10.opExtrude","CAP_FACE",FACE,{"disambiguationData":[OSD([sQuery(id+"F9.wireOp",EDGE,"E923.0"),sQuery(id+"F9.wireOp",EDGE,"E923.1"),sQuery(id+"F9.wireOp",EDGE,"E923.2"),sQuery(id+"F9.wireOp",EDGE,"E923.3"),sQuery(id+"F9.wireOp",EDGE,"E923.4"),sQuery(id+"F9.wireOp",EDGE,"E923.5"),sQuery(id+"F9.wireOp",EDGE,"E923.6"),sQuery(id+"F9.wireOp",EDGE,"E923.7"),sQuery(id+"F9.wireOp",EDGE,"E923.8"),sQuery(id+"F9.wireOp",EDGE,"E923.9"),sQuery(id+"F9.wireOp",EDGE,"E923.10"),sQuery(id+"F9.wireOp",EDGE,"E923.11"),sQuery(id+"F9.wireOp",EDGE,"E923.12"),sQuery(id+"F9.wireOp",EDGE,"E923.13"),sQuery(id+"F9.wireOp",EDGE,"E923.14"),sQuery(id+"F9.wireOp",EDGE,"E923.15"),sQuery(id+"F9.wireOp",EDGE,"E923.16"),sQuery(id+"F9.wireOp",EDGE,"E923.17"),sQuery(id+"F9.wireOp",EDGE,"E923.18"),sQuery(id+"F9.wireOp",EDGE,"E923.19"),sQuery(id+"F9.wireOp",EDGE,"E923.20"),sQuery(id+"F9.wireOp",EDGE,"E923.21")])],"isStart":true});
            chamfer(context, id + "F11", {"entities" : qUnion([Q0, Q1, Q2]), "width" : 0.5 * mm, "tangentPropagation" : true});
        }
    });
